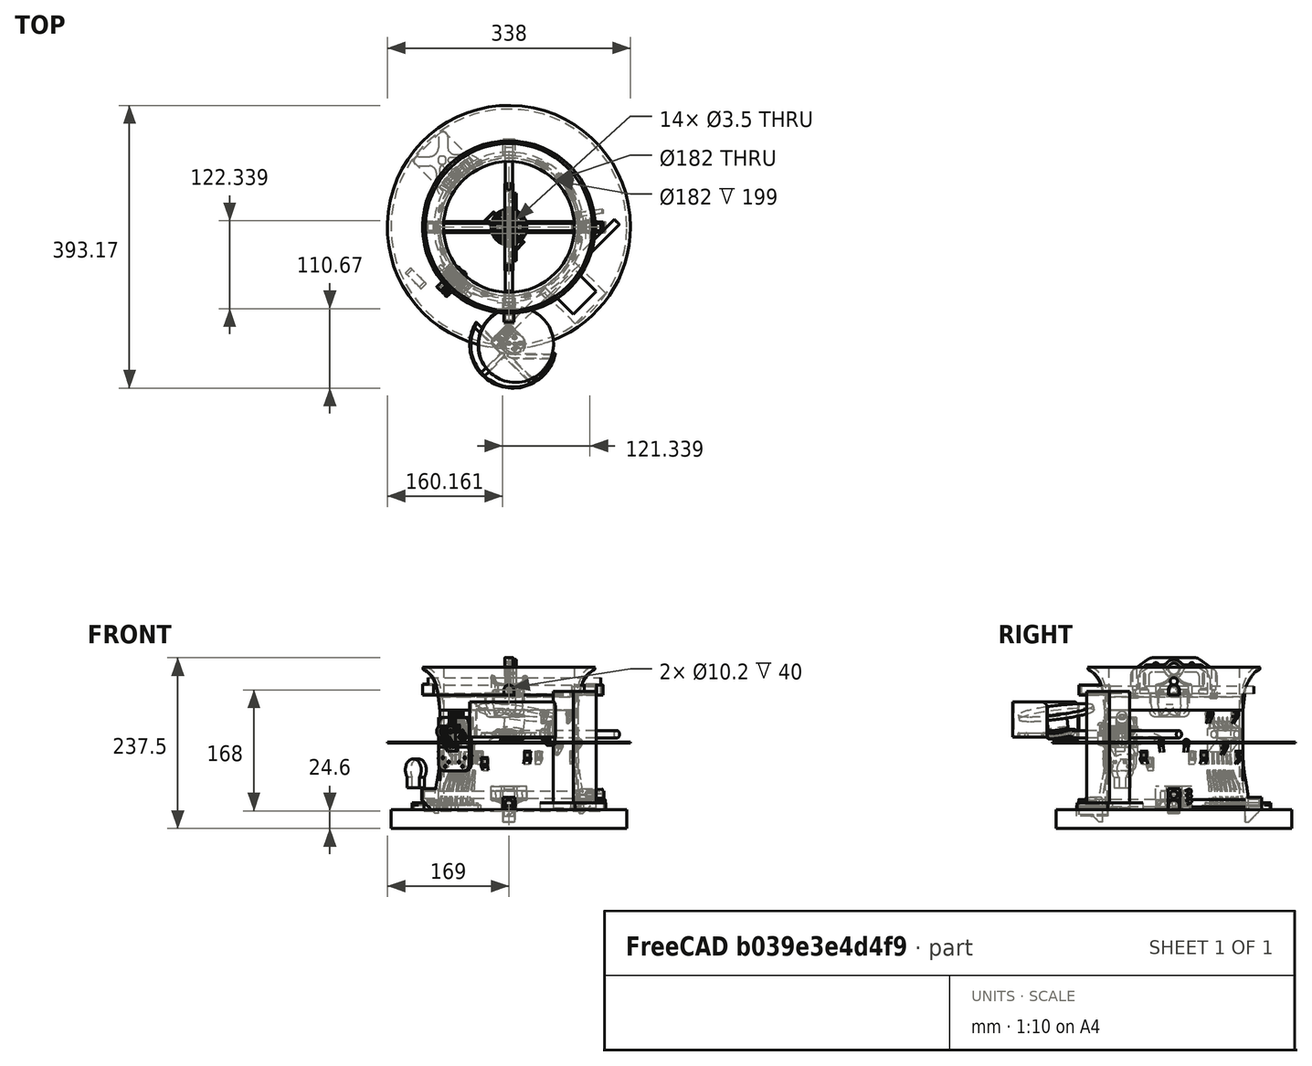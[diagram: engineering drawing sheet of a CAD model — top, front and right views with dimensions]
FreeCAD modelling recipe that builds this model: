
FCSTD DOCUMENT  (FreeCAD 0.19R24276 (Git))
Label: NEVA-CYLCOPE-MARK2
License: All rights reserved
LicenseURL: http://en.wikipedia.org/wiki/All_rights_reserved
objects: Sketcher::SketchObject×128, PartDesign::Pad×65, PartDesign::Pocket×52, PartDesign::Body×34, PartDesign::Fillet×24, PartDesign::Mirrored×23, Part::FeaturePython×19, Spreadsheet::Sheet×8, PartDesign::Chamfer×8, App::Part×8, PartDesign::Revolution×6, PartDesign::Groove×4, PartDesign::PolarPattern×3, Part::Feature×2, PartDesign::Boolean×1, PartDesign::LinearPattern×1, Part::MultiFuse×1, Part::Mirroring×1, Part::Fuse×1
note: 532 computed .brp shape members not serialized (recipe doc carries the construction recipe); baked Part::Feature solids carry a one-line shape summary decoded from their .brp

FEATURE [Spreadsheet::Sheet] Spreadsheet  label="sta"
  cells = A1=DONNEES POUR LE DESIGN DES STA; A2=Main_diam_base; B2=50; D2=base_pad; E2=6; A3=Carbon tube diam; B3=10.2; D3=epaisseur-renfort; E3==B3 / 2; A4=Epaisseur autour carbon; B4=3; A5=Distance entre 2 tubes; B5=2; A7=Distance entre 2 stators; B7=123; A8=> z position sta inlet; B8==B7 + 2 * E2; A10=Passage bullet tmotor; A11=diamètre bullet; B11=5.6; A12=diamètre cable; B12=2.4
FEATURE [Sketcher::SketchObject] Sketch001
  FullyConstrained = true
  MapMode = 5
  Placement = pos=(0,0,0) rot=(1,0,0;1.5708rad)
  Support = -> [XZ_Plane001]
  expr: Constraints[10] = <<sta>>.B3 / 2
  expr: Constraints[0] = <<sta>>.B3 + <<sta>>.B4 * 2
  sketch-geometry (4):
    g0: ArcOfCircle CenterX=0 CenterY=5.1 CenterZ=0 NormalX=0 NormalY=0 NormalZ=1 AngleXU=0 Radius=8.1 StartAngle=0 EndAngle=3.14159
    g1: LineSegment StartX=-8.1 StartY=0 StartZ=0 EndX=8.1 EndY=0 EndZ=0
    g2: LineSegment StartX=-8.1 StartY=5.1 StartZ=0 EndX=-8.1 EndY=0 EndZ=0
    g3: LineSegment StartX=8.1 StartY=5.1 StartZ=0 EndX=8.1 EndY=0 EndZ=0
  constraints (12):
    c: Diameter(g0) = 16.2
    c: PointOnObject(g1,g-1)
    c: Horizontal(g1)
    c: Coincident(g2,g1)
    c: Coincident(g3,g0)
    c: Coincident(g3,g1)
    c: Perpendicular(g3,g1)
    c: Perpendicular(g1,g2)
    c: Equal(g2,g3)
    c: Tangent(g2,g0) = -1.5708
    c: DistanceY(g0) = 5.1
    c: PointOnObject(g0,g-2)
FEATURE [PartDesign::Pad] Pad001  label="tube_inf"
  Direction = (1,1,1)
  Length = 50
  Length2 = 100
  Midplane = true
  Placement = pos=(0,0,0) rot=(1,0,0;1.5708rad)
  Profile = -> Sketch001
  Refine = true
  Type = 0
  expr: Length = <<sta>>.B2
FEATURE [Sketcher::SketchObject] Sketch002
  FullyConstrained = true
  MapMode = 5
  Placement = pos=(0,0,0) rot=(0.57735,0.57735,0.57735;2.0944rad)
  Support = -> [YZ_Plane001]
  expr: Constraints[11] = <<sta>>.B3 + <<sta>>.B4 * 2
  expr: Constraints[1] = <<sta>>.B5 + 1.5 * <<sta>>.B3
  sketch-geometry (4):
    g0: ArcOfCircle CenterX=0 CenterY=17.3 CenterZ=0 NormalX=0 NormalY=0 NormalZ=1 AngleXU=0 Radius=8.1 StartAngle=0 EndAngle=3.14159
    g1: LineSegment StartX=-8.1 StartY=17.3 StartZ=0 EndX=-8.1 EndY=0 EndZ=0
    g2: LineSegment StartX=8.1 StartY=17.3 StartZ=0 EndX=8.1 EndY=0 EndZ=0
    g3: LineSegment StartX=-8.1 StartY=0 StartZ=0 EndX=8.1 EndY=0 EndZ=0
  constraints (12):
    c: PointOnObject(g0,g-2)
    c: DistanceY(g0) = 17.3
    c: PointOnObject(g1,g-1)
    c: Vertical(g1)
    c: Coincident(g2,g0)
    c: PointOnObject(g2,g-1)
    c: Vertical(g2)
    c: Coincident(g3,g1)
    c: Coincident(g3,g2)
    c: Tangent(g1,g0) = -1.5708
    c: Equal(g2,g1)
    c: Diameter(g0) = 16.2
FEATURE [PartDesign::Pad] Pad002  label="tube_sup"
  BaseFeature = -> Pad001
  Direction = (1,1,1)
  Length = 50
  Length2 = 100
  Midplane = true
  Placement = pos=(0,0,0) rot=(1,0,0;1.5708rad)
  Profile = -> Sketch002
  Refine = true
  Type = 0
  expr: Length = <<sta>>.B2
FEATURE [Sketcher::SketchObject] Sketch003
  FullyConstrained = true
  MapMode = 5
  Placement = pos=(0,0,0) rot=(0.57735,0.57735,0.57735;2.0944rad)
  Support = -> [YZ_Plane001]
  expr: Constraints[2] = 1.5 * <<sta>>.B3 + <<sta>>.B5
  expr: Constraints[1] = <<sta>>.B3
  sketch-geometry (1):
    g0: Circle CenterX=0 CenterY=17.3 CenterZ=0 NormalX=0 NormalY=0 NormalZ=1 AngleXU=0 Radius=5.1
  constraints (3):
    c: PointOnObject(g0,g-2)
    c: Diameter(g0) = 10.2
    c: DistanceY(g0) = 17.3
FEATURE [Sketcher::SketchObject] Sketch004
  FullyConstrained = true
  MapMode = 5
  Placement = pos=(0,0,0) rot=(1,0,0;1.5708rad)
  Support = -> [XZ_Plane001]
  expr: Constraints[2] = <<sta>>.B3 / 2
  expr: Constraints[1] = <<sta>>.B3
  sketch-geometry (1):
    g0: Circle CenterX=0 CenterY=5.1 CenterZ=0 NormalX=0 NormalY=0 NormalZ=1 AngleXU=0 Radius=5.1
  constraints (3):
    c: PointOnObject(g0,g-2)
    c: Diameter(g0) = 10.2
    c: DistanceY(g0) = 5.1
FEATURE [Sketcher::SketchObject] Sketch005
  FullyConstrained = false
  MapMode = 5
  Support = -> [XY_Plane001]
  expr: Constraints[1] = <<sta>>.B2
  sketch-geometry (2):
    g0: Circle CenterX=0 CenterY=0 CenterZ=0 NormalX=0 NormalY=0 NormalZ=1 AngleXU=0 Radius=25
    g1: Circle CenterX=0 CenterY=0 CenterZ=0 NormalX=0 NormalY=0 NormalZ=1 AngleXU=0 Radius=32.5573
  constraints (3):
    c: Coincident(g0,g-1)
    c: Diameter(g0) = 50
    c: Coincident(g1,g0)
FEATURE [Sketcher::SketchObject] Sketch006
  AttachmentOffset = pos=(0,0,0) rot=(0,0,1;0.785398rad)
  FullyConstrained = true
  MapMode = 5
  Placement = pos=(0,0,0) rot=(0,0,1;0.785398rad)
  Support = -> [XY_Plane001]
  expr: Constraints[1] = <<screw>>.B5 + 0.3
  sketch-geometry (1):
    g0: Circle CenterX=-12.5 CenterY=0 CenterZ=0 NormalX=0 NormalY=0 NormalZ=1 AngleXU=0 Radius=2.95
  constraints (3):
    c: PointOnObject(g0,g-1)
    c: Diameter(g0) = 5.9
    c: DistanceX(g0) = -12.5
FEATURE [Sketcher::SketchObject] Sketch007
  AttachmentOffset = pos=(0,0,0) rot=(0,0,1;0.785398rad)
  FullyConstrained = true
  MapMode = 5
  Placement = pos=(0,0,0) rot=(0,0,1;0.785398rad)
  Support = -> [XY_Plane001]
  expr: Constraints[1] = <<screw>>.B4 + 0.25
  sketch-geometry (1):
    g0: Circle CenterX=-12.5 CenterY=0 CenterZ=0 NormalX=0 NormalY=0 NormalZ=1 AngleXU=0 Radius=1.75
  constraints (3):
    c: PointOnObject(g0,g-1)
    c: Diameter(g0) = 3.5
    c: DistanceX(g0) = -12.5
FEATURE [Sketcher::SketchObject] Sketch008
  AttachmentOffset = pos=(0,0,-6) rot=(0,0,1;0rad)
  FullyConstrained = true
  MapMode = 5
  Placement = pos=(0,0,-6) rot=(0,0,1;0rad)
  Support = -> [XY_Plane001]
  expr: .AttachmentOffset.Base.z = -<<sta>>.E2
  sketch-geometry (1):
    g0: Circle CenterX=0 CenterY=0 CenterZ=0 NormalX=0 NormalY=0 NormalZ=1 AngleXU=0 Radius=6.25
  constraints (2):
    c: Coincident(g0,g-1)
    c: Diameter(g0) = 12.5
FEATURE [Spreadsheet::Sheet] Spreadsheet001  label="sho"
  cells = A1=DONNEES POUR LE DESIGN DU SHO; A3=inner-diam; B3=182; A4=thickness; B4=5; A5=Hauteur tube principal; B5==198.5 - D6 - D7; A6=deport diffuseur; B6=8; C6=hauteur outlet; D6=80; A7=Deport inlet; B7=25; C7=hauteur inlet; D7=60; A8=Nervure renfort epaisseur; B8=2.9; A10=PASSAGE COLIERS SERRAGE; A11=largeur; B11=3.8; A12=épaisseur; B12=1.7; A13=diamètre de cables; B13=10
FEATURE [Spreadsheet::Sheet] Spreadsheet002  label="screw"
  cells = A2=M3 SCREW PARAM; A4=M3 diam; B4=3.25; A5=M3 head diam; B5=5.6; A6=M3 NUT height; B6=5.5; A7=M3 NYLSTOP NUT depth; B7=4.1
FEATURE [Spreadsheet::Sheet] Spreadsheet003  label="plug"
  cells = A1=DONNEES POUR LES PLUGS STATOR; A3=longueur emboitement; B3==20 - <<sho>>.B4; A4=epaisseur autour cabron; B4=3; A5=longueur butée; B5=3; D5=> longueur ajustement vis; E5==B3 - 2 * B4 - B5; A6=Overangle; B6==45°; D6=> Hauteur pad; E6==(B3 + B5) / tan(B6); A7=POSITION; A8=z_inf; B8==-B4; A9=z_sup; B9==B8 + <<sta>>.B3 + <<sta>>.B5
FEATURE [Sketcher::SketchObject] Sketch023
  FullyConstrained = true
  MapMode = 5
  Support = -> [XY_Plane005]
  expr: Constraints[4] = -<<sho>>.B3 / 2
  expr: Constraints[5] = <<sho>>.B4 + <<plug>>.B3 + <<plug>>.B5
  expr: Constraints[6] = <<sta>>.B3 + 2 * <<plug>>.B4
  sketch-geometry (4):
    g0: LineSegment StartX=-91 StartY=-8.1 StartZ=0 EndX=-114 EndY=-8.1 EndZ=0
    g1: LineSegment StartX=-114 StartY=-8.1 StartZ=0 EndX=-114 EndY=8.1 EndZ=0
    g2: LineSegment StartX=-114 StartY=8.1 StartZ=0 EndX=-91 EndY=8.1 EndZ=0
    g3: ArcOfCircle CenterX=0 CenterY=0 CenterZ=0 NormalX=0 NormalY=0 NormalZ=1 AngleXU=0 Radius=91.3598 StartAngle=3.05282 EndAngle=3.23037
  constraints (11):
    c: Coincident(g0,g1)
    c: Coincident(g1,g2)
    c: Horizontal(g0)
    c: Horizontal(g2)
    c: DistanceX(g2) = -91
    c: DistanceX(g2,g2) = 23
    c: DistanceY(g1,g1) = 16.2
    c: Symmetric(g1,g0,g-1)
    c: Coincident(g3,g-1)
    c: Coincident(g3,g0)
    c: Coincident(g3,g2)
FEATURE [PartDesign::Pad] Pad003
  Direction = (1,1,1)
  Length = 16.2
  Length2 = 18
  Profile = -> Sketch023
  Refine = true
  Type = 4
  expr: Length = <<plug>>.B4 * 2 + <<sta>>.B3
  expr: Length2 = <<plug>>.E6
FEATURE [Sketcher::SketchObject] Sketch024
  FullyConstrained = false
  MapMode = 5
  Placement = pos=(0,0,0) rot=(1,0,0;1.5708rad)
  Support = -> [XZ_Plane005]
  expr: Constraints[2] = -(<<sho>>.B3 / 2 + <<sho>>.B4)
  expr: Constraints[5] = <<plug>>.E6
  expr: Constraints[8] = 90° - <<plug>>.B6
  sketch-geometry (7):
    g0: GeomPoint X=-114 Y=0 Z=0
    g1: GeomPoint X=-96 Y=0 Z=0
    g2: LineSegment StartX=-96 StartY=-18 StartZ=0 EndX=-114 EndY=0 EndZ=0
    g3: LineSegment StartX=-122.918 StartY=-18 StartZ=0 EndX=-96 EndY=-18 EndZ=0
    g4: LineSegment StartX=-114 StartY=0 StartZ=0 EndX=-114 EndY=27.4578 EndZ=0
    g5: LineSegment StartX=-122.918 StartY=-18 StartZ=0 EndX=-122.918 EndY=27.4578 EndZ=0
    g6: LineSegment StartX=-122.918 StartY=27.4578 StartZ=0 EndX=-114 EndY=27.4578 EndZ=0
  constraints (16):
    c: PointOnObject(g0,g-1)
    c: PointOnObject(g1,g-1)
    c: DistanceX(g1) = -96
    c: Coincident(g2,g0)
    c: DistanceX(g2,g1) = 0
    c: DistanceY(g2,g1) = 18
    c: Coincident(g3,g2)
    c: Horizontal(g3)
    c: Angle(g2,g3) = 0.785398
    c: Coincident(g4,g2)
    c: Vertical(g4)
    c: Coincident(g5,g3)
    c: Vertical(g5)
    c: Coincident(g6,g5)
    c: Coincident(g6,g4)
    c: Horizontal(g6)
FEATURE [PartDesign::Groove] Groove
  Angle = 360
  Axis = (0,-2e-16,1)
  Base = (0,0,0)
  BaseFeature = -> Pad003
  Profile = -> Sketch024
  ReferenceAxis = -> Sketch024 [V_Axis]
  Refine = true
  Reversed = true
FEATURE [Sketcher::SketchObject] Sketch025
  FullyConstrained = true
  MapMode = 5
  Placement = pos=(0,0,0) rot=(1,0,0;1.5708rad)
  Support = -> [XZ_Plane005]
  expr: Constraints[0] = -<<sho>>.B3 / 2 - <<sho>>.B4 - <<plug>>.B3 / 2 - 2
  expr: Constraints[1] = <<sta>>.B3 / 2 + <<plug>>.B4
  expr: Constraints[4] = <<plug>>.E5 / 2
  expr: Constraints[5] = <<plug>>.E5 / 2
  expr: Constraints[8] = <<screw>>.B4
  sketch-geometry (7):
    g0: GeomPoint X=-105.5 Y=8.1 Z=0
    g1: GeomPoint X=-102.5 Y=8.1 Z=0
    g2: GeomPoint X=-108.5 Y=8.1 Z=0
    g3: ArcOfCircle CenterX=-108.5 CenterY=8.1 CenterZ=0 NormalX=0 NormalY=0 NormalZ=1 AngleXU=0 Radius=1.625 StartAngle=1.5708 EndAngle=4.71239
    g4: ArcOfCircle CenterX=-102.5 CenterY=8.1 CenterZ=0 NormalX=0 NormalY=0 NormalZ=1 AngleXU=0 Radius=1.625 StartAngle=4.71239 EndAngle=7.85398
    g5: LineSegment StartX=-108.5 StartY=9.725 StartZ=0 EndX=-102.5 EndY=9.725 EndZ=0
    g6: LineSegment StartX=-108.5 StartY=6.475 StartZ=0 EndX=-102.5 EndY=6.475 EndZ=0
  constraints (16):
    c: DistanceX(g0) = -105.5
    c: DistanceY(g0) = 8.1
    c: DistanceY(g0,g2) = 0
    c: DistanceY(g0,g1) = 0
    c: DistanceX(g2,g0) = 3
    c: DistanceX(g0,g1) = 3
    c: Coincident(g3,g2)
    c: Coincident(g4,g1)
    c: Diameter(g3) = 3.25
    c: Equal(g3,g4)
    c: Coincident(g5,g4)
    c: Horizontal(g5)
    c: Coincident(g6,g4)
    c: Horizontal(g6)
    c: Tangent(g6,g3) = -1.5708
    c: Tangent(g5,g3) = 1.5708
FEATURE [PartDesign::Pocket] Pocket014
  BaseFeature = -> Groove
  Length = 5
  Length2 = 100
  Midplane = true
  Profile = -> Sketch025
  Refine = true
  Type = 1
FEATURE [Sketcher::SketchObject] Sketch028
  AttachmentOffset = pos=(0,0,-6.77) rot=(0,0,1;0rad)
  FullyConstrained = true
  MapMode = 5
  Placement = pos=(0,6.77,1.5e-15) rot=(1,0,0;1.5708rad)
  Support = -> [XZ_Plane005]
  expr: Constraints[8] = <<screw>>.B5
  expr: Constraints[5] = <<plug>>.E5 / 2
  expr: Constraints[4] = <<plug>>.E5 / 2
  expr: Constraints[1] = <<sta>>.B3 / 2 + <<plug>>.B4
  expr: Constraints[0] = -<<sho>>.B3 / 2 - <<sho>>.B4 - <<plug>>.B3 / 2 - 2
  expr: .AttachmentOffset.Base.z = -<<sta>>.B3 / 2 - 1.67
  sketch-geometry (7):
    g0: GeomPoint X=-105.5 Y=8.1 Z=0
    g1: GeomPoint X=-102.5 Y=8.1 Z=0
    g2: GeomPoint X=-108.5 Y=8.1 Z=0
    g3: ArcOfCircle CenterX=-108.5 CenterY=8.1 CenterZ=0 NormalX=0 NormalY=0 NormalZ=1 AngleXU=0 Radius=2.8 StartAngle=1.5708 EndAngle=4.71239
    g4: ArcOfCircle CenterX=-102.5 CenterY=8.1 CenterZ=0 NormalX=0 NormalY=0 NormalZ=1 AngleXU=0 Radius=2.8 StartAngle=4.71239 EndAngle=7.85398
    g5: LineSegment StartX=-108.5 StartY=10.9 StartZ=0 EndX=-102.5 EndY=10.9 EndZ=0
    g6: LineSegment StartX=-108.5 StartY=5.3 StartZ=0 EndX=-102.5 EndY=5.3 EndZ=0
  constraints (16):
    c: DistanceX(g0) = -105.5
    c: DistanceY(g0) = 8.1
    c: DistanceY(g0,g2) = 0
    c: DistanceY(g0,g1) = 0
    c: DistanceX(g2,g0) = 3
    c: DistanceX(g0,g1) = 3
    c: Coincident(g3,g2)
    c: Coincident(g4,g1)
    c: Diameter(g3) = 5.6
    c: Equal(g3,g4)
    c: Coincident(g5,g4)
    c: Horizontal(g5)
    c: Coincident(g6,g4)
    c: Horizontal(g6)
    c: Tangent(g6,g3) = -1.5708
    c: Tangent(g5,g3) = 1.5708
FEATURE [Sketcher::SketchObject] Sketch029
  AttachmentOffset = pos=(0,0,6.77) rot=(0,0,1;0rad)
  FullyConstrained = true
  MapMode = 5
  Placement = pos=(0,-6.77,-1.5e-15) rot=(1,0,0;1.5708rad)
  Support = -> [XZ_Plane005]
  expr: Constraints[5] = <<plug>>.E5 / 2
  expr: Constraints[1] = <<sta>>.B3 / 2 + <<plug>>.B4
  expr: .AttachmentOffset.Base.z = <<sta>>.B3 / 2 + 1.67
  expr: Constraints[4] = <<plug>>.E5 / 2
  expr: Constraints[0] = -<<sho>>.B3 / 2 - <<sho>>.B4 - <<plug>>.B3 / 2 - 2
  expr: Constraints[18] = <<screw>>.B6
  sketch-geometry (15):
    g0: GeomPoint X=-105.5 Y=8.1 Z=0
    g1: GeomPoint X=-102.5 Y=8.1 Z=0
    g2: GeomPoint X=-108.5 Y=8.1 Z=0
    g3: LineSegment StartX=-99.3246 StartY=8.1 StartZ=0 EndX=-100.912 EndY=10.85 EndZ=0
    g4: LineSegment StartX=-100.912 StartY=10.85 StartZ=0 EndX=-104.088 EndY=10.85 EndZ=0
    g5: LineSegment StartX=-104.088 StartY=5.35 StartZ=0 EndX=-100.912 EndY=5.35 EndZ=0
    g6: LineSegment StartX=-100.912 StartY=5.35 StartZ=0 EndX=-99.3246 EndY=8.1 EndZ=0
    g7: Circle CenterX=-102.5 CenterY=8.1 CenterZ=0 NormalX=0 NormalY=0 NormalZ=1 AngleXU=0 Radius=3.17543
    g8: LineSegment StartX=-106.912 StartY=10.85 StartZ=0 EndX=-104.088 EndY=10.85 EndZ=0
    g9: LineSegment StartX=-106.912 StartY=5.35 StartZ=0 EndX=-104.088 EndY=5.35 EndZ=0
    g10: LineSegment StartX=-110.088 StartY=10.85 StartZ=0 EndX=-111.675 EndY=8.1 EndZ=0
    g11: LineSegment StartX=-111.675 StartY=8.1 StartZ=0 EndX=-110.088 EndY=5.35 EndZ=0
    g12: LineSegment StartX=-110.088 StartY=5.35 StartZ=0 EndX=-106.912 EndY=5.35 EndZ=0
    g13: LineSegment StartX=-106.912 StartY=10.85 StartZ=0 EndX=-110.088 EndY=10.85 EndZ=0
    g14: Circle CenterX=-108.5 CenterY=8.1 CenterZ=0 NormalX=0 NormalY=0 NormalZ=1 AngleXU=0 Radius=3.17543
  constraints (37):
    c: DistanceX(g0) = -105.5
    c: DistanceY(g0) = 8.1
    c: DistanceY(g0,g2) = 0
    c: DistanceY(g0,g1) = 0
    c: DistanceX(g2,g0) = 3
    c: DistanceX(g0,g1) = 3
    c: Coincident(g3,g4)
    c: Coincident(g5,g6)
    c: Coincident(g6,g3)
    c: Equal(g3,g4)
    c: Equal(g3,g5)
    c: Equal(g3,g6)
    c: PointOnObject(g3,g7)
    c: PointOnObject(g4,g7)
    c: PointOnObject(g5,g7)
    c: PointOnObject(g5,g7)
    c: PointOnObject(g6,g7)
    c: Coincident(g7,g1)
    c: DistanceY(g5,g3) = 5.5
    c: Parallel(g9,g-1)
    c: Tangent(g9,g5) = -1.5708
    c: Tangent(g8,g4) = 1.5708
    c: Parallel(g8,g-1)
    c: Coincident(g10,g11)
    c: Coincident(g11,g12)
    c: Coincident(g13,g10)
    c: Equal(g10,g11)
    c: Equal(g10,g12)
    c: Equal(g10,g13)
    c: PointOnObject(g10,g14)
    c: PointOnObject(g11,g14)
    c: PointOnObject(g12,g14)
    c: PointOnObject(g13,g14)
    c: PointOnObject(g13,g14)
    c: Coincident(g14,g2)
    c: Tangent(g12,g9) = -1.5708
    c: Coincident(g8,g13)
FEATURE [PartDesign::Pocket] Pocket015
  BaseFeature = -> Pocket014
  Length = 5
  Length2 = 100
  Profile = -> Sketch028
  Refine = true
  Type = 0
FEATURE [Sketcher::SketchObject] Sketch030
  AttachmentOffset = pos=(0,0,6.77) rot=(0,0,1;0rad)
  FullyConstrained = true
  MapMode = 5
  Placement = pos=(0,-6.77,-1.5e-15) rot=(1,0,0;1.5708rad)
  Support = -> [XZ_Plane005]
  expr: Constraints[18] = <<screw>>.B6
  expr: Constraints[0] = -<<sho>>.B3 / 2 - <<sho>>.B4 - <<plug>>.B3 / 2 - 2
  expr: Constraints[4] = <<plug>>.E5 / 2
  expr: .AttachmentOffset.Base.z = <<sta>>.B3 / 2 + 1.67
  expr: Constraints[1] = <<sta>>.B3 / 2 + <<plug>>.B4
  expr: Constraints[5] = <<plug>>.E5 / 2
  expr: Constraints[44] = <<screw>>.B6 + <<plug>>.B4
  sketch-geometry (19):
    g0: GeomPoint X=-105.5 Y=8.1 Z=0
    g1: GeomPoint X=-102.5 Y=8.1 Z=0
    g2: GeomPoint X=-108.5 Y=8.1 Z=0
    g3: LineSegment StartX=-99.3246 StartY=8.1 StartZ=0 EndX=-100.912 EndY=10.85 EndZ=0
    g4: LineSegment StartX=-100.912 StartY=10.85 StartZ=0 EndX=-104.088 EndY=10.85 EndZ=0
    g5: LineSegment StartX=-104.088 StartY=5.35 StartZ=0 EndX=-100.912 EndY=5.35 EndZ=0
    g6: LineSegment StartX=-100.912 StartY=5.35 StartZ=0 EndX=-99.3246 EndY=8.1 EndZ=0
    g7: Circle CenterX=-102.5 CenterY=8.1 CenterZ=0 NormalX=0 NormalY=0 NormalZ=1 AngleXU=0 Radius=3.17543
    g8: LineSegment StartX=-106.912 StartY=10.85 StartZ=0 EndX=-104.088 EndY=10.85 EndZ=0
    g9: LineSegment StartX=-106.912 StartY=5.35 StartZ=0 EndX=-104.088 EndY=5.35 EndZ=0
    g10: LineSegment StartX=-110.088 StartY=10.85 StartZ=0 EndX=-111.675 EndY=8.1 EndZ=0
    g11: LineSegment StartX=-111.675 StartY=8.1 StartZ=0 EndX=-110.088 EndY=5.35 EndZ=0
    g12: LineSegment StartX=-110.088 StartY=5.35 StartZ=0 EndX=-106.912 EndY=5.35 EndZ=0
    g13: LineSegment StartX=-106.912 StartY=10.85 StartZ=0 EndX=-110.088 EndY=10.85 EndZ=0
    g14: Circle CenterX=-108.5 CenterY=8.1 CenterZ=0 NormalX=0 NormalY=0 NormalZ=1 AngleXU=0 Radius=3.17543
    g15: ArcOfCircle CenterX=-102.5 CenterY=8.1 CenterZ=0 NormalX=0 NormalY=0 NormalZ=1 AngleXU=0 Radius=4.25 StartAngle=4.71239 EndAngle=7.85398
    g16: ArcOfCircle CenterX=-108.5 CenterY=8.1 CenterZ=0 NormalX=0 NormalY=0 NormalZ=1 AngleXU=0 Radius=4.25 StartAngle=1.5708 EndAngle=4.71239
    g17: LineSegment StartX=-102.5 StartY=12.35 StartZ=0 EndX=-108.5 EndY=12.35 EndZ=0
    g18: LineSegment StartX=-102.5 StartY=3.85 StartZ=0 EndX=-108.5 EndY=3.85 EndZ=0
  constraints (45):
    c: DistanceX(g0) = -105.5
    c: DistanceY(g0) = 8.1
    c: DistanceY(g0,g2) = 0
    c: DistanceY(g0,g1) = 0
    c: DistanceX(g2,g0) = 3
    c: DistanceX(g0,g1) = 3
    c: Coincident(g3,g4)
    c: Coincident(g5,g6)
    c: Coincident(g6,g3)
    c: Equal(g3,g4)
    c: Equal(g3,g5)
    c: Equal(g3,g6)
    c: PointOnObject(g3,g7)
    c: PointOnObject(g4,g7)
    c: PointOnObject(g5,g7)
    c: PointOnObject(g5,g7)
    c: PointOnObject(g6,g7)
    c: Coincident(g7,g1)
    c: DistanceY(g5,g3) = 5.5
    c: Parallel(g9,g-1)
    c: Tangent(g9,g5) = -1.5708
    c: Tangent(g8,g4) = 1.5708
    c: Parallel(g8,g-1)
    c: Coincident(g10,g11)
    c: Coincident(g11,g12)
    c: Coincident(g13,g10)
    c: Equal(g10,g11)
    c: Equal(g10,g12)
    c: Equal(g10,g13)
    c: PointOnObject(g10,g14)
    c: PointOnObject(g11,g14)
    c: PointOnObject(g12,g14)
    c: PointOnObject(g13,g14)
    c: PointOnObject(g13,g14)
    c: Coincident(g14,g2)
    c: Tangent(g12,g9) = -1.5708
    c: Coincident(g8,g13)
    c: Tangent(g15,g18) = 1.5708
    c: Tangent(g15,g17) = -1.5708
    c: Tangent(g17,g16) = -1.5708
    c: Tangent(g18,g16) = 1.5708
    c: Horizontal(g17)
    c: Coincident(g15,g1)
    c: Coincident(g16,g2)
    c: DistanceY(g15,g15) = 8.5
FEATURE [PartDesign::Pad] Pad004
  BaseFeature = -> Pocket015
  Direction = (1,1,1)
  Length = 2.43
  Length2 = 100
  Profile = -> Sketch030
  Refine = true
  Type = 0
  expr: Length = <<screw>>.B7 - 1.67
FEATURE [PartDesign::Pocket] Pocket016
  BaseFeature = -> Pad004
  Length = 5
  Length2 = 100
  Profile = -> Sketch029
  Refine = true
  Reversed = true
  Type = 0
FEATURE [PartDesign::Chamfer] Chamfer
  Angle = 45
  Base = -> Pocket016 [Edge28]
  BaseFeature = -> Pocket016
  ChamferType = 0
  FlipDirection = false
  Refine = true
  Size = 0.9
  Size2 = 1
  SupportTransform = false
FEATURE [Sketcher::SketchObject] Sketch035
  FullyConstrained = true
  MapMode = 5
  Support = -> [XY_Plane006]
  expr: Constraints[2] = <<sta>>.B2
  expr: Constraints[3] = <<sta>>.B2 - 2 * <<sta>>.E3
  sketch-geometry (2):
    g0: Circle CenterX=0 CenterY=0 CenterZ=0 NormalX=0 NormalY=0 NormalZ=1 AngleXU=0 Radius=25
    g1: Circle CenterX=0 CenterY=0 CenterZ=0 NormalX=0 NormalY=0 NormalZ=1 AngleXU=0 Radius=19.9
  constraints (4):
    c: Coincident(g0,g-1)
    c: Coincident(g1,g0)
    c: Diameter(g0) = 50
    c: Diameter(g1) = 39.8
FEATURE [PartDesign::Pad] Pad005
  Direction = (1,1,1)
  Length = 25.4
  Length2 = 1
  Profile = -> Sketch035
  Refine = true
  Type = 4
  expr: Length = <<sta>>.B3 * 2 + <<sta>>.B4 + <<sta>>.B5
FEATURE [Sketcher::SketchObject] Sketch036
  FullyConstrained = false
  MapMode = 5
  Placement = pos=(0,0,0) rot=(0.57735,0.57735,0.57735;2.0944rad)
  Support = -> [YZ_Plane006]
  expr: Constraints[0] = -<<sta>>.B2 / 2
  expr: Constraints[1] = <<sta>>.B3 + <<sta>>.B4
  expr: Constraints[6] = <<sta>>.B3 * 1.5 + <<sta>>.B5
  expr: Constraints[8] = <<sta>>.B3 * 2 + <<sta>>.B4 + <<sta>>.B5
  sketch-geometry (7):
    g0: GeomPoint X=-25 Y=13.2 Z=0
    g1: ArcOfCircle CenterX=-25 CenterY=36.8148 CenterZ=0 NormalX=0 NormalY=0 NormalZ=1 AngleXU=0 Radius=23.6148 StartAngle=4.71239 EndAngle=5.62039
    g2: ArcOfCircle CenterX=0 CenterY=17.3 CenterZ=0 NormalX=0 NormalY=0 NormalZ=1 AngleXU=0 Radius=8.1 StartAngle=1.5708 EndAngle=2.4788
    g3: LineSegment StartX=-25 StartY=13.2 StartZ=0 EndX=-32.5995 EndY=13.2 EndZ=0
    g4: LineSegment StartX=-32.5995 StartY=13.2 StartZ=0 EndX=-32.5995 EndY=33.6481 EndZ=0
    g5: LineSegment StartX=-32.5995 StartY=33.6481 StartZ=0 EndX=0 EndY=33.6481 EndZ=0
    g6: LineSegment StartX=0 StartY=33.6481 StartZ=0 EndX=0 EndY=25.4 EndZ=0
  constraints (18):
    c: DistanceX(g0) = -25
    c: DistanceY(g0) = 13.2
    c: Coincident(g1,g0)
    c: DistanceX(g1,g1) = 0
    c: PointOnObject(g2,g-2)
    c: PointOnObject(g2,g-2)
    c: DistanceY(g2) = 17.3
    c: Tangent(g2,g1) = 1.5708
    c: DistanceY(g2) = 25.4
    c: Coincident(g3,g1)
    c: Horizontal(g3)
    c: Coincident(g4,g3)
    c: Vertical(g4)
    c: Coincident(g5,g4)
    c: PointOnObject(g5,g-2)
    c: Horizontal(g5)
    c: Coincident(g6,g5)
    c: Coincident(g6,g2)
FEATURE [Sketcher::SketchObject] Sketch037
  FullyConstrained = true
  MapMode = 5
  Support = -> [XY_Plane001]
  expr: Constraints[1] = <<sta>>.B2
  sketch-geometry (1):
    g0: Circle CenterX=0 CenterY=0 CenterZ=0 NormalX=0 NormalY=0 NormalZ=1 AngleXU=0 Radius=25
  constraints (2):
    c: Coincident(g0,g-1)
    c: Diameter(g0) = 50
FEATURE [Sketcher::SketchObject] Sketch038
  AttachmentOffset = pos=(0,0,0) rot=(0,0,1;1.5708rad)
  FullyConstrained = true
  MapMode = 5
  Placement = pos=(0,0,0) rot=(0,0,1;1.5708rad)
  Support = -> [XY_Plane006]
  expr: Constraints[8] = <<sta>>.B2
  expr: Constraints[10] = <<sta>>.E3
  expr: Constraints[11] = <<sta>>.E3 / 2
  sketch-geometry (4):
    g0: LineSegment StartX=-24.8696 StartY=2.55 StartZ=0 EndX=24.8696 EndY=2.55 EndZ=0
    g1: LineSegment StartX=24.8696 StartY=-2.55 StartZ=0 EndX=-24.8696 EndY=-2.55 EndZ=0
    g2: ArcOfCircle CenterX=0 CenterY=0 CenterZ=0 NormalX=0 NormalY=0 NormalZ=1 AngleXU=0 Radius=25 StartAngle=3.03941 EndAngle=3.24377
    g3: ArcOfCircle CenterX=0 CenterY=0 CenterZ=0 NormalX=0 NormalY=0 NormalZ=1 AngleXU=0 Radius=25 StartAngle=6.18101 EndAngle=6.38536
  constraints (12):
    c: Horizontal(g0)
    c: Horizontal(g1)
    c: Coincident(g2,g-1)
    c: Coincident(g2,g0)
    c: Coincident(g2,g1)
    c: Coincident(g3,g2)
    c: Coincident(g3,g0)
    c: Coincident(g3,g1)
    c: Diameter(g2) = 50
    c: Equal(g2,g3)
    c: DistanceY(g1,g0) = 5.1
    c: DistanceY(g-1,g0) = 2.55
FEATURE [PartDesign::Pad] Pad007
  BaseFeature = -> Pad005
  Direction = (1,1,1)
  Length = 25.4
  Length2 = 100
  Profile = -> Sketch038
  Refine = true
  Type = 0
  expr: Length = <<sta>>.B3 * 2 + <<sta>>.B5 + <<sta>>.B4
FEATURE [PartDesign::Pocket] Pocket022
  BaseFeature = -> Pad007
  Length = 5
  Length2 = 100
  Midplane = true
  Profile = -> Sketch036
  Refine = true
  Type = 1
FEATURE [PartDesign::Mirrored] Mirrored
  BaseFeature = -> Pocket022
  MirrorPlane = -> Sketch036 [V_Axis]
  Originals = -> [Pocket022]
  Refine = true
FEATURE [PartDesign::Pad] Pad008  label="base_pad"
  BaseFeature = -> Pad002
  Direction = (1,1,1)
  Length = 6
  Length2 = 100
  Placement = pos=(0,0,0) rot=(1,0,0;1.5708rad)
  Profile = -> Sketch037
  Refine = true
  Reversed = true
  Type = 0
  expr: Length = <<sta>>.E2
FEATURE [PartDesign::Pocket] Pocket  label="central_moteur_hole"
  BaseFeature = -> Pad008
  Length = 4
  Length2 = 100
  Placement = pos=(0,0,0) rot=(1,0,0;1.5708rad)
  Profile = -> Sketch008
  Refine = true
  Reversed = true
  Type = 0
FEATURE [PartDesign::Fillet] Fillet
  Base = -> Mirrored [Face5]
  BaseFeature = -> Mirrored
  Radius = 2.11
  Refine = true
  SupportTransform = false
  expr: Radius = <<sta>>.E3 / 2 - 0.44
FEATURE [PartDesign::Body] Body004  label="renfort-support-moteur"
  Group = -> [Sketch035,Pad005,Sketch036,Sketch038,Pad007,Pocket022,Mirrored,Fillet]
  Origin = -> Origin006
  Tip = -> Fillet
FEATURE [PartDesign::Pocket] Pocket023  label="head-screw-hole"
  BaseFeature = -> Pocket
  Length = 5
  Length2 = 100
  Placement = pos=(0,0,0) rot=(1,0,0;1.5708rad)
  Profile = -> Sketch006
  Refine = true
  Reversed = true
  Type = 1
FEATURE [PartDesign::PolarPattern] PolarPattern
  Angle = 360
  Axis = -> Sketch006 [N_Axis]
  BaseFeature = -> Pocket023
  Occurrences = 4
  Originals = -> [Pocket023]
  Placement = pos=(0,0,0) rot=(1,0,0;1.5708rad)
  Refine = true
FEATURE [PartDesign::Pocket] Pocket024
  BaseFeature = -> PolarPattern
  Length = 5
  Length2 = 100
  Placement = pos=(0,0,0) rot=(1,0,0;1.5708rad)
  Profile = -> Sketch005
  Refine = true
  Reversed = true
  Type = 1
FEATURE [PartDesign::Boolean] Boolean
  BaseFeature = -> Pocket024
  Group = -> [Body004]
  Refine = true
  Type = 0
FEATURE [PartDesign::Pocket] Pocket025  label="screw-hole"
  BaseFeature = -> Boolean
  Length = 5
  Length2 = 100
  Profile = -> Sketch007
  Refine = true
  Type = 1
FEATURE [PartDesign::PolarPattern] PolarPattern001
  Angle = 360
  Axis = -> Sketch007 [N_Axis]
  BaseFeature = -> Pocket025
  Occurrences = 4
  Originals = -> [Pocket025]
  Refine = true
FEATURE [PartDesign::Pocket] Pocket026
  BaseFeature = -> PolarPattern001
  Length = 5
  Length2 = 100
  Midplane = true
  Profile = -> Sketch003
  Refine = true
  Type = 1
FEATURE [PartDesign::Pocket] Pocket027
  BaseFeature = -> Pocket026
  Length = 5
  Length2 = 100
  Midplane = true
  Profile = -> Sketch004
  Refine = true
  Type = 1
FEATURE [PartDesign::Body] Body001  label="support-moteur"
  Group = -> [Sketch001,Pad001,Sketch002,Pad002,Sketch006,Sketch037,Sketch005,Sketch007,Sketch008,Pad008,Pocket,Pocket023,PolarPattern,Pocket024,Boolean,Pocket025,PolarPattern001,Sketch003,Sketch004,Pocket026,Pocket027]
  Origin = -> Origin001
  Tip = -> Pocket027
FEATURE [Part::FeaturePython] Clone003  label="support-moteur001"  # Draft clone (typed FeaturePython)
  AttacherType = Attacher::AttachEngine3D
  Fuse = false
  Objects = -> [Body001]
  Placement = pos=(0,0,-135) rot=(0.707107,0.707107,0;3.14159rad)
  Scale = (1,1,1)
  expr: .Placement.Base.z = -<<sta>>.B8
FEATURE [Sketcher::SketchObject] Sketch
  FullyConstrained = true
  MapMode = 5
  Placement = pos=(0,0,0) rot=(0.57735,0.57735,0.57735;2.0944rad)
  Support = -> [YZ_Plane]
  expr: Constraints[1] = <<sta>>.B3
  expr: Constraints[2] = <<sta>>.B3 * 1.5 + <<sta>>.B5
  sketch-geometry (1):
    g0: Circle CenterX=0 CenterY=17.3 CenterZ=0 NormalX=0 NormalY=0 NormalZ=1 AngleXU=0 Radius=5.1
  constraints (3):
    c: PointOnObject(g0,g-2)
    c: Diameter(g0) = 10.2
    c: DistanceY(g0) = 17.3
FEATURE [PartDesign::Pad] Pad
  Direction = (1,1,1)
  Length = 112.5
  Length2 = 127.5
  Placement = pos=(0,0,0) rot=(0.57735,0.57735,0.57735;2.0944rad)
  Profile = -> Sketch
  Refine = true
  Type = 4
  expr: Length2 = 240 - (<<sho>>.B3 / 2 + <<sho>>.B4 + <<plug>>.B3 + 1.5)
  expr: Length = <<sho>>.B3 / 2 + <<sho>>.B4 + <<plug>>.B3 + 1.5
FEATURE [Sketcher::SketchObject] Sketch039
  FullyConstrained = false
  MapMode = 5
  Support = -> [XY_Plane]
  sketch-geometry (1):
    g0: Circle CenterX=0 CenterY=0 CenterZ=0 NormalX=0 NormalY=0 NormalZ=1 AngleXU=0 Radius=3.3078
  constraints (1):
    c: Coincident(g0,g-1)
FEATURE [PartDesign::Pad] Pad009
  BaseFeature = -> Pad
  Direction = (1,1,1)
  Length = 17
  Length2 = 100
  Placement = pos=(0,0,0) rot=(0.57735,0.57735,0.57735;2.0944rad)
  Profile = -> Sketch039
  Refine = true
  Type = 0
FEATURE [Sketcher::SketchObject] Sketch040
  FullyConstrained = true
  MapMode = 5
  Placement = pos=(0,0,0) rot=(1,0,0;1.5708rad)
  Support = -> [XZ_Plane]
  expr: Constraints[1] = <<sta>>.B3 / 2
  expr: Constraints[2] = <<sta>>.B3
  sketch-geometry (1):
    g0: Circle CenterX=0 CenterY=5.1 CenterZ=0 NormalX=0 NormalY=0 NormalZ=1 AngleXU=0 Radius=5.1
  constraints (3):
    c: PointOnObject(g0,g-2)
    c: DistanceY(g0) = 5.1
    c: Diameter(g0) = 10.2
FEATURE [PartDesign::Pad] Pad010
  BaseFeature = -> Pad009
  Direction = (1,1,1)
  Length = 111
  Length2 = 129
  Placement = pos=(0,0,0) rot=(0.57735,0.57735,0.57735;2.0944rad)
  Profile = -> Sketch040
  Refine = true
  Type = 4
  expr: Length2 = 240 - (<<sho>>.B3 / 2 + <<sho>>.B4 + <<plug>>.B3)
  expr: Length = <<sho>>.B3 / 2 + <<sho>>.B4 + <<plug>>.B3
FEATURE [PartDesign::Body] Body  label="carbon_tube-l240"
  Group = -> [Sketch,Pad,Sketch039,Pad009,Sketch040,Pad010]
  Origin = -> Origin
  Placement = pos=(0,0,0) rot=(0,0,1;3.14159rad)
  Tip = -> Pad010
FEATURE [PartDesign::Fillet] Fillet001
  Base = -> Chamfer [Edge37]
  BaseFeature = -> Chamfer
  Radius = 3
  Refine = true
  SupportTransform = false
FEATURE [PartDesign::Body] Body003  label="plug-sta-inf-ouvert"
  Group = -> [Sketch023,Pad003,Sketch024,Groove,Sketch025,Pocket014,Sketch028,Sketch029,Pocket015,Sketch030,Pad004,Pocket016,Chamfer,Fillet001]
  Origin = -> Origin005
  Placement = pos=(0,0,-3) rot=(0,0,1;1.5708rad)
  Tip = -> Fillet001
  expr: .Placement.Base.z = <<plug>>.B8
FEATURE [Sketcher::SketchObject] Sketch042
  FullyConstrained = false
  MapMode = 5
  Placement = pos=(0,0,0) rot=(1,0,0;1.5708rad)
  Support = -> [XZ_Plane008]
  expr: Constraints[1] = <<sho>>.B7 + <<sho>>.B3 / 2
  expr: Constraints[2] = <<sho>>.B3 / 2
  expr: Constraints[3] = -<<sho>>.D7
  expr: Constraints[18] = <<sho>>.B4
  sketch-geometry (19):
    g0: GeomPoint X=116 Y=0 Z=0
    g1: GeomPoint X=91 Y=-60 Z=0
    g2-g5: Circle x4 (B-spline internal-alignment scaffolding for g6; pole/knot coordinates omitted)
    g6: BSplineCurve PolesCount=4 KnotsCount=2 Degree=3 IsPeriodic=0
    g7: GeomPoint X=116 Y=0 Z=0
    g8: GeomPoint X=91 Y=-60 Z=0
    g9: LineSegment StartX=91 StartY=-60 StartZ=0 EndX=96 EndY=-60 EndZ=0
    g10-g13: Circle x4 (B-spline internal-alignment scaffolding for g14; pole/knot coordinates omitted)
    g14: BSplineCurve PolesCount=4 KnotsCount=2 Degree=3 IsPeriodic=0
    g15: GeomPoint X=96 Y=-60 Z=0
    g16: GeomPoint X=120 Y=-3 Z=0
    g17: LineSegment StartX=116 StartY=0 StartZ=0 EndX=120 EndY=0 EndZ=0
    g18: LineSegment StartX=120 StartY=0 StartZ=0 EndX=120 EndY=-3 EndZ=0
  constraints (31):
    c: PointOnObject(g0,g-1)
    c: DistanceX(g0) = 116
    c: DistanceX(g1) = 91
    c: DistanceY(g1) = -60
    c: Coincident(g6,g0)
    c: Weight(g2) = 1
    c: Equal(g2,g3)
    c: Equal(g2,g4)
    c: Equal(g2,g5)
    c: Coincident(g6,g1)
    c: InternalAlignment(g2-g5 -> g6) x4
    c: InternalAlignment(g7,g6)
    c: InternalAlignment(g8,g6)
    c: Coincident(g9,g6)
    c: Horizontal(g9)
    c: DistanceX(g9,g9) = 5
    c: Coincident(g14,g9)
    c: Weight(g10) = 1
    c: Equal(g10,g11)
    c: Equal(g10,g12)
    c: Equal(g10,g13)
    c: InternalAlignment(g10-g13 -> g14) x4
    c: InternalAlignment(g15,g14)
    c: InternalAlignment(g16,g14)
    c: Coincident(g17,g6)
    c: Horizontal(g17)
    c: Coincident(g18,g17)
    c: Vertical(g18)
    c: DistanceY(g18,g18) = 3
    c: DistanceX(g17,g17) = 4
    c: Coincident(g14,g18)
FEATURE [PartDesign::Revolution] Revolution  label="inlet"
  Angle = 360
  Axis = (0,-2e-16,1)
  Base = (0,0,0)
  Placement = pos=(0,0,0) rot=(1,0,0;1.5708rad)
  Profile = -> Sketch042
  ReferenceAxis = -> Sketch042 [V_Axis]
  Refine = true
  Reversed = true
FEATURE [PartDesign::Fillet] Fillet002
  Base = -> Revolution [Edge7]
  BaseFeature = -> Revolution
  Placement = pos=(0,0,0) rot=(1,0,0;1.5708rad)
  Radius = 2.9
  Refine = true
  SupportTransform = false
FEATURE [PartDesign::Fillet] Fillet003
  Base = -> Fillet002 [Edge3]
  BaseFeature = -> Fillet002
  Placement = pos=(0,0,0) rot=(1,0,0;1.5708rad)
  Radius = 2
  Refine = true
  SupportTransform = false
FEATURE [Sketcher::SketchObject] Sketch043
  AttachmentOffset = pos=(0,0,-60) rot=(0,0,1;0rad)
  FullyConstrained = true
  MapMode = 5
  Placement = pos=(0,0,-60) rot=(0,0,1;0rad)
  Support = -> [XY_Plane008]
  expr: Constraints[2] = <<sho>>.B3
  expr: Constraints[3] = <<sho>>.B3 + <<sho>>.B4 * 2
  expr: .AttachmentOffset.Base.z = -<<sho>>.D7
  sketch-geometry (2):
    g0: Circle CenterX=0 CenterY=0 CenterZ=0 NormalX=0 NormalY=0 NormalZ=1 AngleXU=0 Radius=91
    g1: Circle CenterX=0 CenterY=0 CenterZ=0 NormalX=0 NormalY=0 NormalZ=1 AngleXU=0 Radius=96
  constraints (4):
    c: Coincident(g0,g-1)
    c: Coincident(g1,g0)
    c: Diameter(g0) = 182
    c: Diameter(g1) = 192
FEATURE [PartDesign::Pad] Pad012  label="mid_part"
  BaseFeature = -> Fillet003
  Direction = (1,1,1)
  Length = 58.5
  Length2 = 100
  Placement = pos=(0,0,0) rot=(1,0,0;1.5708rad)
  Profile = -> Sketch043
  Refine = true
  Reversed = true
  Type = 0
  expr: Length = <<sho>>.B5
FEATURE [Sketcher::SketchObject] Sketch044
  AttachmentOffset = pos=(0,-118.5,0) rot=(0,0,1;0rad)
  FullyConstrained = true
  MapMode = 5
  Placement = pos=(0,2.63e-14,-118.5) rot=(1,0,0;1.5708rad)
  Support = -> [XZ_Plane008]
  expr: .AttachmentOffset.Base.y = -<<sho>>.B5 - <<sho>>.D7
  expr: Constraints[3] = <<sho>>.B3 / 2
  expr: Constraints[4] = <<sho>>.B4
  expr: Constraints[5] = <<sho>>.B3 / 2 + <<sho>>.B6
  expr: Constraints[10] = -<<sho>>.D6 / 2
  expr: Constraints[6] = -<<sho>>.D6
  expr: Constraints[9] = <<sho>>.B4
  expr: Constraints[18] = <<sho>>.B4
  sketch-geometry (10):
    g0: GeomPoint X=91 Y=2.47e-14 Z=0
    g1: LineSegment StartX=91 StartY=2.47e-14 StartZ=0 EndX=96 EndY=2.47e-14 EndZ=0
    g2: GeomPoint X=99 Y=-80 Z=0
    g3: LineSegment StartX=99 StartY=-80 StartZ=0 EndX=104 EndY=-80 EndZ=0
    g4: GeomPoint X=95 Y=-40 Z=0
    g5: ArcOfCircle CenterX=-103 CenterY=-80 CenterZ=0 NormalX=0 NormalY=0 NormalZ=1 AngleXU=0 Radius=202 StartAngle=-9e-16 EndAngle=0.199337
    g6: ArcOfCircle CenterX=293 CenterY=0 CenterZ=0 NormalX=0 NormalY=0 NormalZ=1 AngleXU=0 Radius=202 StartAngle=3.14159 EndAngle=3.34093
    g7: GeomPoint X=100 Y=-40 Z=0
    g8: ArcOfCircle CenterX=-98 CenterY=-80 CenterZ=0 NormalX=0 NormalY=0 NormalZ=1 AngleXU=0 Radius=202 StartAngle=1.8e-15 EndAngle=0.199337
    g9: ArcOfCircle CenterX=298 CenterY=0 CenterZ=0 NormalX=0 NormalY=0 NormalZ=1 AngleXU=0 Radius=202 StartAngle=3.14159 EndAngle=3.34093
  constraints (24):
    c: PointOnObject(g0,g-1)
    c: Coincident(g1,g0)
    c: Horizontal(g1)
    c: DistanceX(g1) = 91
    c: DistanceX(g1,g1) = 5
    c: DistanceX(g2) = 99
    c: DistanceY(g2) = -80
    c: Coincident(g3,g2)
    c: Horizontal(g3)
    c: DistanceX(g3,g3) = 5
    c: DistanceY(g4) = -40
    c: Coincident(g5,g4)
    c: Coincident(g5,g3)
    c: Coincident(g6,g1)
    c: Tangent(g6,g5) = 1.5708
    c: Perpendicular(g5,g3)
    c: Perpendicular(g6,g1)
    c: DistanceY(g5,g7) = 0
    c: DistanceX(g5,g7) = 5
    c: Coincident(g8,g7)
    c: Coincident(g8,g3)
    c: Coincident(g9,g1)
    c: Tangent(g9,g8) = 1.5708
    c: Perpendicular(g9,g1)
FEATURE [PartDesign::Revolution] Revolution001  label="outlet"
  Angle = 360
  Axis = (0,-2e-16,1)
  Base = (0,2.63e-14,-118.5)
  BaseFeature = -> Pad012
  Placement = pos=(0,0,0) rot=(1,0,0;1.5708rad)
  Profile = -> Sketch044
  ReferenceAxis = -> Sketch044 [V_Axis]
  Refine = true
  Reversed = true
FEATURE [PartDesign::Body] Body006  label="SHO"
  Group = -> [Sketch042,Revolution,Fillet002,Fillet003,Sketch043,Pad012,Sketch044,Revolution001]
  Origin = -> Origin008
  Placement = pos=(0,0,37) rot=(0,0,1;0rad)
  Tip = -> Revolution001
FEATURE [Part::FeaturePython] Clone004  label="plug-sta-inf003"  # Draft clone (typed FeaturePython)
  AttacherType = Attacher::AttachEngine3D
  Fuse = false
  Objects = -> [Body003]
  Placement = pos=(0,-8,-160.4) rot=(0,0,1;1.5708rad)
  Scale = (1,1,1)
  expr: .Placement.Base.z = -<<sta>>.B8 - 2 * <<sta>>.B3 - <<sta>>.B5 + <<plug>>.B8
  expr: .Placement.Base.y = -<<sho>>.B6
FEATURE [Sketcher::SketchObject] Sketch045
  FullyConstrained = false
  MapMode = 5
  Support = -> [XY_Plane009]
  sketch-geometry (1):
    g0: Circle CenterX=0 CenterY=0 CenterZ=0 NormalX=0 NormalY=0 NormalZ=1 AngleXU=0 Radius=3.3078
  constraints (1):
    c: Coincident(g0,g-1)
FEATURE [Sketcher::SketchObject] Sketch046
  FullyConstrained = true
  MapMode = 5
  Placement = pos=(0,0,0) rot=(1,0,0;1.5708rad)
  Support = -> [XZ_Plane009]
  expr: Constraints[2] = <<sta>>.B3
  expr: Constraints[1] = <<sta>>.B3 / 2
  sketch-geometry (1):
    g0: Circle CenterX=0 CenterY=5.1 CenterZ=0 NormalX=0 NormalY=0 NormalZ=1 AngleXU=0 Radius=5.1
  constraints (3):
    c: PointOnObject(g0,g-2)
    c: DistanceY(g0) = 5.1
    c: Diameter(g0) = 10.2
FEATURE [Sketcher::SketchObject] Sketch047
  FullyConstrained = true
  MapMode = 5
  Placement = pos=(0,0,0) rot=(0.57735,0.57735,0.57735;2.0944rad)
  Support = -> [YZ_Plane009]
  expr: Constraints[2] = <<sta>>.B3 * 1.5 + <<sta>>.B5
  expr: Constraints[1] = <<sta>>.B3
  sketch-geometry (1):
    g0: Circle CenterX=0 CenterY=17.3 CenterZ=0 NormalX=0 NormalY=0 NormalZ=1 AngleXU=0 Radius=5.1
  constraints (3):
    c: PointOnObject(g0,g-2)
    c: Diameter(g0) = 10.2
    c: DistanceY(g0) = 17.3
FEATURE [PartDesign::Pad] Pad013
  Direction = (1,1,1)
  Length = 118
  Length2 = 132
  Placement = pos=(0,0,0) rot=(0.57735,0.57735,0.57735;2.0944rad)
  Profile = -> Sketch047
  Refine = true
  Type = 4
  expr: Length2 = 250 - (<<sho>>.B3 / 2 + <<sho>>.B4 + <<plug>>.B3 + <<sho>>.B6 - 1)
  expr: Length = <<sho>>.B3 / 2 + <<sho>>.B4 + <<plug>>.B3 + <<sho>>.B6 - 1
FEATURE [PartDesign::Pad] Pad015
  BaseFeature = -> Pad013
  Direction = (1,1,1)
  Length = 17
  Length2 = 100
  Placement = pos=(0,0,0) rot=(0.57735,0.57735,0.57735;2.0944rad)
  Profile = -> Sketch045
  Refine = true
  Type = 0
FEATURE [PartDesign::Pad] Pad014
  BaseFeature = -> Pad015
  Direction = (1,1,1)
  Length = 119
  Length2 = 132
  Placement = pos=(0,0,0) rot=(0.57735,0.57735,0.57735;2.0944rad)
  Profile = -> Sketch046
  Refine = true
  Type = 4
  expr: Length2 = 250 - (<<sho>>.B3 / 2 + <<sho>>.B4 + <<plug>>.B3 + <<sho>>.B6 - 1)
  expr: Length = <<sho>>.B3 / 2 + <<sho>>.B4 + <<plug>>.B3 + <<sho>>.B6
FEATURE [PartDesign::Body] Body007  label="carbon_tube_l250"
  Group = -> [Sketch047,Pad013,Sketch045,Pad015,Sketch046,Pad014]
  Origin = -> Origin009
  Placement = pos=(0,0,-157.4) rot=(0,0,1;3.14159rad)
  Tip = -> Pad014
  expr: .Placement.Base.z = -<<sta>>.B8 - 2 * <<sta>>.B3 - <<sta>>.B5
FEATURE [Sketcher::SketchObject] Sketch048
  FullyConstrained = true
  MapMode = 5
  Support = -> [XY_Plane010]
  expr: Constraints[6] = <<sta>>.B3 + 2 * <<plug>>.B4
  expr: Constraints[5] = <<sho>>.B4 + <<plug>>.B3 + <<plug>>.B5
  expr: Constraints[4] = -<<sho>>.B3 / 2
  sketch-geometry (4):
    g0: LineSegment StartX=-91 StartY=-8.1 StartZ=0 EndX=-114 EndY=-8.1 EndZ=0
    g1: LineSegment StartX=-114 StartY=-8.1 StartZ=0 EndX=-114 EndY=8.1 EndZ=0
    g2: LineSegment StartX=-114 StartY=8.1 StartZ=0 EndX=-91 EndY=8.1 EndZ=0
    g3: ArcOfCircle CenterX=0 CenterY=0 CenterZ=0 NormalX=0 NormalY=0 NormalZ=1 AngleXU=0 Radius=91.3598 StartAngle=3.05282 EndAngle=3.23037
  constraints (11):
    c: Coincident(g0,g1)
    c: Coincident(g1,g2)
    c: Horizontal(g0)
    c: Horizontal(g2)
    c: DistanceX(g2) = -91
    c: DistanceX(g2,g2) = 23
    c: DistanceY(g1,g1) = 16.2
    c: Symmetric(g1,g0,g-1)
    c: Coincident(g3,g-1)
    c: Coincident(g3,g0)
    c: Coincident(g3,g2)
FEATURE [PartDesign::Pad] Pad016
  Direction = (1,1,1)
  Length = 16.2
  Length2 = 18
  Profile = -> Sketch048
  Refine = true
  Type = 4
  expr: Length2 = <<plug>>.E6
  expr: Length = <<plug>>.B4 * 2 + <<sta>>.B3
FEATURE [Sketcher::SketchObject] Sketch049
  FullyConstrained = false
  MapMode = 5
  Placement = pos=(0,0,0) rot=(1,0,0;1.5708rad)
  Support = -> [XZ_Plane010]
  expr: Constraints[8] = 90° - <<plug>>.B6
  expr: Constraints[5] = <<plug>>.E6
  expr: Constraints[2] = -(<<sho>>.B3 / 2 + <<sho>>.B4)
  sketch-geometry (7):
    g0: GeomPoint X=-114 Y=0 Z=0
    g1: GeomPoint X=-96 Y=0 Z=0
    g2: LineSegment StartX=-96 StartY=-18 StartZ=0 EndX=-114 EndY=0 EndZ=0
    g3: LineSegment StartX=-122.918 StartY=-18 StartZ=0 EndX=-96 EndY=-18 EndZ=0
    g4: LineSegment StartX=-114 StartY=0 StartZ=0 EndX=-114 EndY=27.4578 EndZ=0
    g5: LineSegment StartX=-122.918 StartY=-18 StartZ=0 EndX=-122.918 EndY=27.4578 EndZ=0
    g6: LineSegment StartX=-122.918 StartY=27.4578 StartZ=0 EndX=-114 EndY=27.4578 EndZ=0
  constraints (16):
    c: PointOnObject(g0,g-1)
    c: PointOnObject(g1,g-1)
    c: DistanceX(g1) = -96
    c: Coincident(g2,g0)
    c: DistanceX(g2,g1) = 0
    c: DistanceY(g2,g1) = 18
    c: Coincident(g3,g2)
    c: Horizontal(g3)
    c: Angle(g2,g3) = 0.785398
    c: Coincident(g4,g2)
    c: Vertical(g4)
    c: Coincident(g5,g3)
    c: Vertical(g5)
    c: Coincident(g6,g5)
    c: Coincident(g6,g4)
    c: Horizontal(g6)
FEATURE [PartDesign::Groove] Groove001
  Angle = 360
  Axis = (0,-2e-16,1)
  Base = (0,0,0)
  BaseFeature = -> Pad016
  Profile = -> Sketch049
  ReferenceAxis = -> Sketch049 [V_Axis]
  Refine = true
  Reversed = true
FEATURE [PartDesign::Fillet] Fillet004
  Base = -> Groove001 [Edge12]
  BaseFeature = -> Groove001
  Radius = 3
  Refine = true
  SupportTransform = false
FEATURE [PartDesign::Body] Body008  label="plug-sta-inf-ferme"
  Group = -> [Sketch048,Pad016,Sketch049,Groove001,Fillet004]
  Origin = -> Origin010
  Placement = pos=(0,0,-3) rot=(0,0,-1;1.5708rad)
  Tip = -> Fillet004
  expr: .Placement.Base.z = <<plug>>.B8
FEATURE [Part::FeaturePython] Clone  label="plug-sta-inf-ferme001"  # Draft clone (typed FeaturePython)
  AttacherType = Attacher::AttachEngine3D
  Fuse = false
  Objects = -> [Body008]
  Placement = pos=(0,8,-160.4) rot=(0,0,-1;1.5708rad)
  Scale = (1,1,1)
  expr: .Placement.Base.z = -<<sta>>.B8 - 2 * <<sta>>.B3 - <<sta>>.B5 + <<plug>>.B8
  expr: .Placement.Base.y = <<sho>>.B6
FEATURE [Part::FeaturePython] Clone008  label="plug-sta-sup-ferme002"  # Draft clone (typed FeaturePython)
  AttacherType = Attacher::AttachEngine3D
  Fuse = false
  Objects = -> [Body008]
  Placement = pos=(-1.5,0,9.2) rot=(0,0,1;0rad)
  Scale = (1,1,1)
  expr: .Placement.Base.z = <<plug>>.B9
FEATURE [Part::FeaturePython] Clone009  label="plug-sta-sup-ferme003"  # Draft clone (typed FeaturePython)
  AttacherType = Attacher::AttachEngine3D
  Fuse = false
  Objects = -> [Clone008]
  Placement = pos=(-7,0,-148.2) rot=(0,0,1;0rad)
  Scale = (1,1,1)
  expr: .Placement.Base.z = -<<sta>>.B8 - 2 * <<sta>>.B3 - <<sta>>.B5 + <<plug>>.B9
  expr: .Placement.Base.x = -<<sho>>.B6 + 1
FEATURE [Part::FeaturePython] Clone010  label="plug-sta-sup-ouvert001"  # Draft clone (typed FeaturePython)
  AttacherType = Attacher::AttachEngine3D
  Fuse = false
  Objects = -> [Body003]
  Placement = pos=(1.5,0,9.2) rot=(0,0,1;3.14159rad)
  Scale = (1,1,1)
  expr: .Placement.Base.z = <<plug>>.B9
FEATURE [Part::FeaturePython] Clone011  label="plug-sta-sup-ouvert002"  # Draft clone (typed FeaturePython)
  AttacherType = Attacher::AttachEngine3D
  Fuse = false
  Objects = -> [Clone010]
  Placement = pos=(7,0,-148.2) rot=(0,0,1;3.14159rad)
  Scale = (1,1,1)
  expr: .Placement.Base.z = -<<sta>>.B8 - 2 * <<sta>>.B3 - <<sta>>.B5 + <<plug>>.B9
  expr: .Placement.Base.x = <<sho>>.B6 - 1
FEATURE [Sketcher::SketchObject] Sketch050
  FullyConstrained = false
  MapMode = 5
  Support = -> [XY_Plane011]
  sketch-geometry (1):
    g0: Circle CenterX=0 CenterY=0 CenterZ=0 NormalX=0 NormalY=0 NormalZ=1 AngleXU=0 Radius=163.956
  constraints (1):
    c: Coincident(g0,g-1)
FEATURE [PartDesign::Pad] Pad017
  Direction = (1,1,1)
  Length = 26
  Length2 = 100
  Profile = -> Sketch050
  Refine = true
  Reversed = true
  Type = 0
FEATURE [PartDesign::Body] Body009  label="dif-bottom-sho"
  Group = -> [Sketch050,Pad017]
  Origin = -> Origin011
  Placement = pos=(0,0,-161.5) rot=(0,0,1;0rad)
  Tip = -> Pad017
FEATURE [App::Part] Part002  label="plug_outlet"
  Group = -> [Body007,Clone004,Clone,Clone009,Clone011]
  Origin = -> Origin012
FEATURE [App::Part] Part003  label="plug_inlet"
  Group = -> [Clone010,Clone008,Body008,Body,Body003]
  Origin = -> Origin013
FEATURE [Spreadsheet::Sheet] Spreadsheet004  label="aux"
  cells = A1=DONNEES POUR LES MOTEURS AUXILIAIRES; A2=Diam helice aux; B2=78; C2=(hq prop 3x4x3 V1S); A3=Diam tube carbon; B3=10.25; A4=Epaisseur autour carbon; B4=3; A5=longueur support; B5=45; A7=overangle; B7==45deg; A8=pad length overangle; B8==(<<sho>>.B4 + B3 + B4) / tan(B7); A9=largeur renfort; B9=2; A11=longueur min tube carbone; B11==(<<sho>>.B3 / 2 + <<sho>>.B4 + B3 / 2 + B4 / 2) * tan(45°) + 8.5
FEATURE [Sketcher::SketchObject] Sketch051
  FullyConstrained = true
  MapMode = 5
  Support = -> [XY_Plane015]
  expr: Constraints[1] = <<sho>>.B3 + 2 * <<aux>>.B2
  sketch-geometry (1):
    g0: Circle CenterX=0 CenterY=0 CenterZ=0 NormalX=0 NormalY=0 NormalZ=1 AngleXU=0 Radius=169
  constraints (2):
    c: Coincident(g0,g-1)
    c: Diameter(g0) = 338
FEATURE [PartDesign::Pad] Pad018
  Direction = (1,1,1)
  Length = 1
  Length2 = 100
  Profile = -> Sketch051
  Refine = true
  Reversed = true
  Type = 0
FEATURE [PartDesign::Body] Body010
  Group = -> [Sketch051,Pad018]
  Origin = -> Origin015
  Placement = pos=(0,0,-67.5) rot=(0,0,1;0rad)
  Tip = -> Pad018
  expr: .Placement.Base.z = -<<sta>>.E2 - <<sta>>.B7 / 2
FEATURE [Sketcher::SketchObject] Sketch052
  FullyConstrained = true
  MapMode = 5
  Support = -> [XY_Plane016]
  expr: Constraints[9] = <<aux>>.B5
  expr: Constraints[8] = -(<<sho>>.B3 / 2 + <<sho>>.B4 + <<aux>>.B3 + <<aux>>.B4)
  expr: Constraints[1] = <<sho>>.B3
  sketch-geometry (4):
    g0: ArcOfCircle CenterX=0 CenterY=0 CenterZ=0 NormalX=0 NormalY=0 NormalZ=1 AngleXU=0 Radius=91 StartAngle=4.46255 EndAngle=4.96223
    g1: LineSegment StartX=-22.5 StartY=-88.1745 StartZ=0 EndX=-22.5 EndY=-109.25 EndZ=0
    g2: LineSegment StartX=22.5 StartY=-88.1745 StartZ=0 EndX=22.5 EndY=-109.25 EndZ=0
    g3: LineSegment StartX=-22.5 StartY=-109.25 StartZ=0 EndX=22.5 EndY=-109.25 EndZ=0
  constraints (11):
    c: Coincident(g0,g-1)
    c: Diameter(g0) = 182
    c: Coincident(g1,g0)
    c: Vertical(g1)
    c: Coincident(g2,g0)
    c: Vertical(g2)
    c: Coincident(g3,g1)
    c: Coincident(g2,g3)
    c: DistanceY(g2) = -109.25
    c: DistanceX(g3,g3) = 45
    c: Symmetric(g1,g2,g-2)
FEATURE [PartDesign::Pad] Pad019
  Direction = (1,1,1)
  Length = 16.25
  Length2 = 18.25
  Profile = -> Sketch052
  Refine = true
  Reversed = true
  Type = 4
  expr: Length2 = <<aux>>.B8
  expr: Length = <<aux>>.B3 + 2 * <<aux>>.B4
FEATURE [Sketcher::SketchObject] Sketch053
  FullyConstrained = false
  MapMode = 5
  Placement = pos=(0,0,0) rot=(0.57735,0.57735,0.57735;2.0944rad)
  Support = -> [YZ_Plane016]
  expr: Constraints[8] = <<aux>>.B3 + <<aux>>.B4 + <<sho>>.B4
  expr: Constraints[6] = <<aux>>.B7
  expr: Constraints[5] = -<<sho>>.B3 / 2
  sketch-geometry (8):
    g0: GeomPoint X=-91 Y=0 Z=0
    g1: GeomPoint X=-109.25 Y=0 Z=0
    g2: LineSegment StartX=-109.25 StartY=0 StartZ=0 EndX=-91 EndY=-18.25 EndZ=0
    g3: LineSegment StartX=-91 StartY=-18.25 StartZ=0 EndX=-110.868 EndY=-18.25 EndZ=0
    g4: LineSegment StartX=-129.166 StartY=0 StartZ=0 EndX=-129.166 EndY=-18.25 EndZ=0
    g5: LineSegment StartX=-129.166 StartY=-18.25 StartZ=0 EndX=-110.868 EndY=-18.25 EndZ=0
    g6: LineSegment StartX=-109.25 StartY=0 StartZ=0 EndX=-124.877 EndY=15.6268 EndZ=0
    g7: LineSegment StartX=-124.877 StartY=15.6268 StartZ=0 EndX=-129.166 EndY=0 EndZ=0
  constraints (17):
    c: PointOnObject(g0,g-1)
    c: PointOnObject(g1,g-1)
    c: Coincident(g2,g1)
    c: Coincident(g3,g2)
    c: Horizontal(g3)
    c: DistanceX(g0) = -91
    c: Angle(g2,g3) = 0.785398
    c: DistanceX(g2,g0) = 0
    c: DistanceX(g2,g0) = 18.25
    c: PointOnObject(g4,g-1)
    c: Vertical(g4)
    c: Coincident(g5,g4)
    c: Coincident(g5,g3)
    c: Horizontal(g5)
    c: Coincident(g7,g6)
    c: Coincident(g7,g4)
    c: Tangent(g6,g2) = 1.5708
FEATURE [Sketcher::SketchObject] Sketch054
  FullyConstrained = true
  MapMode = 5
  Placement = pos=(0,0,0) rot=(0.57735,0.57735,0.57735;2.0944rad)
  Support = -> [YZ_Plane016]
  expr: Constraints[2] = <<aux>>.B3 / 2 + <<aux>>.B4
  expr: Constraints[1] = -<<sho>>.B3 / 2 - <<sho>>.B4 - <<aux>>.B3 / 2
  expr: Constraints[0] = <<aux>>.B3
  sketch-geometry (1):
    g0: Circle CenterX=-101.125 CenterY=8.125 CenterZ=0 NormalX=0 NormalY=0 NormalZ=1 AngleXU=0 Radius=5.125
  constraints (3):
    c: Diameter(g0) = 10.25
    c: DistanceX(g0) = -101.125
    c: DistanceY(g0) = 8.125
FEATURE [PartDesign::Groove] Groove002
  Angle = 360
  Axis = (-3e-16,3e-16,1)
  Base = (0,0,0)
  BaseFeature = -> Pad019
  Profile = -> Sketch053
  ReferenceAxis = -> Z_Axis016
  Refine = true
  Reversed = true
FEATURE [PartDesign::Pocket] Pocket028  label="carbon_tube002"
  BaseFeature = -> Groove002
  Length = 5
  Length2 = 100
  Midplane = true
  Profile = -> Sketch054
  Refine = true
  Type = 1
FEATURE [Sketcher::SketchObject] Sketch055
  AttachmentOffset = pos=(0,0,0) rot=(0,0,1;1.5708rad)
  FullyConstrained = true
  MapMode = 5
  Placement = pos=(0,0,0) rot=(0,0,1;1.5708rad)
  Support = -> [XY_Plane016]
  expr: Constraints[2] = -<<sho>>.B3 / 2 - <<sho>>.B4 - <<aux>>.B3 / 2
  expr: Constraints[1] = <<screw>>.B4
  sketch-geometry (1):
    g0: Circle CenterX=-101.125 CenterY=0 CenterZ=0 NormalX=0 NormalY=0 NormalZ=1 AngleXU=0 Radius=1.625
  constraints (3):
    c: PointOnObject(g0,g-1)
    c: Diameter(g0) = 3.25
    c: DistanceX(g0) = -101.125
FEATURE [PartDesign::Pocket] Pocket029  label="screw_hole"
  BaseFeature = -> Pocket028
  Length = 5
  Length2 = 100
  Midplane = true
  Profile = -> Sketch055
  Refine = true
  Type = 1
FEATURE [Sketcher::SketchObject] Sketch056
  AttachmentOffset = pos=(0,0,15.25) rot=(0,0,1;0rad)
  FullyConstrained = true
  MapMode = 5
  Placement = pos=(0,0,15.25) rot=(0,0,1;0rad)
  Support = -> [XY_Plane016]
  expr: .AttachmentOffset.Base.z = <<aux>>.B3 + <<aux>>.B4 + 2
  expr: Constraints[20] = -<<sho>>.B3 / 2 - <<sho>>.B4 - <<aux>>.B3 / 2
  expr: Constraints[19] = <<screw>>.B6
  sketch-geometry (7):
    g0: LineSegment StartX=0 StartY=-97.9496 StartZ=0 EndX=-2.75 EndY=-99.5373 EndZ=0
    g1: LineSegment StartX=-2.75 StartY=-99.5373 StartZ=0 EndX=-2.75 EndY=-102.713 EndZ=0
    g2: LineSegment StartX=-2.75 StartY=-102.713 StartZ=0 EndX=0 EndY=-104.3 EndZ=0
    g3: LineSegment StartX=0 StartY=-104.3 StartZ=0 EndX=2.75 EndY=-102.713 EndZ=0
    g4: LineSegment StartX=2.75 StartY=-102.713 StartZ=0 EndX=2.75 EndY=-99.5373 EndZ=0
    g5: LineSegment StartX=2.75 StartY=-99.5373 StartZ=0 EndX=0 EndY=-97.9496 EndZ=0
    g6: Circle CenterX=0 CenterY=-101.125 CenterZ=0 NormalX=0 NormalY=0 NormalZ=1 AngleXU=0 Radius=3.17543
  constraints (17):
    c: Coincident(g0,g1)
    c: Coincident(g1,g2)
    c: Coincident(g2,g3)
    c: Coincident(g3,g4)
    c: Coincident(g4,g5)
    c: Coincident(g5,g0)
    c: Equal(g0, g1-g5) x5
    c: PointOnObject(g0,g6)
    c: PointOnObject(g1,g6)
    c: PointOnObject(g2,g6)
    c: PointOnObject(g3,g6)
    c: PointOnObject(g4,g6)
    c: PointOnObject(g5,g6)
    c: PointOnObject(g6,g-2)
    c: PointOnObject(g5,g-2)
    c: DistanceX(g1,g3) = 5.5
    c: DistanceY(g6) = -101.125
FEATURE [PartDesign::Pocket] Pocket030  label="nut_hole001"
  BaseFeature = -> Pocket029
  Length = 5
  Length2 = 100
  Profile = -> Sketch056
  Refine = true
  Reversed = true
  Type = 1
FEATURE [Sketcher::SketchObject] Sketch057
  AttachmentOffset = pos=(0,0,-4.5625) rot=(0,0,1;1.5708rad)
  FullyConstrained = true
  MapMode = 5
  Placement = pos=(0,0,-4.5625) rot=(0,0,1;1.5708rad)
  Support = -> [XY_Plane016]
  expr: .AttachmentOffset.Base.z = -<<aux>>.B8 / 4
  expr: Constraints[1] = <<screw>>.B5
  expr: Constraints[2] = -<<sho>>.B3 / 2 - <<sho>>.B4 - <<aux>>.B3 / 2
  sketch-geometry (1):
    g0: Circle CenterX=-101.125 CenterY=0 CenterZ=0 NormalX=0 NormalY=0 NormalZ=1 AngleXU=0 Radius=2.8
  constraints (3):
    c: PointOnObject(g0,g-1)
    c: Diameter(g0) = 5.6
    c: DistanceX(g0) = -101.125
FEATURE [PartDesign::Pocket] Pocket031  label="head_screw_hole"
  BaseFeature = -> Pocket030
  Length = 5
  Length2 = 100
  Profile = -> Sketch057
  Refine = true
  Type = 1
FEATURE [Sketcher::SketchObject] Sketch058
  AttachmentOffset = pos=(0,0,15.25) rot=(0,0,1;0rad)
  FullyConstrained = true
  MapMode = 5
  Placement = pos=(0,0,15.25) rot=(0,0,1;0rad)
  Support = -> [XY_Plane016]
  expr: Constraints[19] = <<screw>>.B6
  expr: Constraints[20] = -<<sho>>.B3 / 2 - <<sho>>.B4 - <<aux>>.B3 / 2
  expr: .AttachmentOffset.Base.z = <<aux>>.B3 + <<aux>>.B4 + 2
  sketch-geometry (8):
    g0: LineSegment StartX=0 StartY=-97.9496 StartZ=0 EndX=-2.75 EndY=-99.5373 EndZ=0
    g1: LineSegment StartX=-2.75 StartY=-99.5373 StartZ=0 EndX=-2.75 EndY=-102.713 EndZ=0
    g2: LineSegment StartX=-2.75 StartY=-102.713 StartZ=0 EndX=0 EndY=-104.3 EndZ=0
    g3: LineSegment StartX=0 StartY=-104.3 StartZ=0 EndX=2.75 EndY=-102.713 EndZ=0
    g4: LineSegment StartX=2.75 StartY=-102.713 StartZ=0 EndX=2.75 EndY=-99.5373 EndZ=0
    g5: LineSegment StartX=2.75 StartY=-99.5373 StartZ=0 EndX=0 EndY=-97.9496 EndZ=0
    g6: Circle CenterX=0 CenterY=-101.125 CenterZ=0 NormalX=0 NormalY=0 NormalZ=1 AngleXU=0 Radius=3.17543
    g7: Circle CenterX=0 CenterY=-101.125 CenterZ=0 NormalX=0 NormalY=0 NormalZ=1 AngleXU=0 Radius=5
  constraints (19):
    c: Coincident(g0,g1)
    c: Coincident(g1,g2)
    c: Coincident(g2,g3)
    c: Coincident(g3,g4)
    c: Coincident(g4,g5)
    c: Coincident(g5,g0)
    c: Equal(g0, g1-g5) x5
    c: PointOnObject(g0,g6)
    c: PointOnObject(g1,g6)
    c: PointOnObject(g2,g6)
    c: PointOnObject(g3,g6)
    c: PointOnObject(g4,g6)
    c: PointOnObject(g5,g6)
    c: PointOnObject(g6,g-2)
    c: PointOnObject(g5,g-2)
    c: DistanceX(g1,g3) = 5.5
    c: DistanceY(g6) = -101.125
    c: Coincident(g7,g6)
    c: Diameter(g7) = 10
FEATURE [Sketcher::SketchObject] Sketch060
  AttachmentOffset = pos=(0,16.25,22.5) rot=(0,0,1;0rad)
  FullyConstrained = false
  MapMode = 5
  Placement = pos=(22.5,-1.4e-15,16.25) rot=(0.57735,0.57735,0.57735;2.0944rad)
  Support = -> [YZ_Plane016]
  expr: .AttachmentOffset.Base.y = <<aux>>.B3 + 2 * <<aux>>.B4
  expr: .AttachmentOffset.Base.z = <<aux>>.B5 / 2
  expr: Constraints[5] = <<aux>>.B3 + 2 * <<aux>>.B4
  expr: Constraints[4] = -(<<sho>>.B3 / 2 + <<sho>>.B4 + <<aux>>.B3 + <<aux>>.B4)
  sketch-geometry (3):
    g0: LineSegment StartX=-92.2646 StartY=0 StartZ=0 EndX=-92.2646 EndY=16.25 EndZ=0
    g1: LineSegment StartX=-109.25 StartY=3.6e-15 StartZ=0 EndX=-92.2646 EndY=0 EndZ=0
    g2: ArcOfCircle CenterX=-115.577 CenterY=23.6155 CenterZ=0 NormalX=0 NormalY=0 NormalZ=1 AngleXU=0 Radius=24.4484 StartAngle=4.97416 EndAngle=5.97716
  constraints (8):
    c: PointOnObject(g0,g-1)
    c: Vertical(g0)
    c: PointOnObject(g1,g-1)
    c: Coincident(g1,g0)
    c: DistanceX(g1) = -109.25
    c: DistanceY(g0,g0) = 16.25
    c: Coincident(g2,g0)
    c: Coincident(g2,g1)
FEATURE [Sketcher::SketchObject] Sketch061
  FullyConstrained = true
  MapMode = 5
  Support = -> [XY_Plane016]
  expr: Constraints[1] = <<sho>>.B3 + <<sho>>.B4 / 2
  sketch-geometry (1):
    g0: Circle CenterX=0 CenterY=0 CenterZ=0 NormalX=0 NormalY=0 NormalZ=1 AngleXU=0 Radius=92.25
  constraints (2):
    c: Coincident(g0,g-1)
    c: Diameter(g0) = 184.5
FEATURE [PartDesign::Pad] Pad020  label="nut_pad"
  BaseFeature = -> Pocket031
  Direction = (1,1,1)
  Length = 5.5
  Length2 = 100
  Profile = -> Sketch058
  Refine = true
  Type = 0
  expr: Length = <<screw>>.B6
FEATURE [PartDesign::Pad] Pad021  label="renfort"
  BaseFeature = -> Pad020
  Direction = (1,1,1)
  Length = 2
  Length2 = 100
  Profile = -> Sketch060
  Refine = true
  Reversed = true
  Type = 0
  expr: Length = <<aux>>.B9
FEATURE [PartDesign::LinearPattern] LinearPattern
  BaseFeature = -> Pad021
  Direction = -> X_Axis016
  Length = 43
  Occurrences = 6
  Originals = -> [Pad021]
  Refine = true
  Reversed = true
  expr: Length = <<aux>>.B5 - <<aux>>.B9
FEATURE [PartDesign::Pocket] Pocket032
  BaseFeature = -> LinearPattern
  Length = 5
  Length2 = 100
  Midplane = true
  Profile = -> Sketch061
  Refine = true
  Type = 1
FEATURE [PartDesign::Body] Body011  label="support-carbon-aux-mot"
  Group = -> [Sketch052,Pad019,Sketch053,Sketch054,Groove002,Pocket028,Sketch055,Pocket029,Sketch056,Pocket030,Sketch057,Pocket031,Sketch058,Sketch060,Sketch061,Pad020,Pad021,LinearPattern,Pocket032]
  Origin = -> Origin016
  Placement = pos=(0,0,-64.5) rot=(0,0,1;0.785398rad)
  Tip = -> Pocket032
  expr: .Placement.Base.z = -<<sta>>.E2 - <<sta>>.B7 / 2 + 3
FEATURE [Part::FeaturePython] Clone012  label="support-carbon-aux-mot001"  # Draft clone (typed FeaturePython)
  AttacherType = Attacher::AttachEngine3D
  Fuse = false
  Objects = -> [Body011]
  Placement = pos=(0,0,-64.5) rot=(0,0,1;3.92699rad)
  Scale = (1,1,1)
  expr: .Placement.Base.z = -<<sta>>.E2 - <<sta>>.B7 / 2 + 3
FEATURE [Sketcher::SketchObject] Sketch062
  FullyConstrained = true
  MapMode = 5
  Placement = pos=(0,0,0) rot=(0.57735,0.57735,0.57735;2.0944rad)
  Support = -> [YZ_Plane017]
  expr: Constraints[2] = -<<sho>>.B3 / 2 - <<sho>>.B4 - <<aux>>.B3 / 2
  expr: Constraints[0] = <<aux>>.B3
  sketch-geometry (1):
    g0: Circle CenterX=-101.125 CenterY=0 CenterZ=0 NormalX=0 NormalY=0 NormalZ=1 AngleXU=0 Radius=5.125
  constraints (3):
    c: Diameter(g0) = 10.25
    c: PointOnObject(g0,g-1)
    c: DistanceX(g0) = -101.125
FEATURE [PartDesign::Pad] Pad022
  Direction = (1,1,1)
  Length = 111.125
  Length2 = 111.125
  Placement = pos=(0,0,0) rot=(0.57735,0.57735,0.57735;2.0944rad)
  Profile = -> Sketch062
  Refine = true
  Type = 4
  expr: Length2 = <<aux>>.B11
  expr: Length = <<aux>>.B11
FEATURE [PartDesign::Body] Body012  label="carbon_tube_aux_mot"
  Group = -> [Sketch062,Pad022]
  Origin = -> Origin017
  Placement = pos=(0,0,-56.375) rot=(0,0,1;0.785398rad)
  Tip = -> Pad022
  expr: .Placement.Base.z = -<<sta>>.E2 - <<sta>>.B7 / 2 + 3 + <<aux>>.B3 / 2 + <<aux>>.B4
FEATURE [Spreadsheet::Sheet] Spreadsheet005  label="batt"
  cells = A1=DONNEES SUR LES BATTERIES; A3=hauteur; B3=162; A4=largeur; B4=40; A5=longueur; B5=45; A7=epaisseur sangle; B7=3; A8=largeur sangle; B8=23; A10=ATTACHE SANGLE; C10=>imprimé séparemment, vient se glisser sur la tube carbone; A11=epaisseur autour carbone; B11=2; A13=pas carbon tube; B13=10; A15=OUTLET BUCKET; A16=epaisseur parois; B16=6.5; A17=hauteur; B17==<<sho>>.D6
FEATURE [Sketcher::SketchObject] Sketch064
  FullyConstrained = false
  MapMode = 5
  Support = -> [XY_Plane020]
  expr: Constraints[20] = <<batt>>.B7 + 3 * <<batt>>.B11
  expr: Constraints[10] = <<batt>>.B8
  expr: Constraints[14] = <<aux>>.B4
  expr: Constraints[9] = <<aux>>.B3 + <<batt>>.B11 * 2
  expr: Constraints[7] = <<batt>>.B7
  expr: Constraints[1] = <<aux>>.B3
  sketch-geometry (12):
    g0: Circle CenterX=0 CenterY=0 CenterZ=0 NormalX=0 NormalY=0 NormalZ=1 AngleXU=0 Radius=5.125
    g1: ArcOfCircle CenterX=-11.5 CenterY=9.625 CenterZ=0 NormalX=0 NormalY=0 NormalZ=1 AngleXU=0 Radius=1.5 StartAngle=1.5708 EndAngle=4.71239
    g2: ArcOfCircle CenterX=11.5 CenterY=9.625 CenterZ=0 NormalX=0 NormalY=0 NormalZ=1 AngleXU=0 Radius=1.5 StartAngle=4.71239 EndAngle=7.85398
    g3: LineSegment StartX=-11.5 StartY=8.125 StartZ=0 EndX=11.5 EndY=8.125 EndZ=0
    g4: LineSegment StartX=-11.5 StartY=11.125 StartZ=0 EndX=11.5 EndY=11.125 EndZ=0
    g5: ArcOfCircle CenterX=0 CenterY=0 CenterZ=0 NormalX=0 NormalY=0 NormalZ=1 AngleXU=0 Radius=7.125 StartAngle=3.07165 EndAngle=6.35312
    g6: GeomPoint X=0 Y=5.125 Z=0
    g7: ArcOfCircle CenterX=11.5 CenterY=9.625 CenterZ=0 NormalX=0 NormalY=0 NormalZ=1 AngleXU=0 Radius=4.5 StartAngle=4.70357 EndAngle=7.85398
    g8: ArcOfCircle CenterX=-11.5 CenterY=9.625 CenterZ=0 NormalX=0 NormalY=0 NormalZ=1 AngleXU=0 Radius=4.5 StartAngle=1.5708 EndAngle=4.72121
    g9: LineSegment StartX=11.5 StartY=14.125 StartZ=0 EndX=-11.5 EndY=14.125 EndZ=0
    g10: ArcOfCircle CenterX=-11.4222 CenterY=0.800164 CenterZ=0 NormalX=0 NormalY=0 NormalZ=1 AngleXU=0 Radius=4.32518 StartAngle=6.21325 EndAngle=7.8628
    g11: ArcOfCircle CenterX=11.4222 CenterY=0.800164 CenterZ=0 NormalX=0 NormalY=0 NormalZ=1 AngleXU=0 Radius=4.32518 StartAngle=1.56198 EndAngle=3.21153
  constraints (26):
    c: Coincident(g0,g-1)
    c: Diameter(g0) = 10.25
    c: Tangent(g1,g4) = 1.5708
    c: Tangent(g1,g3) = -1.5708
    c: Tangent(g3,g2) = -1.5708
    c: Tangent(g4,g2) = 1.5708
    c: Horizontal(g3)
    c: DistanceY(g1,g1) = 3
    c: Coincident(g5,g0)
    c: Diameter(g5) = 14.25
    c: DistanceX(g1,g2) = 23
    c: Symmetric(g1,g2,g-2)
    c: PointOnObject(g6,g0)
    c: PointOnObject(g6,g-2)
    c: DistanceY(g6,g1) = 3
    c: Tangent(g7,g9) = -1.5708
    c: Tangent(g9,g8) = -1.5708
    c: Horizontal(g9)
    c: Coincident(g1,g8)
    c: Coincident(g7,g2)
    c: Diameter(g8) = 9
    c: Tangent(g10,g5) = 1.5708
    c: Tangent(g10,g8) = 1.5708
    c: Tangent(g11,g5) = 1.5708
    c: Tangent(g11,g7) = 1.5708
    c: DistanceY(g5,g5) = 0
FEATURE [PartDesign::Pad] Pad024  label="main_pad"
  Direction = (1,1,1)
  Length = 10
  Length2 = 100
  Profile = -> Sketch064
  Refine = true
  Type = 0
  expr: Length = <<batt>>.B13
FEATURE [Sketcher::SketchObject] Sketch065
  FullyConstrained = true
  MapMode = 5
  Support = -> [XY_Plane020]
  expr: Constraints[3] = <<aux>>.B3 + 2 * <<batt>>.B11
  expr: Constraints[2] = <<aux>>.B3
  sketch-geometry (2):
    g0: Circle CenterX=0 CenterY=0 CenterZ=0 NormalX=0 NormalY=0 NormalZ=1 AngleXU=0 Radius=5.125
    g1: Circle CenterX=0 CenterY=0 CenterZ=0 NormalX=0 NormalY=0 NormalZ=1 AngleXU=0 Radius=7.125
  constraints (4):
    c: Coincident(g0,g-1)
    c: Coincident(g1,g0)
    c: Diameter(g0) = 10.25
    c: Diameter(g1) = 14.25
FEATURE [PartDesign::Pad] Pad025  label="pad_rube_carbone"
  BaseFeature = -> Pad024
  Direction = (1,1,1)
  Length = 10
  Length2 = 100
  Profile = -> Sketch065
  Refine = true
  Type = 0
  expr: Length = <<batt>>.B13
FEATURE [PartDesign::Body] Body014  label="attache-sangle"
  Group = -> [Sketch064,Pad024,Sketch065,Pad025]
  Origin = -> Origin020
  Placement = pos=(88.3883,-54.4472,-56) rot=(0.678598,0.281085,0.678598;3.68962rad)
  Tip = -> Pad025
FEATURE [Part::FeaturePython] Clone013  label="attache-sangle001"  # Draft clone (typed FeaturePython)
  AttacherType = Attacher::AttachEngine3D
  Fuse = false
  Objects = -> [Body014]
  Placement = pos=(54.4472,-88.3883,-56) rot=(-0.678598,-0.281085,0.678598;3.68962rad)
  Scale = (1,1,1)
FEATURE [Sketcher::SketchObject] Sketch067
  FullyConstrained = true
  MapMode = 5
  Placement = pos=(0,0,0) rot=(0.57735,0.57735,0.57735;2.0944rad)
  Support = -> [YZ_Plane021]
  expr: Constraints[11] = <<batt>>.B4
  expr: Constraints[10] = <<batt>>.B3
  expr: Constraints[9] = -(<<sho>>.B3 / 2 + <<sho>>.B4 + <<aux>>.B3 + <<aux>>.B4)
  sketch-geometry (4):
    g0: LineSegment StartX=-109.25 StartY=0 StartZ=0 EndX=-149.25 EndY=0 EndZ=0
    g1: LineSegment StartX=-149.25 StartY=0 StartZ=0 EndX=-149.25 EndY=162 EndZ=0
    g2: LineSegment StartX=-149.25 StartY=162 StartZ=0 EndX=-109.25 EndY=162 EndZ=0
    g3: LineSegment StartX=-109.25 StartY=162 StartZ=0 EndX=-109.25 EndY=0 EndZ=0
  constraints (12):
    c: Coincident(g0,g1)
    c: Coincident(g1,g2)
    c: Coincident(g2,g3)
    c: Coincident(g3,g0)
    c: Horizontal(g0)
    c: Horizontal(g2)
    c: Vertical(g1)
    c: Vertical(g3)
    c: PointOnObject(g0,g-1)
    c: DistanceX(g0) = -109.25
    c: DistanceY(g1,g1) = 162
    c: DistanceX(g0,g0) = 40
FEATURE [PartDesign::Pad] Pad027
  Direction = (1,1,1)
  Length = 45
  Length2 = 100
  Midplane = true
  Placement = pos=(0,0,0) rot=(0.57735,0.57735,0.57735;2.0944rad)
  Profile = -> Sketch067
  Refine = true
  Type = 0
  expr: Length = <<batt>>.B5
FEATURE [PartDesign::Body] Body015  label="sls-6S-batt"
  Group = -> [Sketch067,Pad027]
  Origin = -> Origin021
  Placement = pos=(0,0,-158.5) rot=(0,0,1;0.785398rad)
  Tip = -> Pad027
FEATURE [Sketcher::SketchObject] Sketch069
  FullyConstrained = false
  MapMode = 5
  Placement = pos=(0,0,0) rot=(0.57735,0.57735,0.57735;2.0944rad)
  Support = -> [YZ_Plane022]
  expr: Constraints[10] = <<sho>>.D6 / 2
  expr: Constraints[2] = <<sho>>.D6
  expr: Constraints[4] = -<<sho>>.B3 / 2 - <<sho>>.B6 - (<<sho>>.B4 - <<batt>>.B16)
  expr: Constraints[3] = -<<sho>>.B3 / 2 - (<<sho>>.B4 - <<batt>>.B16)
  sketch-geometry (7):
    g0: ArcOfCircle CenterX=104.5 CenterY=0 CenterZ=0 NormalX=0 NormalY=0 NormalZ=1 AngleXU=0 Radius=202 StartAngle=2.94226 EndAngle=3.14159
    g1: ArcOfCircle CenterX=-291.5 CenterY=80 CenterZ=0 NormalX=0 NormalY=0 NormalZ=1 AngleXU=0 Radius=202 StartAngle=6.08385 EndAngle=6.28319
    g2: LineSegment StartX=-89.5 StartY=80 StartZ=0 EndX=-27.5406 EndY=80 EndZ=0
    g3: LineSegment StartX=-27.5406 StartY=80 StartZ=0 EndX=-27.5406 EndY=0 EndZ=0
    g4: LineSegment StartX=-97.5 StartY=2.47e-14 StartZ=0 EndX=-97.5 EndY=-28.0006 EndZ=0
    g5: LineSegment StartX=-97.5 StartY=-28.0006 StartZ=0 EndX=-27.5406 EndY=-28.0006 EndZ=0
    g6: LineSegment StartX=-27.5406 StartY=-28.0006 StartZ=0 EndX=-27.5406 EndY=0 EndZ=0
  constraints (18):
    c: PointOnObject(g0,g-1)
    c: Tangent(g1,g0) = 1.5708
    c: DistanceY(g1) = 80
    c: DistanceX(g1) = -89.5
    c: DistanceX(g0) = -97.5
    c: Coincident(g2,g1)
    c: Horizontal(g2)
    c: Coincident(g3,g2)
    c: PointOnObject(g3,g-1)
    c: Vertical(g3)
    c: DistanceY(g0) = 40
    c: Perpendicular(g1,g2)
    c: Vertical(g4)
    c: Coincident(g5,g4)
    c: Horizontal(g5)
    c: Coincident(g6,g5)
    c: Tangent(g6,g3) = 1.5708
    c: Tangent(g4,g0) = -1.5708
FEATURE [Sketcher::SketchObject] Sketch070
  FullyConstrained = false
  MapMode = 5
  Support = -> [XY_Plane022]
  expr: Constraints[7] = <<aux>>.B3 + <<aux>>.B4 + <<batt>>.B4 / 2 + <<sho>>.B4 + <<sho>>.B3 / 2
  expr: Constraints[5] = <<batt>>.B5 / 2 + <<batt>>.B16
  expr: Constraints[10] = 2 * <<batt>>.B16
  expr: Constraints[4] = <<aux>>.B3 + <<aux>>.B4 + <<batt>>.B16 + <<batt>>.B4 + <<sho>>.B4
  expr: Constraints[26] = 3 * <<batt>>.B16
  expr: Constraints[1] = <<sho>>.B3
  sketch-geometry (13):
    g0: ArcOfCircle CenterX=0 CenterY=0 CenterZ=0 NormalX=0 NormalY=0 NormalZ=1 AngleXU=0 Radius=91 StartAngle=4.31082 EndAngle=4.71239
    g1: GeomPoint X=0 Y=-91 Z=0
    g2: GeomPoint X=-29 Y=-155.75 Z=0
    g3: GeomPoint X=0 Y=-129.25 Z=0
    g4: ArcOfCircle CenterX=-24.2016 CenterY=-151.365 CenterZ=0 NormalX=0 NormalY=0 NormalZ=1 AngleXU=0 Radius=6.5 StartAngle=2.35619 EndAngle=5.49779
    g5: LineSegment StartX=-28.7978 StartY=-146.769 StartZ=0 EndX=-18.173 EndY=-136.144 EndZ=0
    g6: LineSegment StartX=-19.6054 StartY=-155.961 StartZ=0 EndX=-8.98064 EndY=-145.337 EndZ=0
    g7: LineSegment StartX=0 StartY=-129.25 StartZ=0 EndX=-29 EndY=-155.75 EndZ=0
    g8: ArcOfCircle CenterX=-25.0673 CenterY=-129.25 CenterZ=0 NormalX=0 NormalY=0 NormalZ=1 AngleXU=0 Radius=9.75 StartAngle=5.49779 EndAngle=7.06858
    g9: LineSegment StartX=-18.173 StartY=-122.356 StartZ=0 EndX=-28.7978 EndY=-111.731 EndZ=0
    g10: ArcOfCircle CenterX=-9.26477 CenterY=-92.1978 CenterZ=0 NormalX=0 NormalY=0 NormalZ=1 AngleXU=0 Radius=27.6239 StartAngle=2.83121 EndAngle=3.92699
    g11: ArcOfCircle CenterX=0 CenterY=-154.317 CenterZ=0 NormalX=0 NormalY=0 NormalZ=1 AngleXU=0 Radius=12.7005 StartAngle=1.5708 EndAngle=2.35619
    g12: LineSegment StartX=-1.67e-14 StartY=-91 StartZ=0 EndX=8e-16 EndY=-141.617 EndZ=0
  constraints (32):
    c: Coincident(g0,g-1)
    c: Diameter(g0) = 182
    c: PointOnObject(g1,g0)
    c: PointOnObject(g1,g-2)
    c: DistanceY(g2,g1) = 64.75
    c: DistanceX(g2,g0) = 29
    c: PointOnObject(g3,g-2)
    c: DistanceY(g3,g0) = 129.25
    c: PointOnObject(g2,g4)
    c: PointOnObject(g0,g-2)
    c: Diameter(g4) = 13
    c: Angle(g6) = 0.785398
    c: Equal(g5,g6)
    c: Parallel(g5,g6)
    c: Tangent(g5,g4) = 1.5708
    c: Tangent(g6,g4) = -1.5708
    c: Coincident(g7,g3)
    c: Coincident(g7,g2)
    c: PointOnObject(g4,g7)
    c: Tangent(g8,g5) = -1.5708
    c: Perpendicular(g5,g9)
    c: Tangent(g9,g8) = -1.5708
    c: DistanceY(g3,g8) = 0
    c: Coincident(g10,g0)
    c: Tangent(g10,g9) = 1.5708
    c: Equal(g5,g9)
    c: Diameter(g8) = 19.5
    c: PointOnObject(g11,g-2)
    c: PointOnObject(g11,g-2)
    c: Tangent(g11,g6) = 1.5708
    c: Coincident(g12,g0)
    c: Coincident(g12,g11)
FEATURE [PartDesign::Pad] Pad028  label="bottom_pad"
  Direction = (1,1,1)
  Length = 6.5
  Length2 = 100
  Profile = -> Sketch070
  Refine = true
  Type = 0
  expr: Length = <<batt>>.B16
FEATURE [Sketcher::SketchObject] Sketch072
  AttachmentOffset = pos=(0,0,0) rot=(0,1,0;-0.270526rad)
  FullyConstrained = false
  MapMode = 5
  Placement = pos=(0,0,0) rot=(-0.68097,-0.517822,-0.517822;4.33727rad)
  Support = -> [YZ_Plane022]
  expr: Constraints[9] = <<aux>>.B3 + <<aux>>.B4 + <<sho>>.B4 + <<sho>>.B3 / 2
  expr: Constraints[5] = <<sho>>.D6 / 2
  expr: Constraints[2] = <<sho>>.D6
  expr: Constraints[4] = -<<sho>>.B3 / 2 - <<sho>>.B6 - (<<sho>>.B4 - <<batt>>.B16)
  expr: Constraints[3] = -<<sho>>.B3 / 2 - (<<sho>>.B4 - <<batt>>.B16)
  sketch-geometry (6):
    g0: ArcOfCircle CenterX=104.5 CenterY=0 CenterZ=0 NormalX=0 NormalY=0 NormalZ=1 AngleXU=0 Radius=202 StartAngle=2.94226 EndAngle=3.14159
    g1: ArcOfCircle CenterX=-291.5 CenterY=80 CenterZ=0 NormalX=0 NormalY=0 NormalZ=1 AngleXU=0 Radius=202 StartAngle=6.08385 EndAngle=6.28319
    g2: LineSegment StartX=-97.5 StartY=0 StartZ=0 EndX=-109.25 EndY=0 EndZ=0
    g3: ArcOfCircle CenterX=-19.4881 CenterY=0 CenterZ=0 NormalX=0 NormalY=0 NormalZ=1 AngleXU=0 Radius=89.7619 StartAngle=2.65988 EndAngle=3.14159
    g4: ArcOfCircle CenterX=-172.513 CenterY=80 CenterZ=0 NormalX=0 NormalY=0 NormalZ=1 AngleXU=0 Radius=82.9129 StartAngle=5.80147 EndAngle=6.28319
    g5: LineSegment StartX=-89.5 StartY=80 StartZ=0 EndX=-89.6 EndY=80 EndZ=0
  constraints (19):
    c: PointOnObject(g0,g-1)
    c: Tangent(g1,g0) = 1.5708
    c: DistanceY(g1) = 80
    c: DistanceX(g1) = -89.5
    c: DistanceX(g0) = -97.5
    c: DistanceY(g0) = 40
    c: Coincident(g2,g0)
    c: Horizontal(g2)
    c: Perpendicular(g0,g2)
    c: DistanceX(g2,g-1) = 109.25
    c: Coincident(g3,g2)
    c: Coincident(g5,g1)
    c: Horizontal(g5)
    c: Perpendicular(g1,g5)
    c: DistanceX(g5,g5) = 0.1
    c: Coincident(g5,g4)
    c: Tangent(g4,g3) = 1.5708
    c: Perpendicular(g3,g2)
    c: Perpendicular(g4,g5)
FEATURE [Sketcher::SketchObject] Sketch075
  AttachmentOffset = pos=(0,-129.25,5) rot=(0,0,1;0.785398rad)
  FullyConstrained = true
  MapMode = 5
  Placement = pos=(0,-129.25,5) rot=(0,0,1;0.785398rad)
  Support = -> [XY_Plane022]
  expr: Constraints[16] = <<batt>>.B16 / 2
  expr: .AttachmentOffset.Base.y = -(<<aux>>.B3 + <<aux>>.B4 + <<batt>>.B4 / 2 + <<sho>>.B4 + <<sho>>.B3 / 2)
  expr: Constraints[25] = <<batt>>.B16 / 2
  expr: Constraints[27] = <<batt>>.B5 / 2 - <<batt>>.B16 / 2
  sketch-geometry (12):
    g0: LineSegment StartX=-2 StartY=5.25 StartZ=0 EndX=2 EndY=5.25 EndZ=0
    g1: LineSegment StartX=5.25 StartY=2 StartZ=0 EndX=5.25 EndY=-2 EndZ=0
    g2: LineSegment StartX=2 StartY=-5.25 StartZ=0 EndX=-2 EndY=-5.25 EndZ=0
    g3: LineSegment StartX=-5.25 StartY=-2 StartZ=0 EndX=-5.25 EndY=2 EndZ=0
    g4: ArcOfCircle CenterX=-2 CenterY=2 CenterZ=0 NormalX=0 NormalY=0 NormalZ=1 AngleXU=0 Radius=3.25 StartAngle=1.5708 EndAngle=3.14159
    g5: ArcOfCircle CenterX=-2 CenterY=-2 CenterZ=0 NormalX=0 NormalY=0 NormalZ=1 AngleXU=0 Radius=3.25 StartAngle=3.14159 EndAngle=4.71239
    g6: ArcOfCircle CenterX=2 CenterY=-2 CenterZ=0 NormalX=0 NormalY=0 NormalZ=1 AngleXU=0 Radius=3.25 StartAngle=4.71239 EndAngle=6.28319
    g7: ArcOfCircle CenterX=2 CenterY=2 CenterZ=0 NormalX=0 NormalY=0 NormalZ=1 AngleXU=0 Radius=3.25 StartAngle=0 EndAngle=1.5708
    g8: ArcOfCircle CenterX=11.25 CenterY=0 CenterZ=0 NormalX=0 NormalY=0 NormalZ=1 AngleXU=0 Radius=3.25 StartAngle=1.5708 EndAngle=4.71239
    g9: ArcOfCircle CenterX=19.25 CenterY=4.229e-13 CenterZ=0 NormalX=0 NormalY=0 NormalZ=1 AngleXU=0 Radius=3.25 StartAngle=4.71239 EndAngle=7.85398
    g10: LineSegment StartX=11.25 StartY=-3.25 StartZ=0 EndX=19.25 EndY=-3.25 EndZ=0
    g11: LineSegment StartX=11.25 StartY=3.25 StartZ=0 EndX=19.25 EndY=3.25 EndZ=0
  constraints (28):
    c: Horizontal(g2)
    c: Vertical(g3)
    c: Equal(g3,g0)
    c: Tangent(g0,g4) = 1.5708
    c: Tangent(g3,g4) = 1.5708
    c: Tangent(g2,g5) = 1.5708
    c: Tangent(g3,g5) = 1.5708
    c: Tangent(g1,g6) = 1.5708
    c: Tangent(g2,g6) = 1.5708
    c: Tangent(g0,g7) = 1.5708
    c: Tangent(g1,g7) = 1.5708
    c: Parallel(g0,g-1)
    c: Equal(g4,g7)
    c: Equal(g7,g6)
    c: Symmetric(g3,g1,g-2)
    c: Symmetric(g0,g2,g-1)
    c: Radius(g4) = 3.25
    c: DistanceY(g3,g3) = 4
    c: Tangent(g8,g11) = 1.5708
    c: Tangent(g8,g10) = -1.5708
    c: Tangent(g10,g9) = -1.5708
    c: Tangent(g11,g9) = 1.5708
    c: Horizontal(g10)
    c: Equal(g8,g9)
    c: PointOnObject(g8,g-1)
    c: Radius(g8) = 3.25
    c: DistanceX(g1,g8) = 6
    c: DistanceX(g9) = 19.25
FEATURE [PartDesign::Mirrored] Mirrored001
  BaseFeature = -> Pad028
  MirrorPlane = -> Sketch070 [V_Axis]
  Originals = -> [Pad028]
  Refine = true
FEATURE [PartDesign::Revolution] Revolution002
  Angle = 2
  Axis = (-2e-16,2e-16,1)
  Base = (0,0,0)
  BaseFeature = -> Mirrored001
  Profile = -> Sketch072
  ReferenceAxis = -> Sketch072 [V_Axis]
  Refine = true
FEATURE [PartDesign::PolarPattern] PolarPattern004
  Angle = 29
  Axis = -> Sketch072 [V_Axis]
  BaseFeature = -> Revolution002
  Occurrences = 6
  Originals = -> [Revolution002]
  Refine = true
FEATURE [Sketcher::SketchObject] Sketch076
  AttachmentOffset = pos=(0,0,3) rot=(0,0,1;0rad)
  FullyConstrained = true
  MapMode = 5
  Placement = pos=(0,0,3) rot=(0,0,1;0rad)
  Support = -> [XY_Plane022]
  expr: Constraints[1] = <<sho>>.B3 / 2 + <<sho>>.B4 + <<aux>>.B3 / 2 + 6
  sketch-geometry (1):
    g0: Circle CenterX=0 CenterY=-107.125 CenterZ=0 NormalX=0 NormalY=0 NormalZ=1 AngleXU=0 Radius=3
  constraints (3):
    c: PointOnObject(g0,g-2)
    c: DistanceY(g0,g-1) = 107.125
    c: Diameter(g0) = 6
FEATURE [PartDesign::Pocket] Pocket033  label="passage_tournevis"
  BaseFeature = -> PolarPattern004
  Length = 5
  Length2 = 100
  Midplane = true
  Profile = -> Sketch076
  Refine = true
  Type = 1
FEATURE [PartDesign::Pocket] Pocket034
  BaseFeature = -> Pocket033
  Length = 5
  Length2 = 100
  Midplane = true
  Profile = -> Sketch075
  Refine = true
  Type = 1
FEATURE [PartDesign::Mirrored] Mirrored002
  BaseFeature = -> Pocket034
  MirrorPlane = -> YZ_Plane022
  Originals = -> [Pocket034]
  Refine = true
FEATURE [Sketcher::SketchObject] Sketch077
  FullyConstrained = true
  MapMode = 5
  Placement = pos=(0,0,0) rot=(0.57735,0.57735,0.57735;2.0944rad)
  Support = -> [YZ_Plane023]
  expr: Constraints[8] = <<sta>>.B11 + 1.5
  expr: Constraints[7] = <<sta>>.B11 + 1.5
  expr: Constraints[6] = <<sta>>.B11 / 2 + 1.5
  expr: Constraints[5] = <<sta>>.B11
  sketch-geometry (3):
    g0: Circle CenterX=0 CenterY=4.3 CenterZ=0 NormalX=0 NormalY=0 NormalZ=1 AngleXU=0 Radius=2.8
    g1: Circle CenterX=0 CenterY=11.4 CenterZ=0 NormalX=0 NormalY=0 NormalZ=1 AngleXU=0 Radius=2.8
    g2: Circle CenterX=0 CenterY=18.5 CenterZ=0 NormalX=0 NormalY=0 NormalZ=1 AngleXU=0 Radius=2.8
  constraints (9):
    c: PointOnObject(g0,g-2)
    c: PointOnObject(g1,g-2)
    c: PointOnObject(g2,g-2)
    c: Equal(g2,g1)
    c: Equal(g1,g0)
    c: Diameter(g2) = 5.6
    c: DistanceY(g-1,g0) = 4.3
    c: DistanceY(g0,g1) = 7.1
    c: DistanceY(g1,g2) = 7.1
FEATURE [Sketcher::SketchObject] Sketch078
  FullyConstrained = true
  MapMode = 5
  Placement = pos=(0,0,0) rot=(0.57735,0.57735,0.57735;2.0944rad)
  Support = -> [YZ_Plane023]
  expr: Constraints[9] = 2.5 * <<sta>>.B11 + 3 * 1.5
  expr: Constraints[8] = <<sta>>.B11 / 2 + 1.5
  sketch-geometry (4):
    g0: ArcOfCircle CenterX=0 CenterY=4.3 CenterZ=0 NormalX=0 NormalY=0 NormalZ=1 AngleXU=0 Radius=4.3 StartAngle=3.14159 EndAngle=6.28319
    g1: ArcOfCircle CenterX=-1.129e-13 CenterY=18.5 CenterZ=0 NormalX=0 NormalY=0 NormalZ=1 AngleXU=0 Radius=4.3 StartAngle=9.9e-15 EndAngle=3.14159
    g2: LineSegment StartX=4.3 StartY=4.3 StartZ=0 EndX=4.3 EndY=18.5 EndZ=0
    g3: LineSegment StartX=-4.3 StartY=4.3 StartZ=0 EndX=-4.3 EndY=18.5 EndZ=0
  constraints (10):
    c: Tangent(g0,g3) = 1.5708
    c: Tangent(g0,g2) = -1.5708
    c: Tangent(g2,g1) = -1.5708
    c: Tangent(g3,g1) = 1.5708
    c: Vertical(g2)
    c: Equal(g0,g1)
    c: PointOnObject(g0,g-2)
    c: Tangent(g0,g-1)
    c: DistanceY(g0) = 4.3
    c: DistanceY(g1) = 18.5
FEATURE [PartDesign::Pad] Pad029
  Direction = (1,1,1)
  Length = 7
  Length2 = 100
  Placement = pos=(0,0,0) rot=(0.57735,0.57735,0.57735;2.0944rad)
  Profile = -> Sketch078
  Refine = true
  Type = 0
FEATURE [PartDesign::Pad] Pad030
  BaseFeature = -> Pad029
  Direction = (1,1,1)
  Length = 33
  Length2 = 100
  Placement = pos=(0,0,0) rot=(0.57735,0.57735,0.57735;2.0944rad)
  Profile = -> Sketch077
  Refine = true
  Reversed = true
  Type = 0
FEATURE [PartDesign::Body] Body017  label="passage_bullet_tmotor"
  Group = -> [Sketch077,Sketch078,Pad029,Pad030]
  Origin = -> Origin023
  Placement = pos=(93.5481,14.0165,-4.62484) rot=(0.077998,0.005271,0.99694;3.26476rad)
  Tip = -> Pad030
FEATURE [Part::FeaturePython] Clone015  label="passage_bullet_tmotor001"  # Draft clone (typed FeaturePython)
  AttacherType = Attacher::AttachEngine3D
  Fuse = false
  Objects = -> [Body017]
  Placement = pos=(98.42,17.1129,-156.115) rot=(-0.034738,-0.009693,0.999349;3.29671rad)
  Scale = (1,1,1)
FEATURE [App::Part] Part  label="STA-ADV001"
  Group = -> [Body001,Clone003,Part002,Part003,Body017,Clone015]
  Origin = -> Origin002
FEATURE [Sketcher::SketchObject] Sketch079
  FullyConstrained = true
  MapMode = 5
  Placement = pos=(0,0,0) rot=(0.57735,0.57735,0.57735;2.0944rad)
  Support = -> [YZ_Plane024]
  expr: Constraints[12] = <<sho>>.B12 + 1 + 1
  expr: Constraints[15] = <<sho>>.B13
  expr: Constraints[14] = <<sho>>.B3 / 2 + <<sho>>.B4 - 1
  sketch-geometry (7):
    g0: LineSegment StartX=95 StartY=0 StartZ=0 EndX=95 EndY=-17.7293 EndZ=0
    g1: LineSegment StartX=95 StartY=0 StartZ=0 EndX=101.066 EndY=0 EndZ=0
    g2: LineSegment StartX=101.066 StartY=0 StartZ=0 EndX=101.066 EndY=-1 EndZ=0
    g3: ArcOfCircle CenterX=103.7 CenterY=-5.25 CenterZ=0 NormalX=0 NormalY=0 NormalZ=1 AngleXU=0 Radius=5 StartAngle=2.12561 EndAngle=4.15758
    g4: LineSegment StartX=101.066 StartY=-9.5 StartZ=0 EndX=101.066 EndY=-10.5 EndZ=0
    g5: LineSegment StartX=101.066 StartY=-10.5 StartZ=0 EndX=95 EndY=-17.7293 EndZ=0
    g6: GeomPoint X=98.7 Y=-5.25 Z=0
  constraints (21):
    c: PointOnObject(g0,g-1)
    c: Vertical(g0)
    c: Coincident(g1,g0)
    c: PointOnObject(g1,g-1)
    c: Coincident(g2,g1)
    c: Vertical(g2)
    c: Coincident(g3,g2)
    c: Coincident(g4,g3)
    c: Vertical(g4)
    c: Coincident(g5,g4)
    c: Coincident(g5,g0)
    c: DistanceY(g6,g3) = 0
    c: DistanceX(g0,g6) = 3.7
    c: PointOnObject(g6,g3)
    c: DistanceX(g0) = 95
    c: Diameter(g3) = 10
    c: DistanceX(g3,g2) = 0
    c: DistanceY(g2,g2) = 1
    c: Equal(g4,g2)
    c: Angle(g5,g0) = 0.698132
    c: DistanceY(g6) = -5.25
FEATURE [PartDesign::Revolution] Revolution003
  Angle = 5
  Axis = (-2e-16,3e-16,1)
  Base = (0,0,0)
  Midplane = true
  Placement = pos=(0,0,0) rot=(0.57735,0.57735,0.57735;2.0944rad)
  Profile = -> Sketch079
  ReferenceAxis = -> Sketch079 [V_Axis]
  Refine = true
  Reversed = true
FEATURE [Sketcher::SketchObject] Sketch080
  FullyConstrained = false
  MapMode = 5
  Placement = pos=(0,0,0) rot=(0.57735,0.57735,0.57735;2.0944rad)
  Support = -> [YZ_Plane024]
  expr: Constraints[5] = <<sho>>.B12
  expr: Constraints[0] = <<sho>>.B3 / 2 + <<sho>>.B4
  sketch-geometry (6):
    g0: GeomPoint X=96 Y=-4.5987 Z=0
    g1: ArcOfCircle CenterX=108.737 CenterY=-4.5987 CenterZ=0 NormalX=0 NormalY=0 NormalZ=1 AngleXU=0 Radius=12.7372 StartAngle=2.72575 EndAngle=3.95172
    g2: ArcOfCircle CenterX=108.737 CenterY=-4.5987 CenterZ=0 NormalX=0 NormalY=0 NormalZ=1 AngleXU=0 Radius=11.0372 StartAngle=2.65613 EndAngle=3.86533
    g3: GeomPoint X=97.7 Y=-4.5987 Z=0
    g4: LineSegment StartX=99.9561 StartY=-13.8252 StartZ=0 EndX=100.467 EndY=-11.9074 EndZ=0
    g5: LineSegment StartX=97.0855 StartY=0.54662 StartZ=0 EndX=98.9752 EndY=0.551437 EndZ=0
  constraints (11):
    c: DistanceX(g0) = 96
    c: PointOnObject(g0,g1)
    c: DistanceY(g1,g0) = 0
    c: PointOnObject(g3,g2)
    c: DistanceY(g3,g0) = 0
    c: DistanceX(g0,g3) = 1.7
    c: Coincident(g4,g1)
    c: Coincident(g4,g2)
    c: Coincident(g5,g1)
    c: Coincident(g5,g2)
    c: Coincident(g2,g1)
FEATURE [PartDesign::Pocket] Pocket035
  BaseFeature = -> Revolution003
  Length = 3.8
  Length2 = 100
  Midplane = true
  Placement = pos=(0,0,0) rot=(0.57735,0.57735,0.57735;2.0944rad)
  Profile = -> Sketch080
  Refine = true
  Type = 0
  expr: Length = <<sho>>.B11
FEATURE [PartDesign::Chamfer] Chamfer001
  Angle = 45
  Base = -> Pocket035 [Edge17]
  BaseFeature = -> Pocket035
  ChamferType = 0
  FlipDirection = false
  Placement = pos=(0,0,0) rot=(0.57735,0.57735,0.57735;2.0944rad)
  Refine = true
  Size = 1
  Size2 = 1
  SupportTransform = false
FEATURE [PartDesign::Fillet] Fillet005
  Base = -> Chamfer001 [Edge15]
  BaseFeature = -> Chamfer001
  Placement = pos=(0,0,0) rot=(0.57735,0.57735,0.57735;2.0944rad)
  Radius = 2.2
  Refine = true
  SupportTransform = false
FEATURE [PartDesign::Body] Body018  label="attache-colier-cable"
  Group = -> [Sketch079,Revolution003,Sketch080,Pocket035,Chamfer001,Fillet005]
  Origin = -> Origin024
  Placement = pos=(0,0,-80) rot=(0,0,-1;2.00713rad)
  Tip = -> Fillet005
  expr: .Placement.Base.z = -<<sho>>.D6
FEATURE [Spreadsheet::Sheet] Spreadsheet006  label="payload"
  cells = A1=DONNEES SUR LES FIXATIONS DE LA PAYLOAD; A3=FIXATION PAR QUEUE D'ARRONDE; A4=angle; B4==60deg; A5=overangle; B5==40deg; A6=largeur L1; B6=20; C6=largeur L2; D6=7; E6=largeur totale; F6==B6 + 2 * D6 + 2 * B7 / tan(B4); A7=profondeur P1; B7=8; A8=hauteur; B8==<<sho>>.B5 / 2; A9=jeu; B9=0.15; A10=thickness_platine; B10=4.5; A11=largeur platine; B11=60; A12=espacement-screw-hole-x-axis; B12=24; C12=12; D12=0; A13=espacement-entre-trous-z-axis; B13=15
FEATURE [Sketcher::SketchObject] Sketch083
  FullyConstrained = true
  MapMode = 5
  Support = -> [XY_Plane027]
  expr: Constraints[1] = <<sho>>.B3 + <<sho>>.B4 * 2 - 1
  expr: Constraints[16] = <<sho>>.B3 / 2 + <<sho>>.B4
  expr: Constraints[17] = <<payload>>.B7
  expr: Constraints[18] = <<payload>>.B4
  expr: Constraints[19] = <<payload>>.B4
  expr: Constraints[23] = <<payload>>.D6
  expr: Constraints[20] = <<payload>>.B6
  sketch-geometry (9):
    g0: ArcOfCircle CenterX=0 CenterY=0 CenterZ=0 NormalX=0 NormalY=0 NormalZ=1 AngleXU=0 Radius=95.5 StartAngle=1.34244 EndAngle=1.79915
    g1: LineSegment StartX=-21.6188 StartY=93.0208 StartZ=0 EndX=-21.6188 EndY=104 EndZ=0
    g2: LineSegment StartX=21.6188 StartY=93.0208 StartZ=0 EndX=21.6188 EndY=104 EndZ=0
    g3: LineSegment StartX=-21.6188 StartY=104 StartZ=0 EndX=-10 EndY=104 EndZ=0
    g4: LineSegment StartX=-10 StartY=104 StartZ=0 EndX=-14.6188 EndY=96 EndZ=0
    g5: LineSegment StartX=-14.6188 StartY=96 StartZ=0 EndX=14.6188 EndY=96 EndZ=0
    g6: LineSegment StartX=14.6188 StartY=96 StartZ=0 EndX=10 EndY=104 EndZ=0
    g7: LineSegment StartX=10 StartY=104 StartZ=0 EndX=21.6188 EndY=104 EndZ=0
    g8: GeomPoint X=0 Y=95.5 Z=0
  constraints (24):
    c: Coincident(g0,g-1)
    c: Diameter(g0) = 191
    c: Coincident(g1,g0)
    c: Vertical(g1)
    c: Coincident(g2,g0)
    c: Vertical(g2)
    c: Coincident(g3,g1)
    c: Horizontal(g3)
    c: Coincident(g4,g3)
    c: Coincident(g5,g4)
    c: Horizontal(g5)
    c: Coincident(g6,g5)
    c: Coincident(g7,g6)
    c: Coincident(g7,g2)
    c: PointOnObject(g8,g0)
    c: PointOnObject(g8,g-2)
    c: DistanceY(g4) = 96
    c: DistanceY(g4,g3) = 8
    c: Angle(g3,g4) = 1.0472
    c: Angle(g6,g7) = 1.0472
    c: DistanceX(g3,g6) = 20
    c: Symmetric(g3,g6,g-2)
    c: Symmetric(g1,g2,g-2)
    c: DistanceX(g1,g4) = 7
FEATURE [PartDesign::Pad] Pad033
  Direction = (1,1,1)
  Length = 29.25
  Length2 = 100
  Profile = -> Sketch083
  Refine = true
  Reversed = true
  Type = 0
  expr: Length = <<payload>>.B8
FEATURE [Sketcher::SketchObject] Sketch084
  ExternalGeometry = -> [Pad033]
  FullyConstrained = true
  MapMode = 5
  Placement = pos=(0,0,0) rot=(0.57735,0.57735,0.57735;2.0944rad)
  Support = -> [YZ_Plane027]
  expr: Constraints[0] = -<<payload>>.B8
  expr: Constraints[1] = <<sho>>.B3 / 2 + <<sho>>.B4 + <<payload>>.B7
  expr: Constraints[7] = <<payload>>.B5
  sketch-geometry (4):
    g0: GeomPoint X=104 Y=-29.25 Z=0
    g1: LineSegment StartX=104 StartY=-29.25 StartZ=0 EndX=93.0208 EndY=-29.25 EndZ=0
    g2: LineSegment StartX=93.0208 StartY=-29.25 StartZ=0 EndX=93.0208 EndY=-42.3344 EndZ=0
    g3: LineSegment StartX=93.0208 StartY=-42.3344 StartZ=0 EndX=104 EndY=-29.25 EndZ=0
  constraints (9):
    c: DistanceY(g0) = -29.25
    c: DistanceX(g0) = 104
    c: Coincident(g1,g0)
    c: Coincident(g2,g1)
    c: Vertical(g2)
    c: Coincident(g3,g2)
    c: Coincident(g3,g1)
    c: Angle(g3,g2) = 0.698132
    c: Coincident(g-3,g1)
FEATURE [PartDesign::Pad] Pad034
  BaseFeature = -> Pad033
  Direction = (1,1,1)
  Length = 43.2376
  Length2 = 100
  Midplane = true
  Profile = -> Sketch084
  Refine = true
  Type = 0
  expr: Length = <<payload>>.F6
FEATURE [Sketcher::SketchObject] Sketch085
  AttachmentOffset = pos=(0,0,-1.64) rot=(0,0,1;0rad)
  ExternalGeometry = -> [Pad034]
  FullyConstrained = true
  MapMode = 5
  Placement = pos=(0,102.36,4e-16) rot=(0,0.707107,0.707107;3.14159rad)
  Support = -> [Pad034]
  expr: Constraints[7] = <<screw>>.B6
  expr: Constraints[20] = -<<payload>>.B8 / 3 + <<screw>>.B6 / 2
  expr: Constraints[21] = <<screw>>.B6 / 2 + 1.64
  sketch-geometry (8):
    g0: LineSegment StartX=-19.9788 StartY=0 StartZ=0 EndX=-19.9788 EndY=-5.41229 EndZ=0
    g1: LineSegment StartX=-14.4788 StartY=0 StartZ=0 EndX=-14.4788 EndY=-5.41229 EndZ=0
    g2: LineSegment StartX=-19.9788 StartY=0 StartZ=0 EndX=-14.4788 EndY=0 EndZ=0
    g3: LineSegment StartX=-19.9788 StartY=-5.41229 StartZ=0 EndX=-19.9788 EndY=-8.58771 EndZ=0
    g4: LineSegment StartX=-19.9788 StartY=-8.58771 StartZ=0 EndX=-17.2288 EndY=-10.1754 EndZ=0
    g5: LineSegment StartX=-17.2288 StartY=-10.1754 StartZ=0 EndX=-14.4788 EndY=-8.58771 EndZ=0
    g6: LineSegment StartX=-14.4788 StartY=-8.58771 StartZ=0 EndX=-14.4788 EndY=-5.41229 EndZ=0
    g7: Circle CenterX=-17.2288 CenterY=-7 CenterZ=0 NormalX=0 NormalY=0 NormalZ=1 AngleXU=0 Radius=3.17543
  constraints (22):
    c: PointOnObject(g0,g-1)
    c: Vertical(g0)
    c: PointOnObject(g1,g-1)
    c: Vertical(g1)
    c: Equal(g0,g1)
    c: Coincident(g2,g0)
    c: Coincident(g2,g1)
    c: DistanceX(g2,g2) = 5.5
    c: Coincident(g3,g4)
    c: Coincident(g4,g5)
    c: Coincident(g5,g6)
    c: PointOnObject(g3,g7)
    c: PointOnObject(g4,g7)
    c: PointOnObject(g5,g7)
    c: PointOnObject(g6,g7)
    c: Tangent(g1,g6) = 1.5708
    c: Equal(g3,g4)
    c: Equal(g4,g5)
    c: Equal(g5,g6)
    c: Tangent(g3,g0) = -1.5708
    c: DistanceY(g7) = -7
    c: DistanceX(g-3,g7) = 4.39
FEATURE [Sketcher::SketchObject] Sketch086
  FullyConstrained = true
  MapMode = 5
  Placement = pos=(0,104,0) rot=(0,0.707107,0.707107;3.14159rad)
  expr: Constraints[0] = <<screw>>.B4
  expr: Constraints[1] = -<<payload>>.B8 / 3 + <<screw>>.B6 / 2
  sketch-geometry (1):
    g0: Circle CenterX=-17.229 CenterY=-7 CenterZ=0 NormalX=0 NormalY=0 NormalZ=1 AngleXU=0 Radius=1.625
  constraints (3):
    c: Diameter(g0) = 3.25
    c: DistanceY(g0) = -7
    c: DistanceX(g0) = -17.229
FEATURE [Sketcher::SketchObject] Sketch087
  FullyConstrained = false
  MapMode = 5
  Support = -> [XY_Plane027]
  expr: Constraints[1] = <<sho>>.B3
  expr: Constraints[3] = <<sho>>.B3 + 2 * <<sho>>.B4 - 1
  sketch-geometry (4):
    g0: ArcOfCircle CenterX=0 CenterY=0 CenterZ=0 NormalX=0 NormalY=0 NormalZ=1 AngleXU=0 Radius=91 StartAngle=1.25895 EndAngle=1.87419
    g1: ArcOfCircle CenterX=0 CenterY=0 CenterZ=0 NormalX=0 NormalY=0 NormalZ=1 AngleXU=0 Radius=95.5 StartAngle=1.25895 EndAngle=1.87419
    g2: LineSegment StartX=-28.5313 StartY=91.1384 StartZ=0 EndX=-27.1869 EndY=86.844 EndZ=0
    g3: LineSegment StartX=29.3006 StartY=90.894 StartZ=0 EndX=27.92 EndY=86.6111 EndZ=0
  constraints (10):
    c: Coincident(g0,g-1)
    c: Diameter(g0) = 182
    c: Coincident(g1,g0)
    c: Diameter(g1) = 191
    c: Coincident(g2,g1)
    c: Coincident(g2,g0)
    c: Coincident(g3,g1)
    c: Coincident(g3,g0)
    c: Perpendicular(g0,g3)
    c: Perpendicular(g1,g2)
FEATURE [Sketcher::SketchObject] Sketch088
  FullyConstrained = true
  MapMode = 5
  Placement = pos=(0,0,0) rot=(0.57735,0.57735,0.57735;2.0944rad)
  Support = -> [YZ_Plane030]
  expr: Constraints[7] = <<sta>>.B3 + 1
  expr: Constraints[18] = <<sta>>.B3 / 2 + 2.5
  sketch-geometry (7):
    g0: LineSegment StartX=-7.6 StartY=0 StartZ=0 EndX=-7.6 EndY=-2 EndZ=0
    g1: LineSegment StartX=-7.6 StartY=-2 StartZ=0 EndX=7.6 EndY=-2 EndZ=0
    g2: LineSegment StartX=7.6 StartY=-2 StartZ=0 EndX=7.6 EndY=0 EndZ=0
    g3: Circle CenterX=0 CenterY=5.6 CenterZ=0 NormalX=0 NormalY=0 NormalZ=1 AngleXU=0 Radius=5.6
    g4: ArcOfCircle CenterX=0 CenterY=5.6 CenterZ=0 NormalX=0 NormalY=0 NormalZ=1 AngleXU=0 Radius=7.6 StartAngle=0 EndAngle=3.14159
    g5: LineSegment StartX=-7.6 StartY=0 StartZ=0 EndX=-7.6 EndY=5.6 EndZ=0
    g6: LineSegment StartX=7.6 StartY=0 StartZ=0 EndX=7.6 EndY=5.6 EndZ=0
  constraints (19):
    c: Vertical(g0)
    c: Coincident(g1,g0)
    c: Horizontal(g1)
    c: Coincident(g2,g1)
    c: Vertical(g2)
    c: PointOnObject(g3,g-2)
    c: PointOnObject(g-1,g3)
    c: Diameter(g3) = 11.2
    c: Coincident(g4,g3)
    c: Coincident(g5,g0)
    c: Vertical(g5)
    c: Coincident(g6,g2)
    c: Vertical(g6)
    c: DistanceY(g0,g0) = 2
    c: PointOnObject(g0,g-1)
    c: PointOnObject(g2,g-1)
    c: Tangent(g4,g5) = 1.5708
    c: Tangent(g6,g4) = -1.5708
    c: Radius(g4) = 7.6
FEATURE [PartDesign::Pad] Pad035
  Direction = (1,1,1)
  Length = 240
  Length2 = 100
  Midplane = true
  Placement = pos=(0,0,0) rot=(0.57735,0.57735,0.57735;2.0944rad)
  Profile = -> Sketch088
  Refine = true
  Type = 0
FEATURE [Sketcher::SketchObject] Sketch089
  FullyConstrained = true
  MapMode = 5
  Support = -> [XY_Plane030]
  sketch-geometry (1):
    g0: Circle CenterX=0 CenterY=0 CenterZ=0 NormalX=0 NormalY=0 NormalZ=1 AngleXU=0 Radius=1.75
  constraints (2):
    c: Coincident(g0,g-1)
    c: Diameter(g0) = 3.5
FEATURE [PartDesign::Pocket] Pocket038
  BaseFeature = -> Pad035
  Length = 5
  Length2 = 100
  Midplane = true
  Placement = pos=(0,0,0) rot=(0.57735,0.57735,0.57735;2.0944rad)
  Profile = -> Sketch089
  Refine = true
  Reversed = true
  Type = 1
FEATURE [Sketcher::SketchObject] Sketch090
  AttachmentOffset = pos=(0,0,120) rot=(0,0,1;0rad)
  FullyConstrained = true
  MapMode = 5
  Placement = pos=(120,-2.66e-14,2.66e-14) rot=(0.57735,0.57735,0.57735;2.0944rad)
  Support = -> [YZ_Plane030]
  expr: Constraints[14] = <<sta>>.B3 / 2 + 2.5
  expr: Constraints[16] = <<sta>>.B3 / 2 + 0.5
  sketch-geometry (6):
    g0: LineSegment StartX=-7.6 StartY=0 StartZ=0 EndX=-7.6 EndY=-2 EndZ=0
    g1: LineSegment StartX=-7.6 StartY=-2 StartZ=0 EndX=7.6 EndY=-2 EndZ=0
    g2: LineSegment StartX=7.6 StartY=-2 StartZ=0 EndX=7.6 EndY=0 EndZ=0
    g3: ArcOfCircle CenterX=0 CenterY=5.6 CenterZ=0 NormalX=0 NormalY=0 NormalZ=1 AngleXU=0 Radius=7.6 StartAngle=0 EndAngle=3.14159
    g4: LineSegment StartX=-7.6 StartY=0 StartZ=0 EndX=-7.6 EndY=5.6 EndZ=0
    g5: LineSegment StartX=7.6 StartY=0 StartZ=0 EndX=7.6 EndY=5.6 EndZ=0
  constraints (17):
    c: Vertical(g0)
    c: Coincident(g1,g0)
    c: Horizontal(g1)
    c: Coincident(g2,g1)
    c: Vertical(g2)
    c: Coincident(g4,g0)
    c: Vertical(g4)
    c: Coincident(g5,g2)
    c: Vertical(g5)
    c: DistanceY(g0,g0) = 2
    c: PointOnObject(g0,g-1)
    c: PointOnObject(g2,g-1)
    c: Tangent(g3,g4) = 1.5708
    c: Tangent(g5,g3) = -1.5708
    c: Radius(g3) = 7.6
    c: PointOnObject(g3,g-2)
    c: DistanceY(g3) = 5.6
FEATURE [PartDesign::Pad] Pad036
  BaseFeature = -> Pocket038
  Direction = (1,1,1)
  Length = 2
  Length2 = 100
  Placement = pos=(0,0,0) rot=(0.57735,0.57735,0.57735;2.0944rad)
  Profile = -> Sketch090
  Refine = true
  Type = 0
FEATURE [Sketcher::SketchObject] Sketch091
  FullyConstrained = false
  MapMode = 5
  Placement = pos=(0,0,0) rot=(1,0,0;1.5708rad)
  Support = -> [XZ_Plane030]
  sketch-geometry (4):
    g0: LineSegment StartX=15 StartY=0 StartZ=0 EndX=105 EndY=0 EndZ=0
    g1: LineSegment StartX=105 StartY=0 StartZ=0 EndX=105 EndY=23.3751 EndZ=0
    g2: LineSegment StartX=105 StartY=23.3751 StartZ=0 EndX=15 EndY=23.3751 EndZ=0
    g3: LineSegment StartX=15 StartY=23.3751 StartZ=0 EndX=15 EndY=0 EndZ=0
  constraints (11):
    c: Coincident(g0,g1)
    c: Coincident(g1,g2)
    c: Coincident(g2,g3)
    c: Coincident(g3,g0)
    c: Horizontal(g0)
    c: Horizontal(g2)
    c: Vertical(g1)
    c: Vertical(g3)
    c: PointOnObject(g0,g-1)
    c: DistanceX(g2,g2) = 90
    c: DistanceX(g2) = 15
FEATURE [PartDesign::Pocket] Pocket039
  BaseFeature = -> Pad036
  Length = 5
  Length2 = 100
  Midplane = true
  Placement = pos=(0,0,0) rot=(0.57735,0.57735,0.57735;2.0944rad)
  Profile = -> Sketch091
  Refine = true
  Type = 1
FEATURE [PartDesign::Mirrored] Mirrored005
  BaseFeature = -> Pocket039
  MirrorPlane = -> Sketch091 [V_Axis]
  Originals = -> [Pocket039]
  Placement = pos=(0,0,0) rot=(0.57735,0.57735,0.57735;2.0944rad)
  Refine = true
FEATURE [PartDesign::Body] Body022  label="decoupe_carbon_aux_mot"
  Group = -> [Sketch088,Pad035,Sketch089,Pocket038,Sketch090,Pad036,Sketch091,Pocket039,Mirrored005]
  Origin = -> Origin030
  Tip = -> Mirrored005
FEATURE [Sketcher::SketchObject] Sketch092
  AttachmentOffset = pos=(0,0,127.5) rot=(0,0,1;0rad)
  FullyConstrained = true
  MapMode = 5
  Placement = pos=(127.5,-2.83e-14,2.83e-14) rot=(0.57735,0.57735,0.57735;2.0944rad)
  Support = -> [YZ_Plane031]
  expr: Constraints[16] = <<sta>>.B3 / 2
  expr: Constraints[14] = <<sta>>.B3 / 2 + 2
  expr: .AttachmentOffset.Base.z = 240 - (<<sho>>.B3 / 2 + <<sho>>.B4 + <<plug>>.B3 + 1.5)
  sketch-geometry (6):
    g0: LineSegment StartX=-7.1 StartY=0 StartZ=0 EndX=-7.1 EndY=-2 EndZ=0
    g1: LineSegment StartX=-7.1 StartY=-2 StartZ=0 EndX=7.1 EndY=-2 EndZ=0
    g2: LineSegment StartX=7.1 StartY=-2 StartZ=0 EndX=7.1 EndY=0 EndZ=0
    g3: ArcOfCircle CenterX=0 CenterY=5.1 CenterZ=0 NormalX=0 NormalY=0 NormalZ=1 AngleXU=0 Radius=7.1 StartAngle=1e-16 EndAngle=3.14159
    g4: LineSegment StartX=-7.1 StartY=0 StartZ=0 EndX=-7.1 EndY=5.1 EndZ=0
    g5: LineSegment StartX=7.1 StartY=0 StartZ=0 EndX=7.1 EndY=5.1 EndZ=0
  constraints (17):
    c: Vertical(g0)
    c: Coincident(g1,g0)
    c: Horizontal(g1)
    c: Coincident(g2,g1)
    c: Vertical(g2)
    c: Coincident(g4,g0)
    c: Vertical(g4)
    c: Coincident(g5,g2)
    c: Vertical(g5)
    c: DistanceY(g0,g0) = 2
    c: PointOnObject(g0,g-1)
    c: PointOnObject(g2,g-1)
    c: Tangent(g3,g4) = 1.5708
    c: Tangent(g5,g3) = -1.5708
    c: Radius(g3) = 7.1
    c: PointOnObject(g3,g-2)
    c: DistanceY(g3) = 5.1
FEATURE [Sketcher::SketchObject] Sketch093
  AttachmentOffset = pos=(0,0,127.5) rot=(0,0,1;0rad)
  FullyConstrained = true
  MapMode = 5
  Placement = pos=(127.5,-2.83e-14,2.83e-14) rot=(0.57735,0.57735,0.57735;2.0944rad)
  Support = -> [YZ_Plane031]
  expr: Constraints[18] = <<sta>>.B3 / 2 + 2
  expr: Constraints[7] = <<sta>>.B3
  expr: .AttachmentOffset.Base.z = 240 - (<<sho>>.B3 / 2 + <<sho>>.B4 + <<plug>>.B3 + 1.5)
  sketch-geometry (7):
    g0: LineSegment StartX=-7.1 StartY=0 StartZ=0 EndX=-7.1 EndY=-2 EndZ=0
    g1: LineSegment StartX=-7.1 StartY=-2 StartZ=0 EndX=7.1 EndY=-2 EndZ=0
    g2: LineSegment StartX=7.1 StartY=-2 StartZ=0 EndX=7.1 EndY=0 EndZ=0
    g3: Circle CenterX=0 CenterY=5.1 CenterZ=0 NormalX=0 NormalY=0 NormalZ=1 AngleXU=0 Radius=5.1
    g4: ArcOfCircle CenterX=0 CenterY=5.1 CenterZ=0 NormalX=0 NormalY=0 NormalZ=1 AngleXU=0 Radius=7.1 StartAngle=0 EndAngle=3.14159
    g5: LineSegment StartX=-7.1 StartY=0 StartZ=0 EndX=-7.1 EndY=5.1 EndZ=0
    g6: LineSegment StartX=7.1 StartY=0 StartZ=0 EndX=7.1 EndY=5.1 EndZ=0
  constraints (19):
    c: Vertical(g0)
    c: Coincident(g1,g0)
    c: Horizontal(g1)
    c: Coincident(g2,g1)
    c: Vertical(g2)
    c: PointOnObject(g3,g-2)
    c: PointOnObject(g-1,g3)
    c: Diameter(g3) = 10.2
    c: Coincident(g4,g3)
    c: Coincident(g5,g0)
    c: Vertical(g5)
    c: Coincident(g6,g2)
    c: Vertical(g6)
    c: DistanceY(g0,g0) = 2
    c: PointOnObject(g0,g-1)
    c: PointOnObject(g2,g-1)
    c: Tangent(g4,g5) = 1.5708
    c: Tangent(g6,g4) = -1.5708
    c: Radius(g4) = 7.1
FEATURE [Sketcher::SketchObject] Sketch094
  AttachmentOffset = pos=(107,0,0) rot=(0,0,1;0rad)
  FullyConstrained = true
  MapMode = 5
  Placement = pos=(107,0,0) rot=(0,0,1;0rad)
  Support = -> [XY_Plane031]
  expr: .AttachmentOffset.Base.x = <<sho>>.B3 / 2 + <<sho>>.B4 + <<plug>>.B3 / 2 + 2 + 1.5
  sketch-geometry (1):
    g0: Circle CenterX=0 CenterY=0 CenterZ=0 NormalX=0 NormalY=0 NormalZ=1 AngleXU=0 Radius=1.75
  constraints (2):
    c: Coincident(g0,g-1)
    c: Diameter(g0) = 3.5
FEATURE [PartDesign::Pad] Pad037
  Direction = (1,1,1)
  Length = 3
  Length2 = 38
  Placement = pos=(0,0,0) rot=(0.57735,0.57735,0.57735;2.0944rad)
  Profile = -> Sketch092
  Refine = true
  Type = 0
FEATURE [PartDesign::Pad] Pad038
  BaseFeature = -> Pad037
  Direction = (1,1,1)
  Length = 40
  Length2 = 100
  Placement = pos=(0,0,0) rot=(0.57735,0.57735,0.57735;2.0944rad)
  Profile = -> Sketch093
  Refine = true
  Reversed = true
  Type = 0
FEATURE [PartDesign::Pocket] Pocket040
  BaseFeature = -> Pad038
  Length = 5
  Length2 = 100
  Midplane = true
  Placement = pos=(0,0,0) rot=(0.57735,0.57735,0.57735;2.0944rad)
  Profile = -> Sketch094
  Refine = true
  Type = 1
FEATURE [PartDesign::Body] Body023  label="decoupe_carbon_inlet_sup"
  Group = -> [Sketch093,Sketch094,Sketch092,Pad037,Pad038,Pocket040]
  Origin = -> Origin031
  Tip = -> Pocket040
FEATURE [Sketcher::SketchObject] Sketch095
  AttachmentOffset = pos=(105.5,0,0) rot=(0,0,1;0rad)
  FullyConstrained = true
  MapMode = 5
  Placement = pos=(105.5,0,0) rot=(0,0,1;0rad)
  Support = -> [XY_Plane033]
  expr: .AttachmentOffset.Base.x = +<<sho>>.B3 / 2 + <<sho>>.B4 + <<plug>>.B3 / 2 + 2
  sketch-geometry (1):
    g0: Circle CenterX=0 CenterY=0 CenterZ=0 NormalX=0 NormalY=0 NormalZ=1 AngleXU=0 Radius=1.75
  constraints (2):
    c: Coincident(g0,g-1)
    c: Diameter(g0) = 3.5
FEATURE [Sketcher::SketchObject] Sketch096
  AttachmentOffset = pos=(0,0,129) rot=(0,0,1;0rad)
  FullyConstrained = true
  MapMode = 5
  Placement = pos=(129,-2.86e-14,2.86e-14) rot=(0.57735,0.57735,0.57735;2.0944rad)
  Support = -> [YZ_Plane033]
  expr: .AttachmentOffset.Base.z = 240 - (<<sho>>.B3 / 2 + <<sho>>.B4 + <<plug>>.B3)
  expr: Constraints[7] = <<sta>>.B3
  expr: Constraints[18] = <<sta>>.B3 / 2 + 2
  sketch-geometry (7):
    g0: LineSegment StartX=-7.1 StartY=0 StartZ=0 EndX=-7.1 EndY=-2 EndZ=0
    g1: LineSegment StartX=-7.1 StartY=-2 StartZ=0 EndX=7.1 EndY=-2 EndZ=0
    g2: LineSegment StartX=7.1 StartY=-2 StartZ=0 EndX=7.1 EndY=0 EndZ=0
    g3: Circle CenterX=0 CenterY=5.1 CenterZ=0 NormalX=0 NormalY=0 NormalZ=1 AngleXU=0 Radius=5.1
    g4: ArcOfCircle CenterX=0 CenterY=5.1 CenterZ=0 NormalX=0 NormalY=0 NormalZ=1 AngleXU=0 Radius=7.1 StartAngle=0 EndAngle=3.14159
    g5: LineSegment StartX=-7.1 StartY=0 StartZ=0 EndX=-7.1 EndY=5.1 EndZ=0
    g6: LineSegment StartX=7.1 StartY=0 StartZ=0 EndX=7.1 EndY=5.1 EndZ=0
  constraints (19):
    c: Vertical(g0)
    c: Coincident(g1,g0)
    c: Horizontal(g1)
    c: Coincident(g2,g1)
    c: Vertical(g2)
    c: PointOnObject(g3,g-2)
    c: PointOnObject(g-1,g3)
    c: Diameter(g3) = 10.2
    c: Coincident(g4,g3)
    c: Coincident(g5,g0)
    c: Vertical(g5)
    c: Coincident(g6,g2)
    c: Vertical(g6)
    c: DistanceY(g0,g0) = 2
    c: PointOnObject(g0,g-1)
    c: PointOnObject(g2,g-1)
    c: Tangent(g4,g5) = 1.5708
    c: Tangent(g6,g4) = -1.5708
    c: Radius(g4) = 7.1
FEATURE [Sketcher::SketchObject] Sketch097
  AttachmentOffset = pos=(0,0,129) rot=(0,0,1;0rad)
  FullyConstrained = true
  MapMode = 5
  Placement = pos=(129,-2.86e-14,2.86e-14) rot=(0.57735,0.57735,0.57735;2.0944rad)
  Support = -> [YZ_Plane033]
  expr: .AttachmentOffset.Base.z = 240 - (<<sho>>.B3 / 2 + <<sho>>.B4 + <<plug>>.B3)
  expr: Constraints[14] = <<sta>>.B3 / 2 + 2
  expr: Constraints[16] = <<sta>>.B3 / 2
  sketch-geometry (6):
    g0: LineSegment StartX=-7.1 StartY=0 StartZ=0 EndX=-7.1 EndY=-2 EndZ=0
    g1: LineSegment StartX=-7.1 StartY=-2 StartZ=0 EndX=7.1 EndY=-2 EndZ=0
    g2: LineSegment StartX=7.1 StartY=-2 StartZ=0 EndX=7.1 EndY=0 EndZ=0
    g3: ArcOfCircle CenterX=0 CenterY=5.1 CenterZ=0 NormalX=0 NormalY=0 NormalZ=1 AngleXU=0 Radius=7.1 StartAngle=1e-16 EndAngle=3.14159
    g4: LineSegment StartX=-7.1 StartY=0 StartZ=0 EndX=-7.1 EndY=5.1 EndZ=0
    g5: LineSegment StartX=7.1 StartY=0 StartZ=0 EndX=7.1 EndY=5.1 EndZ=0
  constraints (17):
    c: Vertical(g0)
    c: Coincident(g1,g0)
    c: Horizontal(g1)
    c: Coincident(g2,g1)
    c: Vertical(g2)
    c: Coincident(g4,g0)
    c: Vertical(g4)
    c: Coincident(g5,g2)
    c: Vertical(g5)
    c: DistanceY(g0,g0) = 2
    c: PointOnObject(g0,g-1)
    c: PointOnObject(g2,g-1)
    c: Tangent(g3,g4) = 1.5708
    c: Tangent(g5,g3) = -1.5708
    c: Radius(g3) = 7.1
    c: PointOnObject(g3,g-2)
    c: DistanceY(g3) = 5.1
FEATURE [PartDesign::Pad] Pad040
  Direction = (1,1,1)
  Length = 3
  Length2 = 38
  Placement = pos=(0,0,0) rot=(0.57735,0.57735,0.57735;2.0944rad)
  Profile = -> Sketch097
  Refine = true
  Type = 0
FEATURE [PartDesign::Pad] Pad039
  BaseFeature = -> Pad040
  Direction = (1,1,1)
  Length = 40
  Length2 = 100
  Placement = pos=(0,0,0) rot=(0.57735,0.57735,0.57735;2.0944rad)
  Profile = -> Sketch096
  Refine = true
  Reversed = true
  Type = 0
FEATURE [PartDesign::Pocket] Pocket041
  BaseFeature = -> Pad039
  Length = 5
  Length2 = 100
  Midplane = true
  Placement = pos=(0,0,0) rot=(0.57735,0.57735,0.57735;2.0944rad)
  Profile = -> Sketch095
  Refine = true
  Type = 1
FEATURE [PartDesign::Body] Body025  label="decoupe_carbon_inlet_inf"
  Group = -> [Sketch096,Sketch095,Sketch097,Pad040,Pad039,Pocket041]
  Origin = -> Origin033
  Placement = pos=(0,0,0) rot=(0,0,-1;1.5708rad)
  Tip = -> Pocket041
FEATURE [Sketcher::SketchObject] Sketch098
  AttachmentOffset = pos=(113.5,0,0) rot=(0,0,1;0rad)
  FullyConstrained = true
  MapMode = 5
  Placement = pos=(113.5,0,0) rot=(0,0,1;0rad)
  Support = -> [XY_Plane034]
  expr: .AttachmentOffset.Base.x = +<<sho>>.B3 / 2 + <<sho>>.B4 + <<plug>>.B3 / 2 + 2 + <<sho>>.B6
  sketch-geometry (1):
    g0: Circle CenterX=0 CenterY=0 CenterZ=0 NormalX=0 NormalY=0 NormalZ=1 AngleXU=0 Radius=1.75
  constraints (2):
    c: Coincident(g0,g-1)
    c: Diameter(g0) = 3.5
FEATURE [Sketcher::SketchObject] Sketch099
  AttachmentOffset = pos=(0,0,132) rot=(0,0,1;0rad)
  FullyConstrained = true
  MapMode = 5
  Placement = pos=(132,-2.93e-14,2.93e-14) rot=(0.57735,0.57735,0.57735;2.0944rad)
  Support = -> [YZ_Plane034]
  expr: Constraints[18] = <<sta>>.B3 / 2 + 2
  expr: Constraints[7] = <<sta>>.B3
  expr: .AttachmentOffset.Base.z = 250 - (<<sho>>.B3 / 2 + <<sho>>.B4 + <<plug>>.B3 + <<sho>>.B6 - 1)
  sketch-geometry (7):
    g0: LineSegment StartX=-7.1 StartY=0 StartZ=0 EndX=-7.1 EndY=-2 EndZ=0
    g1: LineSegment StartX=-7.1 StartY=-2 StartZ=0 EndX=7.1 EndY=-2 EndZ=0
    g2: LineSegment StartX=7.1 StartY=-2 StartZ=0 EndX=7.1 EndY=0 EndZ=0
    g3: Circle CenterX=0 CenterY=5.1 CenterZ=0 NormalX=0 NormalY=0 NormalZ=1 AngleXU=0 Radius=5.1
    g4: ArcOfCircle CenterX=0 CenterY=5.1 CenterZ=0 NormalX=0 NormalY=0 NormalZ=1 AngleXU=0 Radius=7.1 StartAngle=0 EndAngle=3.14159
    g5: LineSegment StartX=-7.1 StartY=0 StartZ=0 EndX=-7.1 EndY=5.1 EndZ=0
    g6: LineSegment StartX=7.1 StartY=0 StartZ=0 EndX=7.1 EndY=5.1 EndZ=0
  constraints (19):
    c: Vertical(g0)
    c: Coincident(g1,g0)
    c: Horizontal(g1)
    c: Coincident(g2,g1)
    c: Vertical(g2)
    c: PointOnObject(g3,g-2)
    c: PointOnObject(g-1,g3)
    c: Diameter(g3) = 10.2
    c: Coincident(g4,g3)
    c: Coincident(g5,g0)
    c: Vertical(g5)
    c: Coincident(g6,g2)
    c: Vertical(g6)
    c: DistanceY(g0,g0) = 2
    c: PointOnObject(g0,g-1)
    c: PointOnObject(g2,g-1)
    c: Tangent(g4,g5) = 1.5708
    c: Tangent(g6,g4) = -1.5708
    c: Radius(g4) = 7.1
FEATURE [Sketcher::SketchObject] Sketch100
  AttachmentOffset = pos=(0,0,132) rot=(0,0,1;0rad)
  FullyConstrained = true
  MapMode = 5
  Placement = pos=(132,-2.93e-14,2.93e-14) rot=(0.57735,0.57735,0.57735;2.0944rad)
  Support = -> [YZ_Plane033]
  expr: Constraints[16] = <<sta>>.B3 / 2
  expr: Constraints[14] = <<sta>>.B3 / 2 + 2
  expr: .AttachmentOffset.Base.z = 250 - (<<sho>>.B3 / 2 + <<sho>>.B4 + <<plug>>.B3 + <<sho>>.B6 - 1)
  sketch-geometry (6):
    g0: LineSegment StartX=-7.1 StartY=0 StartZ=0 EndX=-7.1 EndY=-2 EndZ=0
    g1: LineSegment StartX=-7.1 StartY=-2 StartZ=0 EndX=7.1 EndY=-2 EndZ=0
    g2: LineSegment StartX=7.1 StartY=-2 StartZ=0 EndX=7.1 EndY=0 EndZ=0
    g3: ArcOfCircle CenterX=0 CenterY=5.1 CenterZ=0 NormalX=0 NormalY=0 NormalZ=1 AngleXU=0 Radius=7.1 StartAngle=1e-16 EndAngle=3.14159
    g4: LineSegment StartX=-7.1 StartY=0 StartZ=0 EndX=-7.1 EndY=5.1 EndZ=0
    g5: LineSegment StartX=7.1 StartY=0 StartZ=0 EndX=7.1 EndY=5.1 EndZ=0
  constraints (17):
    c: Vertical(g0)
    c: Coincident(g1,g0)
    c: Horizontal(g1)
    c: Coincident(g2,g1)
    c: Vertical(g2)
    c: Coincident(g4,g0)
    c: Vertical(g4)
    c: Coincident(g5,g2)
    c: Vertical(g5)
    c: DistanceY(g0,g0) = 2
    c: PointOnObject(g0,g-1)
    c: PointOnObject(g2,g-1)
    c: Tangent(g3,g4) = 1.5708
    c: Tangent(g5,g3) = -1.5708
    c: Radius(g3) = 7.1
    c: PointOnObject(g3,g-2)
    c: DistanceY(g3) = 5.1
FEATURE [PartDesign::Pad] Pad041
  Direction = (1,1,1)
  Length = 3
  Length2 = 38
  Placement = pos=(0,0,0) rot=(0.57735,0.57735,0.57735;2.0944rad)
  Profile = -> Sketch100
  Refine = true
  Type = 0
FEATURE [PartDesign::Pad] Pad042
  BaseFeature = -> Pad041
  Direction = (1,1,1)
  Length = 40
  Length2 = 100
  Placement = pos=(0,0,0) rot=(0.57735,0.57735,0.57735;2.0944rad)
  Profile = -> Sketch099
  Refine = true
  Reversed = true
  Type = 0
FEATURE [PartDesign::Pocket] Pocket042
  BaseFeature = -> Pad042
  Length = 5
  Length2 = 100
  Midplane = true
  Placement = pos=(0,0,0) rot=(0.57735,0.57735,0.57735;2.0944rad)
  Profile = -> Sketch098
  Refine = true
  Type = 1
FEATURE [PartDesign::Body] Body026  label="decoupe_carbon_outlet_inf001"
  Group = -> [Sketch099,Sketch098,Sketch100,Pad041,Pad042,Pocket042]
  Origin = -> Origin034
  Placement = pos=(0,0,-168) rot=(0,0,-1;1.5708rad)
  Tip = -> Pocket042
FEATURE [Sketcher::SketchObject] Sketch101
  AttachmentOffset = pos=(0,0,132) rot=(0,0,1;0rad)
  FullyConstrained = true
  MapMode = 5
  Placement = pos=(132,-2.93e-14,2.93e-14) rot=(0.57735,0.57735,0.57735;2.0944rad)
  Support = -> [YZ_Plane035]
  expr: Constraints[16] = <<sta>>.B3 / 2 + 0.5
  expr: Constraints[14] = <<sta>>.B3 / 2 + 2.5
  expr: .AttachmentOffset.Base.z = 250 - (<<sho>>.B3 / 2 + <<sho>>.B4 + <<plug>>.B3 + <<sho>>.B6 - 1)
  sketch-geometry (6):
    g0: LineSegment StartX=-7.6 StartY=0 StartZ=0 EndX=-7.6 EndY=-2 EndZ=0
    g1: LineSegment StartX=-7.6 StartY=-2 StartZ=0 EndX=7.6 EndY=-2 EndZ=0
    g2: LineSegment StartX=7.6 StartY=-2 StartZ=0 EndX=7.6 EndY=0 EndZ=0
    g3: ArcOfCircle CenterX=0 CenterY=5.6 CenterZ=0 NormalX=0 NormalY=0 NormalZ=1 AngleXU=0 Radius=7.6 StartAngle=0 EndAngle=3.14159
    g4: LineSegment StartX=-7.6 StartY=0 StartZ=0 EndX=-7.6 EndY=5.6 EndZ=0
    g5: LineSegment StartX=7.6 StartY=0 StartZ=0 EndX=7.6 EndY=5.6 EndZ=0
  constraints (17):
    c: Vertical(g0)
    c: Coincident(g1,g0)
    c: Horizontal(g1)
    c: Coincident(g2,g1)
    c: Vertical(g2)
    c: Coincident(g4,g0)
    c: Vertical(g4)
    c: Coincident(g5,g2)
    c: Vertical(g5)
    c: DistanceY(g0,g0) = 2
    c: PointOnObject(g0,g-1)
    c: PointOnObject(g2,g-1)
    c: Tangent(g3,g4) = 1.5708
    c: Tangent(g5,g3) = -1.5708
    c: Radius(g3) = 7.6
    c: PointOnObject(g3,g-2)
    c: DistanceY(g3) = 5.6
FEATURE [Sketcher::SketchObject] Sketch102
  FullyConstrained = true
  MapMode = 5
  Placement = pos=(0,0,0) rot=(0.57735,0.57735,0.57735;2.0944rad)
  Support = -> [YZ_Plane035]
  expr: Constraints[18] = <<sta>>.B3 / 2 + 2.5
  expr: Constraints[7] = <<sta>>.B3 + 1
  sketch-geometry (7):
    g0: LineSegment StartX=-7.6 StartY=0 StartZ=0 EndX=-7.6 EndY=-2 EndZ=0
    g1: LineSegment StartX=-7.6 StartY=-2 StartZ=0 EndX=7.6 EndY=-2 EndZ=0
    g2: LineSegment StartX=7.6 StartY=-2 StartZ=0 EndX=7.6 EndY=0 EndZ=0
    g3: Circle CenterX=0 CenterY=5.6 CenterZ=0 NormalX=0 NormalY=0 NormalZ=1 AngleXU=0 Radius=5.6
    g4: ArcOfCircle CenterX=0 CenterY=5.6 CenterZ=0 NormalX=0 NormalY=0 NormalZ=1 AngleXU=0 Radius=7.6 StartAngle=0 EndAngle=3.14159
    g5: LineSegment StartX=-7.6 StartY=0 StartZ=0 EndX=-7.6 EndY=5.6 EndZ=0
    g6: LineSegment StartX=7.6 StartY=0 StartZ=0 EndX=7.6 EndY=5.6 EndZ=0
  constraints (19):
    c: Vertical(g0)
    c: Coincident(g1,g0)
    c: Horizontal(g1)
    c: Coincident(g2,g1)
    c: Vertical(g2)
    c: PointOnObject(g3,g-2)
    c: PointOnObject(g-1,g3)
    c: Diameter(g3) = 11.2
    c: Coincident(g4,g3)
    c: Coincident(g5,g0)
    c: Vertical(g5)
    c: Coincident(g6,g2)
    c: Vertical(g6)
    c: DistanceY(g0,g0) = 2
    c: PointOnObject(g0,g-1)
    c: PointOnObject(g2,g-1)
    c: Tangent(g4,g5) = 1.5708
    c: Tangent(g6,g4) = -1.5708
    c: Radius(g4) = 7.6
FEATURE [PartDesign::Pad] Pad043
  Direction = (1,1,1)
  Length = 132
  Length2 = 118
  Placement = pos=(0,0,0) rot=(0.57735,0.57735,0.57735;2.0944rad)
  Profile = -> Sketch102
  Refine = true
  Type = 4
  expr: Length2 = <<sho>>.B3 / 2 + <<sho>>.B4 + <<plug>>.B3 + <<sho>>.B6 - 1
  expr: Length = 250 - (<<sho>>.B3 / 2 + <<sho>>.B4 + <<plug>>.B3 + <<sho>>.B6 - 1)
FEATURE [Sketcher::SketchObject] Sketch104
  FullyConstrained = false
  MapMode = 5
  Placement = pos=(0,0,0) rot=(1,0,0;1.5708rad)
  Support = -> [XZ_Plane035]
  sketch-geometry (4):
    g0: LineSegment StartX=10 StartY=0 StartZ=0 EndX=100 EndY=0 EndZ=0
    g1: LineSegment StartX=100 StartY=0 StartZ=0 EndX=100 EndY=23.3751 EndZ=0
    g2: LineSegment StartX=100 StartY=23.3751 StartZ=0 EndX=10 EndY=23.3751 EndZ=0
    g3: LineSegment StartX=10 StartY=23.3751 StartZ=0 EndX=10 EndY=0 EndZ=0
  constraints (11):
    c: Coincident(g0,g1)
    c: Coincident(g1,g2)
    c: Coincident(g2,g3)
    c: Coincident(g3,g0)
    c: Horizontal(g0)
    c: Horizontal(g2)
    c: Vertical(g1)
    c: Vertical(g3)
    c: PointOnObject(g0,g-1)
    c: DistanceX(g2,g2) = 90
    c: DistanceX(g2) = 10
FEATURE [Sketcher::SketchObject] Sketch103
  AttachmentOffset = pos=(112.5,0,-6) rot=(0,0,1;0rad)
  FullyConstrained = true
  MapMode = 5
  Placement = pos=(112.5,0,-6) rot=(0,0,1;0rad)
  Support = -> [XY_Plane035]
  expr: .AttachmentOffset.Base.x = +<<sho>>.B3 / 2 + <<sho>>.B4 + <<plug>>.B3 / 2 + 2 + <<sho>>.B6 - 1
  sketch-geometry (1):
    g0: Circle CenterX=0 CenterY=0 CenterZ=0 NormalX=0 NormalY=0 NormalZ=1 AngleXU=0 Radius=1.75
  constraints (2):
    c: Coincident(g0,g-1)
    c: Diameter(g0) = 3.5
FEATURE [PartDesign::Pad] Pad044
  BaseFeature = -> Pad043
  Direction = (1,1,1)
  Length = 2
  Length2 = 100
  Placement = pos=(0,0,0) rot=(0.57735,0.57735,0.57735;2.0944rad)
  Profile = -> Sketch101
  Refine = true
  Type = 0
FEATURE [PartDesign::Pocket] Pocket043
  BaseFeature = -> Pad044
  Length = 5
  Length2 = 100
  Midplane = true
  Placement = pos=(0,0,0) rot=(0.57735,0.57735,0.57735;2.0944rad)
  Profile = -> Sketch103
  Refine = true
  Type = 1
FEATURE [PartDesign::Pocket] Pocket044
  BaseFeature = -> Pocket043
  Length = 5
  Length2 = 100
  Midplane = true
  Placement = pos=(0,0,0) rot=(0.57735,0.57735,0.57735;2.0944rad)
  Profile = -> Sketch104
  Refine = true
  Type = 1
FEATURE [PartDesign::Mirrored] Mirrored006
  BaseFeature = -> Pocket044
  MirrorPlane = -> Sketch104 [V_Axis]
  Originals = -> [Pocket044]
  Placement = pos=(0,0,0) rot=(0.57735,0.57735,0.57735;2.0944rad)
  Refine = true
FEATURE [PartDesign::Body] Body027  label="decoupe_carbon_l250_outlet_sup"
  Group = -> [Sketch102,Pad043,Sketch103,Sketch101,Sketch104,Pad044,Pocket043,Pocket044,Mirrored006]
  Origin = -> Origin035
  Placement = pos=(0,0,-161) rot=(0,0,1;0rad)
  Tip = -> Mirrored006
FEATURE [App::Part] Part007  label="outils_decoupe_carbone"
  Group = -> [Body022,Body023,Body025,Body026,Body027]
  Origin = -> Origin028
FEATURE [Part::FeaturePython] Clone016  label="attache-colier-cable001"  # Draft clone (typed FeaturePython)
  AttacherType = Attacher::AttachEngine3D
  Fuse = false
  Objects = -> [Body018]
  Placement = pos=(0,0,-80) rot=(0,0,1;3.40339rad)
  Scale = (1,1,1)
FEATURE [Part::FeaturePython] Clone017  label="attache-colier-cable002"  # Draft clone (typed FeaturePython)
  AttacherType = Attacher::AttachEngine3D
  Fuse = false
  Objects = -> [Body018]
  Placement = pos=(0,0,-80) rot=(0,0,-1;1.13446rad)
  Scale = (1,1,1)
FEATURE [Part::FeaturePython] Clone018  label="attache-colier-cable003"  # Draft clone (typed FeaturePython)
  AttacherType = Attacher::AttachEngine3D
  Fuse = false
  Objects = -> [Body018]
  Placement = pos=(0,0,-89) rot=(0,0,1;2.79253rad)
  Scale = (1,1,1)
FEATURE [Part::MultiFuse] Fusion
  Refine = true
  Shapes = -> [Clone016,Clone017,Clone018,Body018]
FEATURE [Part::Mirroring] Part__Mirroring  label="Fusion (Mirror #1)"
  Base = (0,0,0)
  Normal = (1,0,0)
  Placement = pos=(0,0,0) rot=(0,0,-1;1.5708rad)
  Source = -> Fusion
FEATURE [Part::Fuse] Fusion001  label="passage-cable"
  Base = -> Fusion
  Refine = true
  Tool = -> Part__Mirroring
FEATURE [Sketcher::SketchObject] Sketch105
  AttachmentOffset = pos=(0,0,-14.625) rot=(0,0,1;0rad)
  FullyConstrained = false
  MapMode = 5
  Placement = pos=(0,0,-14.625) rot=(0,0,1;0rad)
  Support = -> [XY_Plane027]
  expr: .AttachmentOffset.Base.z = -<<payload>>.B8 / 2
  sketch-geometry (3):
    g0: ArcOfCircle CenterX=-9.16422 CenterY=54.8391 CenterZ=0 NormalX=0 NormalY=0 NormalZ=1 AngleXU=0 Radius=50.714 StartAngle=1.81892 EndAngle=2.6473
    g1: ArcOfCircle CenterX=0 CenterY=0 CenterZ=0 NormalX=0 NormalY=0 NormalZ=1 AngleXU=0 Radius=95.5 StartAngle=1.79915 EndAngle=2.16933
    g2: LineSegment StartX=-21.6188 StartY=104 StartZ=0 EndX=-21.6188 EndY=93.0208 EndZ=0
  constraints (5):
    c: Coincident(g1,g0)
    c: Coincident(g1,g-1)
    c: Coincident(g2,g0)
    c: Coincident(g2,g1)
    c: Vertical(g2)
FEATURE [PartDesign::Pad] Pad045
  BaseFeature = -> Pad034
  Direction = (1,1,1)
  Length = 21.6188
  Length2 = 100
  Midplane = true
  Profile = -> Sketch105
  Refine = true
  Reversed = true
  Type = 0
  expr: Length = <<payload>>.F6 / 2
FEATURE [PartDesign::Mirrored] Mirrored007
  BaseFeature = -> Pad045
  MirrorPlane = -> Sketch105 [V_Axis]
  Originals = -> [Pad045]
  Refine = true
FEATURE [PartDesign::Chamfer] Chamfer002
  Angle = 45
  Base = -> Mirrored007 [Edge21,Edge17,Edge47,Edge43]
  BaseFeature = -> Mirrored007
  ChamferType = 0
  FlipDirection = false
  Refine = true
  Size = 10.5
  Size2 = 1
  SupportTransform = false
FEATURE [PartDesign::Fillet] Fillet006
  Base = -> Chamfer002 [Edge26,Edge51,Edge47,Edge4]
  BaseFeature = -> Chamfer002
  Radius = 2.5
  Refine = true
  SupportTransform = false
FEATURE [PartDesign::Pocket] Pocket045
  BaseFeature = -> Fillet006
  Length = 4.1
  Length2 = 100
  Profile = -> Sketch085
  Refine = true
  Type = 0
  expr: Length = <<screw>>.B7
FEATURE [PartDesign::Pocket] Pocket046
  BaseFeature = -> Pocket045
  Length = 8
  Length2 = 100
  Profile = -> Sketch086
  Refine = true
  Type = 0
FEATURE [PartDesign::Mirrored] Mirrored008
  BaseFeature = -> Pocket046
  MirrorPlane = -> Sketch085 [V_Axis]
  Originals = -> [Pocket045]
  Refine = true
FEATURE [PartDesign::Mirrored] Mirrored009
  BaseFeature = -> Mirrored008
  MirrorPlane = -> Sketch086 [V_Axis]
  Originals = -> [Pocket046]
  Refine = true
FEATURE [PartDesign::Pocket] Pocket047
  BaseFeature = -> Mirrored009
  Length = 5
  Length2 = 100
  Midplane = true
  Profile = -> Sketch087
  Refine = true
  Type = 1
FEATURE [PartDesign::Body] Body020  label="mortaise_front"
  Group = -> [Sketch083,Pad033,Sketch084,Pad034,Sketch085,Sketch086,Sketch087,Sketch105,Pad045,Mirrored007,Chamfer002,Fillet006,Pocket045,Pocket046,Mirrored008,Mirrored009,Pocket047]
  Origin = -> Origin027
  Placement = pos=(0,0,-45) rot=(0,0,1;2.35619rad)
  Tip = -> Pocket047
FEATURE [Sketcher::SketchObject] Sketch106
  AttachmentOffset = pos=(0,0,96) rot=(0,0,1;0rad)
  FullyConstrained = true
  MapMode = 5
  Placement = pos=(0,-96,-2.13e-14) rot=(1,0,0;1.5708rad)
  Support = -> [XZ_Plane036]
  expr: Constraints[1] = <<screw>>.B6 + 2 * 1.64
  expr: .AttachmentOffset.Base.z = <<sho>>.B3 / 2 + <<sho>>.B4
  sketch-geometry (1):
    g0: Circle CenterX=0 CenterY=0 CenterZ=0 NormalX=0 NormalY=0 NormalZ=1 AngleXU=0 Radius=4.39
  constraints (2):
    c: Coincident(g0,g-1)
    c: Diameter(g0) = 8.78
FEATURE [PartDesign::Pad] Pad046
  Direction = (1,1,1)
  Length = 6
  Length2 = 1.5
  Placement = pos=(0,0,0) rot=(1,0,0;1.5708rad)
  Profile = -> Sketch106
  Refine = true
  Type = 4
FEATURE [PartDesign::Groove] Groove003
  Angle = 180
  Axis = (-2e-16,3e-16,1)
  Base = (0,0,0)
  BaseFeature = -> Mirrored002
  Midplane = true
  Profile = -> Sketch069
  ReferenceAxis = -> Sketch069 [V_Axis]
  Refine = true
  Reversed = true
FEATURE [PartDesign::Body] Body016  label="batt_bucket"
  Group = -> [Sketch069,Sketch070,Pad028,Sketch072,Sketch075,Mirrored001,Revolution002,PolarPattern004,Sketch076,Pocket033,Pocket034,Mirrored002,Groove003]
  Origin = -> Origin022
  Placement = pos=(1.5,-1.5,-161.5) rot=(0,0,1;0.785398rad)
  Tip = -> Groove003
FEATURE [Part::FeaturePython] Clone014  label="batt_bucket001"  # Draft clone (typed FeaturePython)
  AttacherType = Attacher::AttachEngine3D
  Fuse = false
  Objects = -> [Body016]
  Placement = pos=(-1.5,1.5,-161.5) rot=(0,0,1;3.92699rad)
  Scale = (1,1,1)
FEATURE [App::Part] Part005  label="BATT"
  Group = -> [Body014,Clone013,Body015,Body016,Clone014]
  Origin = -> Origin019
FEATURE [Sketcher::SketchObject] Sketch107
  AttachmentOffset = pos=(0,0,100.36) rot=(0,0,1;0rad)
  FullyConstrained = false
  MapMode = 5
  Placement = pos=(0,-100.36,-2.23e-14) rot=(1,0,0;1.5708rad)
  Support = -> [XZ_Plane036]
  expr: Constraints[14] = <<screw>>.B6
  expr: .AttachmentOffset.Base.z = <<sho>>.B3 / 2 + <<sho>>.B4 + 6 - 1.64
  sketch-geometry (10):
    g0: LineSegment StartX=-2.75 StartY=9.09522 StartZ=0 EndX=2.75 EndY=9.09522 EndZ=0
    g1: LineSegment StartX=0 StartY=-3.17543 StartZ=0 EndX=2.75 EndY=-1.58771 EndZ=0
    g2: LineSegment StartX=2.75 StartY=-1.58771 StartZ=0 EndX=2.75 EndY=1.58771 EndZ=0
    g3: LineSegment StartX=-2.75 StartY=1.58771 StartZ=0 EndX=-2.75 EndY=-1.58771 EndZ=0
    g4: LineSegment StartX=-2.75 StartY=-1.58771 StartZ=0 EndX=0 EndY=-3.17543 EndZ=0
    g5: Circle CenterX=0 CenterY=0 CenterZ=0 NormalX=0 NormalY=0 NormalZ=1 AngleXU=0 Radius=3.17543
    g6: LineSegment StartX=-2.75 StartY=1.58771 StartZ=0 EndX=0 EndY=3.17543 EndZ=0
    g7: LineSegment StartX=0 StartY=3.17543 StartZ=0 EndX=2.75 EndY=1.58771 EndZ=0
    g8: LineSegment StartX=-2.75 StartY=9.09522 StartZ=0 EndX=-2.75 EndY=1.58771 EndZ=0
    g9: LineSegment StartX=2.75 StartY=9.09522 StartZ=0 EndX=2.75 EndY=1.58771 EndZ=0
  constraints (25):
    c: Horizontal(g0)
    c: Coincident(g1,g2)
    c: Coincident(g3,g4)
    c: Coincident(g4,g1)
    c: Equal(g1,g2)
    c: Equal(g1,g3)
    c: Equal(g1,g4)
    c: PointOnObject(g1,g5)
    c: PointOnObject(g2,g5)
    c: PointOnObject(g6,g5)
    c: PointOnObject(g3,g5)
    c: PointOnObject(g3,g5)
    c: PointOnObject(g4,g5)
    c: PointOnObject(g4,g-2)
    c: DistanceX(g3,g1) = 5.5
    c: Coincident(g6,g3)
    c: Coincident(g7,g6)
    c: Coincident(g7,g2)
    c: Equal(g7,g2)
    c: Equal(g6,g3)
    c: Coincident(g8,g0)
    c: Coincident(g9,g0)
    c: Tangent(g9,g2) = 1.5708
    c: Tangent(g8,g3) = -1.5708
    c: Coincident(g5,g-1)
FEATURE [PartDesign::Pocket] Pocket048
  BaseFeature = -> Pad046
  Length = 4.1
  Length2 = 100
  Placement = pos=(0,0,0) rot=(1,0,0;1.5708rad)
  Profile = -> Sketch107
  Refine = true
  Type = 0
  expr: Length = <<screw>>.B7
FEATURE [Sketcher::SketchObject] Sketch108
  FullyConstrained = true
  MapMode = 5
  Placement = pos=(0,0,0) rot=(1,0,0;1.5708rad)
  Support = -> [XZ_Plane036]
  expr: Constraints[1] = <<screw>>.B4
  sketch-geometry (1):
    g0: Circle CenterX=0 CenterY=0 CenterZ=0 NormalX=0 NormalY=0 NormalZ=1 AngleXU=0 Radius=1.625
  constraints (2):
    c: Coincident(g0,g-1)
    c: Diameter(g0) = 3.25
FEATURE [PartDesign::Pocket] Pocket049
  BaseFeature = -> Pocket048
  Length = 5
  Length2 = 100
  Placement = pos=(0,0,0) rot=(1,0,0;1.5708rad)
  Profile = -> Sketch108
  Refine = true
  Reversed = true
  Type = 1
FEATURE [Sketcher::SketchObject] Sketch109
  FullyConstrained = true
  MapMode = 5
  Placement = pos=(0,0,0) rot=(0.57735,0.57735,0.57735;2.0944rad)
  Support = -> [YZ_Plane036]
  expr: Constraints[6] = -<<sho>>.B3 / 2 - <<sho>>.B4 - 6
  expr: Constraints[8] = -<<screw>>.B6 / 2 - 1.64
  sketch-geometry (3):
    g0: LineSegment StartX=-102 StartY=-4.39 StartZ=0 EndX=-94.5 EndY=-4.39 EndZ=0
    g1: LineSegment StartX=-102 StartY=-4.39 StartZ=0 EndX=-94.5 EndY=-13.3282 EndZ=0
    g2: LineSegment StartX=-94.5 StartY=-4.39 StartZ=0 EndX=-94.5 EndY=-13.3282 EndZ=0
  constraints (9):
    c: Horizontal(g0)
    c: Coincident(g1,g0)
    c: Coincident(g2,g0)
    c: Coincident(g2,g1)
    c: Perpendicular(g0,g2)
    c: DistanceX(g0,g0) = 7.5
    c: DistanceX(g0) = -102
    c: Angle(g2,g1) = 0.698132
    c: DistanceY(g0) = -4.39
FEATURE [PartDesign::Revolution] Revolution004
  Angle = 80
  Axis = (1e-16,1,-1e-16)
  Base = (0,0,0)
  BaseFeature = -> Pocket049
  Midplane = true
  Placement = pos=(0,0,0) rot=(1,0,0;1.5708rad)
  Profile = -> Sketch109
  ReferenceAxis = -> Y_Axis036
  Refine = true
FEATURE [Sketcher::SketchObject] Sketch110
  FullyConstrained = false
  MapMode = 5
  Placement = pos=(0,0,0) rot=(1,0,0;1.5708rad)
  Support = -> [XZ_Plane036]
  expr: Constraints[18] = <<screw>>.B6 + 2 * 1.64
  sketch-geometry (9):
    g0: LineSegment StartX=-2.82184 StartY=-3.36294 StartZ=0 EndX=-2.82184 EndY=-17.0913 EndZ=0
    g1: LineSegment StartX=-2.82184 StartY=-17.0913 StartZ=0 EndX=-16.9129 EndY=-13.166 EndZ=0
    g2: LineSegment StartX=-16.9129 StartY=-13.166 StartZ=0 EndX=-10.0577 EndY=-2.94128 EndZ=0
    g3: LineSegment StartX=-10.0577 StartY=-2.94128 StartZ=0 EndX=-2.82184 EndY=-3.36294 EndZ=0
    g4: LineSegment StartX=2.82184 StartY=-3.36294 StartZ=0 EndX=2.82184 EndY=-17.0913 EndZ=0
    g5: LineSegment StartX=2.82184 StartY=-17.0913 StartZ=0 EndX=13.1803 EndY=-17.0913 EndZ=0
    g6: LineSegment StartX=13.1803 StartY=-17.0913 StartZ=0 EndX=13.1803 EndY=-3.36294 EndZ=0
    g7: LineSegment StartX=2.82184 StartY=-3.36294 StartZ=0 EndX=13.1803 EndY=-3.36294 EndZ=0
    g8: ArcOfCircle CenterX=0 CenterY=0 CenterZ=0 NormalX=0 NormalY=0 NormalZ=1 AngleXU=0 Radius=4.39 StartAngle=4.01426 EndAngle=5.41052
  constraints (19):
    c: Coincident(g1,g0)
    c: Coincident(g2,g1)
    c: Coincident(g3,g2)
    c: Parallel(g0,g-2)
    c: Vertical(g4)
    c: Coincident(g5,g4)
    c: Horizontal(g5)
    c: Coincident(g6,g5)
    c: Vertical(g6)
    c: Coincident(g7,g6)
    c: Horizontal(g7)
    c: Symmetric(g4,g0,g-2)
    c: Coincident(g8,g-1)
    c: Coincident(g8,g0)
    c: Coincident(g8,g4)
    c: Angle(g8) = 1.39626
    c: Coincident(g0,g3)
    c: Coincident(g4,g7)
    c: Diameter(g8) = 8.78
FEATURE [PartDesign::Pocket] Pocket050
  BaseFeature = -> Revolution004
  Length = 5
  Length2 = 100
  Midplane = true
  Placement = pos=(0,0,0) rot=(1,0,0;1.5708rad)
  Profile = -> Sketch110
  Refine = true
  Type = 1
FEATURE [PartDesign::Body] Body028  label="attache_vis_universelle"
  Group = -> [Sketch106,Pad046,Sketch107,Pocket048,Sketch108,Pocket049,Sketch109,Revolution004,Sketch110,Pocket050]
  Origin = -> Origin036
  Placement = pos=(0,0,-56) rot=(0,0,1;0rad)
  Tip = -> Pocket050
FEATURE [Part::FeaturePython] Clone019  label="attache_vis_universelle001"  # Draft clone (typed FeaturePython)
  AttacherType = Attacher::AttachEngine3D
  Fuse = false
  Objects = -> [Body028]
  Placement = pos=(0,0,-68) rot=(0,0,1;1.39626rad)
  Scale = (1,1,1)
FEATURE [Part::FeaturePython] Clone020  label="attache_vis_universelle002"  # Draft clone (typed FeaturePython)
  AttacherType = Attacher::AttachEngine3D
  Fuse = false
  Objects = -> [Body028]
  Placement = pos=(0,0,-68) rot=(0,0,1;1.74533rad)
  Scale = (1,1,1)
FEATURE [Part::FeaturePython] Clone022  label="attache_vis_universelle004"  # Draft clone (typed FeaturePython)
  AttacherType = Attacher::AttachEngine3D
  Fuse = false
  Objects = -> [Body028]
  Placement = pos=(0,0,-28) rot=(0,0,1;2.0944rad)
  Scale = (1,1,1)
FEATURE [Part::FeaturePython] Clone023  label="attache_vis_universelle005"  # Draft clone (typed FeaturePython)
  AttacherType = Attacher::AttachEngine3D
  Fuse = false
  Objects = -> [Body028]
  Placement = pos=(0,0,-28) rot=(0,0,1;2.61799rad)
  Scale = (1,1,1)
FEATURE [Sketcher::SketchObject] Sketch111
  FullyConstrained = true
  MapMode = 5
  Placement = pos=(0,0,0) rot=(1,0,0;1.5708rad)
  Support = -> [XZ_Plane037]
  sketch-geometry (1):
    g0: Circle CenterX=0 CenterY=0 CenterZ=0 NormalX=0 NormalY=0 NormalZ=1 AngleXU=0 Radius=15.5
  constraints (2):
    c: Coincident(g0,g-1)
    c: Diameter(g0) = 31
FEATURE [PartDesign::Pad] Pad047
  Direction = (1,1,1)
  Length = 10
  Length2 = 100
  Placement = pos=(0,0,0) rot=(1,0,0;1.5708rad)
  Profile = -> Sketch111
  Refine = true
  Type = 0
FEATURE [Sketcher::SketchObject] Sketch112
  FullyConstrained = false
  MapMode = 5
  Placement = pos=(0,-10,2.2e-15) rot=(1,0,0;1.5708rad)
  Support = -> [Pad047]
  sketch-geometry (4):
    g0: LineSegment StartX=-12.1344 StartY=0 StartZ=0 EndX=11.7831 EndY=0 EndZ=0
    g1: LineSegment StartX=11.7831 StartY=0 StartZ=0 EndX=11.7831 EndY=-25 EndZ=0
    g2: LineSegment StartX=11.7831 StartY=-25 StartZ=0 EndX=-12.1344 EndY=-25 EndZ=0
    g3: LineSegment StartX=-12.1344 StartY=-25 StartZ=0 EndX=-12.1344 EndY=0 EndZ=0
  constraints (9):
    c: Coincident(g0,g1)
    c: Coincident(g1,g2)
    c: Coincident(g2,g3)
    c: Coincident(g3,g0)
    c: Horizontal(g2)
    c: Vertical(g1)
    c: Vertical(g3)
    c: DistanceY(g1) = -25
    c: Tangent(g0,g-1)
FEATURE [PartDesign::Pad] Pad048
  BaseFeature = -> Pad047
  Direction = (1,1,1)
  Length = 10
  Length2 = 100
  Placement = pos=(0,0,0) rot=(1,0,0;1.5708rad)
  Profile = -> Sketch112
  Refine = true
  Reversed = true
  Type = 0
FEATURE [PartDesign::Body] Body029  label="lumiere"
  Group = -> [Sketch111,Pad047,Sketch112,Pad048]
  Origin = -> Origin037
  Placement = pos=(-125.865,-67.8823,-106) rot=(0,0,-1;0.785398rad)
  Tip = -> Pad048
FEATURE [Part::FeaturePython] Clone024  label="attache_vis_universelle006"  # Draft clone (typed FeaturePython)
  AttacherType = Attacher::AttachEngine3D
  Fuse = false
  Objects = -> [Body028]
  Placement = pos=(0,0,-72) rot=(0,0,1;2.35619rad)
  Scale = (1,1,1)
FEATURE [Sketcher::SketchObject] Sketch113
  FullyConstrained = true
  MapMode = 5
  Support = -> [XY_Plane038]
  expr: Constraints[27] = <<payload>>.B11
  expr: Constraints[9] = <<payload>>.B4
  expr: Constraints[10] = <<payload>>.B6 - 2 * <<payload>>.B9
  expr: Constraints[7] = <<payload>>.B7 - <<payload>>.B9
  expr: Constraints[13] = <<payload>>.D6
  expr: Constraints[26] = <<payload>>.B10
  expr: Constraints[8] = <<payload>>.B4
  expr: Constraints[6] = <<sho>>.B3 / 2 + <<sho>>.B4
  sketch-geometry (10):
    g0: LineSegment StartX=-21.3822 StartY=103.85 StartZ=0 EndX=-9.85 EndY=103.85 EndZ=0
    g1: LineSegment StartX=-9.85 StartY=103.85 StartZ=0 EndX=-14.3822 EndY=96 EndZ=0
    g2: LineSegment StartX=-14.3822 StartY=96 StartZ=0 EndX=14.3822 EndY=96 EndZ=0
    g3: LineSegment StartX=14.3822 StartY=96 StartZ=0 EndX=9.85 EndY=103.85 EndZ=0
    g4: LineSegment StartX=9.85 StartY=103.85 StartZ=0 EndX=21.3822 EndY=103.85 EndZ=0
    g5: LineSegment StartX=-21.3822 StartY=103.85 StartZ=0 EndX=-30 EndY=103.85 EndZ=0
    g6: LineSegment StartX=21.3822 StartY=103.85 StartZ=0 EndX=30 EndY=103.85 EndZ=0
    g7: LineSegment StartX=-30 StartY=103.85 StartZ=0 EndX=-30 EndY=108.35 EndZ=0
    g8: LineSegment StartX=-30 StartY=108.35 StartZ=0 EndX=30 EndY=108.35 EndZ=0
    g9: LineSegment StartX=30 StartY=103.85 StartZ=0 EndX=30 EndY=108.35 EndZ=0
  constraints (28):
    c: Horizontal(g0)
    c: Coincident(g1,g0)
    c: Coincident(g2,g1)
    c: Horizontal(g2)
    c: Coincident(g3,g2)
    c: Coincident(g4,g3)
    c: DistanceY(g1) = 96
    c: DistanceY(g1,g0) = 7.85
    c: Angle(g0,g1) = 1.0472
    c: Angle(g3,g4) = 1.0472
    c: DistanceX(g0,g3) = 19.7
    c: Symmetric(g0,g3,g-2)
    c: Symmetric(g0,g4,g-2)
    c: DistanceX(g0,g1) = 7
    c: Coincident(g5,g0)
    c: Horizontal(g5)
    c: Coincident(g6,g4)
    c: Horizontal(g6)
    c: Coincident(g7,g5)
    c: Vertical(g7)
    c: Coincident(g8,g7)
    c: Horizontal(g8)
    c: Coincident(g9,g6)
    c: Coincident(g9,g8)
    c: Vertical(g9)
    c: Equal(g5,g6)
    c: DistanceY(g7,g7) = 4.5
    c: DistanceX(g8,g8) = 60
FEATURE [PartDesign::Pad] Pad049
  Direction = (1,1,1)
  Length = 29.25
  Length2 = 100
  Profile = -> Sketch113
  Refine = true
  Reversed = true
  Type = 0
  expr: Length = <<payload>>.B8
FEATURE [PartDesign::Fillet] Fillet007
  Base = -> Pad049 [Edge5,Edge2]
  BaseFeature = -> Pad049
  Radius = 1
  Refine = true
  SupportTransform = false
FEATURE [Sketcher::SketchObject] Sketch114
  AttachmentOffset = pos=(0,0,-109) rot=(0,0,1;0rad)
  FullyConstrained = true
  MapMode = 5
  Placement = pos=(0,109,2.42e-14) rot=(1,0,0;1.5708rad)
  Support = -> [XZ_Plane038]
  expr: Constraints[0] = <<screw>>.B4
  expr: Constraints[1] = -<<payload>>.B8 / 3 + <<screw>>.B6 / 2
  sketch-geometry (1):
    g0: Circle CenterX=-17.229 CenterY=-7 CenterZ=0 NormalX=0 NormalY=0 NormalZ=1 AngleXU=0 Radius=1.625
  constraints (3):
    c: Diameter(g0) = 3.25
    c: DistanceY(g0) = -7
    c: DistanceX(g0) = -17.229
FEATURE [Sketcher::SketchObject] Sketch115
  FullyConstrained = true
  MapMode = 5
  Support = -> [XY_Plane038]
  expr: Constraints[7] = <<payload>>.B10
  expr: Constraints[9] = <<payload>>.B11
  expr: Constraints[5] = <<sho>>.B3 / 2 + <<sho>>.B4 + <<payload>>.B7 - <<payload>>.B9
  sketch-geometry (4):
    g0: LineSegment StartX=-30 StartY=108.35 StartZ=0 EndX=30 EndY=108.35 EndZ=0
    g1: LineSegment StartX=30 StartY=108.35 StartZ=0 EndX=30 EndY=103.85 EndZ=0
    g2: LineSegment StartX=30 StartY=103.85 StartZ=0 EndX=-30 EndY=103.85 EndZ=0
    g3: LineSegment StartX=-30 StartY=103.85 StartZ=0 EndX=-30 EndY=108.35 EndZ=0
  constraints (11):
    c: Coincident(g0,g1)
    c: Coincident(g1,g2)
    c: Coincident(g2,g3)
    c: Coincident(g3,g0)
    c: Vertical(g1)
    c: DistanceY(g2) = 103.85
    c: Perpendicular(g0,g3)
    c: DistanceY(g3,g3) = 4.5
    c: Perpendicular(g1,g0)
    c: DistanceX(g2,g2) = 60
    c: Symmetric(g2,g1,g-2)
FEATURE [Sketcher::SketchObject] Sketch121
  FullyConstrained = true
  MapMode = 5
  Placement = pos=(0,0,0) rot=(0.57735,0.57735,0.57735;2.0944rad)
  Support = -> [YZ_Plane040]
  sketch-geometry (6):
    g0: LineSegment StartX=0 StartY=30 StartZ=0 EndX=-35 EndY=30 EndZ=0
    g1: LineSegment StartX=-35 StartY=30 StartZ=0 EndX=-35 EndY=0 EndZ=0
    g2: LineSegment StartX=-35 StartY=0 StartZ=0 EndX=-47 EndY=0 EndZ=0
    g3: LineSegment StartX=0 StartY=30 StartZ=0 EndX=0 EndY=40 EndZ=0
    g4: LineSegment StartX=0 StartY=40 StartZ=0 EndX=-47 EndY=40 EndZ=0
    g5: LineSegment StartX=-47 StartY=0 StartZ=0 EndX=-47 EndY=40 EndZ=0
  constraints (18):
    c: PointOnObject(g0,g-2)
    c: Horizontal(g0)
    c: Coincident(g1,g0)
    c: PointOnObject(g1,g-1)
    c: Vertical(g1)
    c: Coincident(g2,g1)
    c: PointOnObject(g2,g-1)
    c: Coincident(g3,g0)
    c: PointOnObject(g3,g-2)
    c: Coincident(g4,g3)
    c: Horizontal(g4)
    c: DistanceX(g0,g0) = 35
    c: DistanceY(g1,g1) = 30
    c: DistanceY(g3,g3) = 10
    c: DistanceX(g2,g2) = 12
    c: Coincident(g5,g2)
    c: Vertical(g5)
    c: Coincident(g5,g4)
FEATURE [PartDesign::Pad] Pad053
  Direction = (1,1,1)
  Length = 10
  Length2 = 100
  Placement = pos=(0,0,0) rot=(0.57735,0.57735,0.57735;2.0944rad)
  Profile = -> Sketch121
  Refine = true
  Type = 0
FEATURE [PartDesign::Mirrored] Mirrored012
  BaseFeature = -> Pad053
  MirrorPlane = -> Sketch121 [V_Axis]
  Originals = -> [Pad053]
  Placement = pos=(0,0,0) rot=(0.57735,0.57735,0.57735;2.0944rad)
  Refine = true
FEATURE [Sketcher::SketchObject] Sketch122
  AttachmentOffset = pos=(0,0,12) rot=(0,0,1;0rad)
  FullyConstrained = true
  MapMode = 5
  Placement = pos=(12,-2.7e-15,2.7e-15) rot=(0.57735,0.57735,0.57735;2.0944rad)
  Support = -> [YZ_Plane040]
  expr: Constraints[9] = -35 - (12 - 6.4) / 2
  sketch-geometry (4):
    g0: ArcOfCircle CenterX=-44.2 CenterY=6.925 CenterZ=0 NormalX=0 NormalY=0 NormalZ=1 AngleXU=0 Radius=0.925 StartAngle=1.5708 EndAngle=4.71239
    g1: ArcOfCircle CenterX=-37.8 CenterY=6.925 CenterZ=0 NormalX=0 NormalY=0 NormalZ=1 AngleXU=0 Radius=0.925 StartAngle=4.71239 EndAngle=7.85398
    g2: LineSegment StartX=-44.2 StartY=6 StartZ=0 EndX=-37.8 EndY=6 EndZ=0
    g3: LineSegment StartX=-44.2 StartY=7.85 StartZ=0 EndX=-37.8 EndY=7.85 EndZ=0
  constraints (10):
    c: Tangent(g0,g3) = 1.5708
    c: Tangent(g0,g2) = -1.5708
    c: Tangent(g2,g1) = -1.5708
    c: Tangent(g3,g1) = 1.5708
    c: Horizontal(g2)
    c: Equal(g0,g1)
    c: DistanceY(g1) = 6
    c: DistanceY(g0,g0) = 1.85
    c: DistanceX(g0,g1) = 6.4
    c: DistanceX(g1) = -37.8
FEATURE [PartDesign::Pocket] Pocket055
  BaseFeature = -> Mirrored012
  Length = 5
  Length2 = 100
  Placement = pos=(0,0,0) rot=(0.57735,0.57735,0.57735;2.0944rad)
  Profile = -> Sketch122
  Refine = true
  Type = 1
FEATURE [PartDesign::Mirrored] Mirrored013
  BaseFeature = -> Pocket055
  MirrorPlane = -> Sketch122 [V_Axis]
  Originals = -> [Pocket055]
  Placement = pos=(0,0,0) rot=(0.57735,0.57735,0.57735;2.0944rad)
  Refine = true
FEATURE [Sketcher::SketchObject] Sketch123
  FullyConstrained = true
  MapMode = 5
  Placement = pos=(0,0,0) rot=(1,0,0;1.5708rad)
  Support = -> [XZ_Plane040]
  sketch-geometry (1):
    g0: Circle CenterX=5 CenterY=0 CenterZ=0 NormalX=0 NormalY=0 NormalZ=1 AngleXU=0 Radius=5
  constraints (3):
    c: PointOnObject(g0,g-1)
    c: Diameter(g0) = 10
    c: DistanceX(g0) = 5
FEATURE [PartDesign::Pocket] Pocket056
  BaseFeature = -> Mirrored013
  Length = 5
  Length2 = 100
  Midplane = true
  Placement = pos=(0,0,0) rot=(0.57735,0.57735,0.57735;2.0944rad)
  Profile = -> Sketch123
  Refine = true
  Type = 1
FEATURE [Sketcher::SketchObject] Sketch124
  FullyConstrained = true
  MapMode = 5
  Placement = pos=(0,0,0) rot=(0.57735,0.57735,0.57735;2.0944rad)
  Support = -> [YZ_Plane040]
  expr: Constraints[4] = 15 + 10
  sketch-geometry (2):
    g0: Circle CenterX=0 CenterY=35 CenterZ=0 NormalX=0 NormalY=0 NormalZ=1 AngleXU=0 Radius=7.5
    g1: Circle CenterX=0 CenterY=35 CenterZ=0 NormalX=0 NormalY=0 NormalZ=1 AngleXU=0 Radius=12.5
  constraints (5):
    c: PointOnObject(g0,g-2)
    c: Diameter(g0) = 15
    c: DistanceY(g0) = 35
    c: Coincident(g1,g0)
    c: Diameter(g1) = 25
FEATURE [PartDesign::Pad] Pad054
  BaseFeature = -> Pocket056
  Direction = (1,1,1)
  Length = 10
  Length2 = 100
  Placement = pos=(0,0,0) rot=(0.57735,0.57735,0.57735;2.0944rad)
  Profile = -> Sketch124
  Refine = true
  Type = 0
FEATURE [Sketcher::SketchObject] Sketch125
  FullyConstrained = true
  MapMode = 5
  Placement = pos=(0,0,0) rot=(0.57735,0.57735,0.57735;2.0944rad)
  Support = -> [YZ_Plane040]
  sketch-geometry (1):
    g0: Circle CenterX=0 CenterY=35 CenterZ=0 NormalX=0 NormalY=0 NormalZ=1 AngleXU=0 Radius=7.5
  constraints (3):
    c: PointOnObject(g0,g-2)
    c: DistanceY(g0) = 35
    c: Diameter(g0) = 15
FEATURE [PartDesign::Pocket] Pocket057
  BaseFeature = -> Pad054
  Length = 5
  Length2 = 100
  Placement = pos=(0,0,0) rot=(0.57735,0.57735,0.57735;2.0944rad)
  Profile = -> Sketch125
  Refine = true
  Reversed = true
  Type = 1
FEATURE [PartDesign::Chamfer] Chamfer003
  Angle = 45
  Base = -> Pocket057 [Edge4,Edge55]
  BaseFeature = -> Pocket057
  ChamferType = 0
  FlipDirection = false
  Placement = pos=(0,0,0) rot=(0.57735,0.57735,0.57735;2.0944rad)
  Refine = true
  Size = 8
  Size2 = 1
  SupportTransform = false
FEATURE [PartDesign::Fillet] Fillet011
  Base = -> Chamfer003 [Edge68,Edge63]
  BaseFeature = -> Chamfer003
  Placement = pos=(0,0,0) rot=(0.57735,0.57735,0.57735;2.0944rad)
  Radius = 5
  Refine = true
  SupportTransform = false
FEATURE [PartDesign::Fillet] Fillet012
  Base = -> Fillet011 [Edge52,Edge47]
  BaseFeature = -> Fillet011
  Placement = pos=(0,0,0) rot=(0.57735,0.57735,0.57735;2.0944rad)
  Radius = 10
  Refine = true
  SupportTransform = false
FEATURE [PartDesign::Fillet] Fillet013
  Base = -> Fillet012 [Edge51,Edge37,Edge33,Edge47]
  BaseFeature = -> Fillet012
  Placement = pos=(0,0,0) rot=(0.57735,0.57735,0.57735;2.0944rad)
  Radius = 2
  Refine = true
  SupportTransform = false
FEATURE [Sketcher::SketchObject] Sketch126
  AttachmentOffset = pos=(0,0,12) rot=(0,0,1;0rad)
  FullyConstrained = false
  MapMode = 5
  Placement = pos=(12,-2.7e-15,2.7e-15) rot=(0.57735,0.57735,0.57735;2.0944rad)
  Support = -> [YZ_Plane040]
  expr: Constraints[6] = -35 - 6
  sketch-geometry (4):
    g0: ArcOfCircle CenterX=-41 CenterY=13.6064 CenterZ=0 NormalX=0 NormalY=0 NormalZ=1 AngleXU=0 Radius=1.25 StartAngle=3.14159 EndAngle=6.28319
    g1: ArcOfCircle CenterX=-41 CenterY=27.5596 CenterZ=0 NormalX=0 NormalY=0 NormalZ=1 AngleXU=0 Radius=1.25 StartAngle=0 EndAngle=3.14159
    g2: LineSegment StartX=-39.75 StartY=13.6064 StartZ=0 EndX=-39.75 EndY=27.5596 EndZ=0
    g3: LineSegment StartX=-42.25 StartY=13.6064 StartZ=0 EndX=-42.25 EndY=27.5596 EndZ=0
  constraints (8):
    c: Tangent(g0,g3) = 1.5708
    c: Tangent(g0,g2) = -1.5708
    c: Tangent(g2,g1) = -1.5708
    c: Tangent(g3,g1) = 1.5708
    c: Vertical(g2)
    c: Equal(g0,g1)
    c: DistanceX(g1) = -41
    c: DistanceX(g1,g1) = 2.5
FEATURE [PartDesign::Pocket] Pocket058
  BaseFeature = -> Fillet013
  Length = 5
  Length2 = 100
  Placement = pos=(0,0,0) rot=(0.57735,0.57735,0.57735;2.0944rad)
  Profile = -> Sketch126
  Refine = true
  Type = 1
FEATURE [PartDesign::Mirrored] Mirrored014
  BaseFeature = -> Pocket058
  MirrorPlane = -> Sketch126 [V_Axis]
  Originals = -> [Pocket058]
  Placement = pos=(0,0,0) rot=(0.57735,0.57735,0.57735;2.0944rad)
  Refine = true
FEATURE [PartDesign::Body] Body032  label="poignée"
  Group = -> [Sketch121,Pad053,Mirrored012,Sketch122,Pocket055,Mirrored013,Sketch123,Pocket056,Sketch124,Pad054,Sketch125,Pocket057,Chamfer003,Fillet011,Fillet012,Fillet013,Sketch126,Pocket058,Mirrored014]
  Origin = -> Origin040
  Tip = -> Mirrored014
FEATURE [Part::Feature] Gopro_support_camera_a_vis001001_solid  label="Gopro_support_camera_a_vis001001 (Solid)"
  Placement = pos=(-83.4386,-72.1249,-53) rot=(0,0,1;0rad)
  shape: bbox 33.77 x 33.77 x 30.27 mm, 295 faces (baked)
FEATURE [Sketcher::SketchObject] Sketch127
  FullyConstrained = false
  MapMode = 5
  Placement = pos=(0,0,0) rot=(0.57735,0.57735,0.57735;2.0944rad)
  Support = -> [YZ_Plane041]
  sketch-geometry (8):
    g0: LineSegment StartX=0 StartY=0 StartZ=0 EndX=9.5 EndY=0 EndZ=0
    g1: ArcOfCircle CenterX=9.5 CenterY=-7.5 CenterZ=0 NormalX=0 NormalY=0 NormalZ=1 AngleXU=0 Radius=7.5 StartAngle=5.35128 EndAngle=7.85398
    g2: GeomPoint X=17 Y=-7.5 Z=0
    g3: Circle CenterX=9.5 CenterY=-7.5 CenterZ=0 NormalX=0 NormalY=0 NormalZ=1 AngleXU=0 Radius=2.6
    g4: LineSegment StartX=0 StartY=0 StartZ=0 EndX=-4.5 EndY=0 EndZ=0
    g5: LineSegment StartX=-4.5 StartY=0 StartZ=0 EndX=-4.5 EndY=-35 EndZ=0
    g6: ArcOfCircle CenterX=18.9432 CenterY=-20.2126 CenterZ=0 NormalX=0 NormalY=0 NormalZ=1 AngleXU=0 Radius=8.33611 StartAngle=2.20969 EndAngle=2.43902
    g7: LineSegment StartX=12.5812 StartY=-14.8259 StartZ=0 EndX=-4.5 EndY=-35 EndZ=0
  constraints (18):
    c: Coincident(g0,g-1)
    c: PointOnObject(g0,g-1)
    c: Tangent(g1,g0) = 1.5708
    c: PointOnObject(g2,g1)
    c: DistanceY(g2,g1) = 0
    c: DistanceX(g2) = 17
    c: Coincident(g3,g1)
    c: Diameter(g3) = 5.2
    c: Coincident(g4,g0)
    c: PointOnObject(g4,g-1)
    c: Coincident(g5,g4)
    c: Vertical(g5)
    c: Diameter(g1) = 15
    c: Tangent(g6,g1) = 1.5708
    c: Tangent(g7,g6) = -1.5708
    c: DistanceX(g4,g4) = 4.5
    c: Coincident(g5,g7)
    c: DistanceY(g5,g5) = 35
FEATURE [PartDesign::Pad] Pad055
  Direction = (1,1,1)
  Length = 12.1
  Length2 = 7.6
  Placement = pos=(0,0,0) rot=(0.57735,0.57735,0.57735;2.0944rad)
  Profile = -> Sketch127
  Refine = true
  Type = 4
FEATURE [Sketcher::SketchObject] Sketch128
  FullyConstrained = false
  MapMode = 5
  Support = -> [XY_Plane041]
  sketch-geometry (4):
    g0: LineSegment StartX=-1.4 StartY=0 StartZ=0 EndX=-4.55 EndY=0 EndZ=0
    g1: LineSegment StartX=-4.55 StartY=0 StartZ=0 EndX=-4.55 EndY=18.9682 EndZ=0
    g2: LineSegment StartX=-4.55 StartY=18.9682 StartZ=0 EndX=-1.4 EndY=18.9682 EndZ=0
    g3: LineSegment StartX=-1.4 StartY=18.9682 StartZ=0 EndX=-1.4 EndY=0 EndZ=0
  constraints (11):
    c: Coincident(g0,g1)
    c: Coincident(g1,g2)
    c: Coincident(g2,g3)
    c: Coincident(g3,g0)
    c: Horizontal(g0)
    c: Horizontal(g2)
    c: Vertical(g1)
    c: Vertical(g3)
    c: PointOnObject(g0,g-1)
    c: DistanceX(g2,g2) = 3.15
    c: DistanceX(g2) = -1.4
FEATURE [Sketcher::SketchObject] Sketch130
  AttachmentOffset = pos=(0,-8,0) rot=(0,0,1;0rad)
  FullyConstrained = true
  MapMode = 5
  Placement = pos=(0,1.8e-15,-8) rot=(1,0,0;1.5708rad)
  Support = -> [XZ_Plane041]
  expr: Constraints[7] = <<screw>>.B4
  sketch-geometry (6):
    g0: ArcOfCircle CenterX=17.23 CenterY=-7 CenterZ=0 NormalX=0 NormalY=0 NormalZ=1 AngleXU=0 Radius=7 StartAngle=4.71239 EndAngle=7.85398
    g1: ArcOfCircle CenterX=-17.23 CenterY=-7 CenterZ=0 NormalX=0 NormalY=0 NormalZ=1 AngleXU=0 Radius=7 StartAngle=1.5708 EndAngle=4.71239
    g2: LineSegment StartX=17.23 StartY=-1.4024e-12 StartZ=0 EndX=-17.23 EndY=-1.1804e-12 EndZ=0
    g3: LineSegment StartX=17.23 StartY=-14 StartZ=0 EndX=-17.23 EndY=-14 EndZ=0
    g4: Circle CenterX=-17.23 CenterY=-7 CenterZ=0 NormalX=0 NormalY=0 NormalZ=1 AngleXU=0 Radius=1.625
    g5: Circle CenterX=17.23 CenterY=-7 CenterZ=0 NormalX=0 NormalY=0 NormalZ=1 AngleXU=0 Radius=1.625
  constraints (12):
    c: Tangent(g0,g3) = 1.5708
    c: Tangent(g0,g2) = -1.5708
    c: Tangent(g2,g1) = -1.5708
    c: Tangent(g3,g1) = 1.5708
    c: DistanceX(g1) = -17.23
    c: Symmetric(g0,g1,g-2)
    c: Coincident(g4,g1)
    c: Diameter(g4) = 3.25
    c: Coincident(g5,g0)
    c: Equal(g5,g4)
    c: DistanceY(g1,g-1) = 7
    c: Tangent(g2,g-1)
FEATURE [PartDesign::Pad] Pad057
  BaseFeature = -> Fillet007
  Direction = (1,1,1)
  Length = 12
  Length2 = 62
  Profile = -> Sketch115
  Refine = true
  Type = 4
FEATURE [PartDesign::Pocket] Pocket063
  BaseFeature = -> Pad057
  Length = 5
  Length2 = 100
  Midplane = true
  Profile = -> Sketch114
  Refine = true
  Type = 1
FEATURE [PartDesign::Mirrored] Mirrored017
  BaseFeature = -> Pocket063
  MirrorPlane = -> Sketch114 [V_Axis]
  Originals = -> [Pocket063]
  Refine = true
FEATURE [Sketcher::SketchObject] Sketch134
  FullyConstrained = true
  MapMode = 5
  Placement = pos=(0,0,0) rot=(1,0,0;1.5708rad)
  Support = -> [XZ_Plane038]
  expr: Constraints[1] = <<screw>>.B4
  sketch-geometry (6):
    g0: Circle CenterX=-21.5 CenterY=-44 CenterZ=0 NormalX=0 NormalY=0 NormalZ=1 AngleXU=0 Radius=1.625
    g1: Circle CenterX=21.5 CenterY=-44 CenterZ=0 NormalX=0 NormalY=0 NormalZ=1 AngleXU=0 Radius=1.625
    g2: Circle CenterX=-10 CenterY=-50 CenterZ=0 NormalX=0 NormalY=0 NormalZ=1 AngleXU=0 Radius=1.625
    g3: Circle CenterX=10 CenterY=-50 CenterZ=0 NormalX=0 NormalY=0 NormalZ=1 AngleXU=0 Radius=1.625
    g4: Circle CenterX=-17 CenterY=-56 CenterZ=0 NormalX=0 NormalY=0 NormalZ=1 AngleXU=0 Radius=1.625
    g5: Circle CenterX=17 CenterY=-56 CenterZ=0 NormalX=0 NormalY=0 NormalZ=1 AngleXU=0 Radius=1.625
  constraints (15):
    c: DistanceY(g0) = -44
    c: Diameter(g0) = 3.25
    c: DistanceX(g0) = -21.5
    c: Symmetric(g0,g1,g-2)
    c: Equal(g0,g1)
    c: Equal(g2,g3)
    c: Equal(g3,g0)
    c: Symmetric(g2,g3,g-2)
    c: Symmetric(g5,g4,g-2)
    c: Equal(g4,g5)
    c: Equal(g5,g0)
    c: DistanceX(g2) = -10
    c: DistanceX(g4) = -17
    c: DistanceY(g2,g0) = 6
    c: DistanceY(g4,g2) = 6
FEATURE [PartDesign::Pocket] Pocket064
  BaseFeature = -> Mirrored017
  Length = 5
  Length2 = 100
  Profile = -> Sketch134
  Refine = true
  Type = 1
FEATURE [PartDesign::Fillet] Fillet015
  Base = -> Pocket064 [Edge17,Edge32,Edge4,Edge2]
  BaseFeature = -> Pocket064
  Radius = 10
  Refine = true
  SupportTransform = false
FEATURE [PartDesign::Body] Body030  label="platine-tenon"
  Group = -> [Sketch113,Pad049,Fillet007,Sketch114,Sketch115,Pad057,Pocket063,Mirrored017,Sketch134,Pocket064,Fillet015]
  Origin = -> Origin038
  Placement = pos=(0,0,-45) rot=(0,0,1;2.35619rad)
  Tip = -> Fillet015
FEATURE [Sketcher::SketchObject] Sketch143
  FullyConstrained = true
  MapMode = 5
  Placement = pos=(0,0,0) rot=(1,0,0;1.5708rad)
  Support = -> [XZ_Plane044]
  sketch-geometry (4):
    g0: LineSegment StartX=-30 StartY=6 StartZ=0 EndX=-30 EndY=-32 EndZ=0
    g1: LineSegment StartX=-30 StartY=6 StartZ=0 EndX=30 EndY=6 EndZ=0
    g2: LineSegment StartX=30 StartY=6 StartZ=0 EndX=30 EndY=-32 EndZ=0
    g3: LineSegment StartX=-30 StartY=-32 StartZ=0 EndX=30 EndY=-32 EndZ=0
  constraints (11):
    c: Vertical(g0)
    c: Coincident(g1,g0)
    c: Coincident(g2,g1)
    c: Vertical(g2)
    c: Symmetric(g0,g1,g-2)
    c: DistanceX(g1,g1) = 60
    c: DistanceY(g-1,g0) = 6
    c: DistanceY(g0,g0) = 38
    c: Equal(g2,g0)
    c: Coincident(g3,g0)
    c: Coincident(g3,g2)
FEATURE [PartDesign::Pad] Pad062
  Direction = (1,1,1)
  Length = 17.5
  Length2 = 100
  Placement = pos=(0,0,0) rot=(1,0,0;1.5708rad)
  Profile = -> Sketch143
  Refine = true
  Type = 0
FEATURE [Sketcher::SketchObject] Sketch144
  AttachmentOffset = pos=(0,0,2) rot=(0,0,1;0rad)
  FullyConstrained = false
  MapMode = 5
  Placement = pos=(0,-2,-4e-16) rot=(1,0,0;1.5708rad)
  Support = -> [XZ_Plane044]
  sketch-geometry (6):
    g0: ArcOfCircle CenterX=-14.5 CenterY=-15 CenterZ=0 NormalX=0 NormalY=0 NormalZ=1 AngleXU=0 Radius=14.5 StartAngle=3.14159 EndAngle=6.28319
    g1: LineSegment StartX=-29 StartY=-15 StartZ=0 EndX=-29 EndY=0 EndZ=0
    g2: LineSegment StartX=0 StartY=0 StartZ=0 EndX=0 EndY=-15 EndZ=0
    g3: LineSegment StartX=-29 StartY=0 StartZ=0 EndX=-29 EndY=31.9348 EndZ=0
    g4: LineSegment StartX=-29 StartY=31.9348 StartZ=0 EndX=0 EndY=31.9348 EndZ=0
    g5: LineSegment StartX=0 StartY=31.9348 StartZ=0 EndX=0 EndY=0 EndZ=0
  constraints (17):
    c: PointOnObject(g0,g-2)
    c: Diameter(g0) = 29
    c: DistanceY(g0,g0) = 0
    c: DistanceY(g0,g0) = 0
    c: Coincident(g1,g0)
    c: PointOnObject(g1,g-1)
    c: Vertical(g1)
    c: Coincident(g2,g0)
    c: DistanceY(g1,g1) = 15
    c: Coincident(g3,g1)
    c: Vertical(g3)
    c: Coincident(g4,g3)
    c: PointOnObject(g4,g-2)
    c: Horizontal(g4)
    c: Coincident(g5,g4)
    c: Coincident(g5,g2)
    c: Vertical(g5)
FEATURE [PartDesign::Pocket] Pocket069
  BaseFeature = -> Pad062
  Length = 13.5
  Length2 = 100
  Placement = pos=(0,0,0) rot=(1,0,0;1.5708rad)
  Profile = -> Sketch144
  Refine = true
  Reversed = true
  Type = 0
FEATURE [PartDesign::Mirrored] Mirrored018
  BaseFeature = -> Pocket069
  MirrorPlane = -> Sketch144 [V_Axis]
  Originals = -> [Pocket069]
  Placement = pos=(0,0,0) rot=(1,0,0;1.5708rad)
  Refine = true
FEATURE [Sketcher::SketchObject] Sketch145
  FullyConstrained = false
  MapMode = 5
  Placement = pos=(0,0,0) rot=(1,0,0;1.5708rad)
  Support = -> [XZ_Plane044]
  expr: Constraints[1] = <<screw>>.B4
  sketch-geometry (2):
    g0: Circle CenterX=-21.5 CenterY=3 CenterZ=0 NormalX=0 NormalY=0 NormalZ=1 AngleXU=0 Radius=1.625
    g1: Circle CenterX=21.5 CenterY=3 CenterZ=0 NormalX=0 NormalY=0 NormalZ=1 AngleXU=0 Radius=1.38589
  constraints (4):
    c: DistanceX(g0) = -21.5
    c: Diameter(g0) = 3.25
    c: Symmetric(g0,g1,g-2)
    c: DistanceY(g0) = 3
FEATURE [PartDesign::Pocket] Pocket070
  BaseFeature = -> Mirrored018
  Length = 5
  Length2 = 100
  Placement = pos=(0,0,0) rot=(1,0,0;1.5708rad)
  Profile = -> Sketch145
  Refine = true
  Reversed = true
  Type = 1
FEATURE [Sketcher::SketchObject] Sketch146
  AttachmentOffset = pos=(0,0,2) rot=(0,0,1;0rad)
  FullyConstrained = false
  MapMode = 5
  Placement = pos=(0,-2,-4e-16) rot=(1,0,0;1.5708rad)
  Support = -> [XZ_Plane044]
  sketch-geometry (3):
    g0: ArcOfCircle CenterX=0 CenterY=287.976 CenterZ=0 NormalX=0 NormalY=0 NormalZ=1 AngleXU=0 Radius=287.976 StartAngle=4.57899 EndAngle=4.94872
    g1: LineSegment StartX=-38.3007 StartY=2.55835 StartZ=0 EndX=-15.9703 EndY=31.7959 EndZ=0
    g2: LineSegment StartX=-15.9703 StartY=31.7959 StartZ=0 EndX=67.4262 EndY=8.00476 EndZ=0
  constraints (5):
    c: PointOnObject(g0,g-2)
    c: PointOnObject(g-1,g0)
    c: Coincident(g1,g0)
    c: Coincident(g2,g1)
    c: Coincident(g2,g0)
FEATURE [PartDesign::Pocket] Pocket071
  BaseFeature = -> Pocket070
  Length = 5
  Length2 = 100
  Placement = pos=(0,0,0) rot=(1,0,0;1.5708rad)
  Profile = -> Sketch146
  Refine = true
  Reversed = true
  Type = 1
FEATURE [PartDesign::Fillet] Fillet016
  Base = -> Pocket071 [Edge2,Edge12]
  BaseFeature = -> Pocket071
  Placement = pos=(0,0,0) rot=(1,0,0;1.5708rad)
  Radius = 9
  Refine = true
  SupportTransform = false
FEATURE [PartDesign::Fillet] Fillet017
  Base = -> Fillet016 [Edge3,Edge16]
  BaseFeature = -> Fillet016
  Placement = pos=(0,0,0) rot=(1,0,0;1.5708rad)
  Radius = 4
  Refine = true
  SupportTransform = false
FEATURE [PartDesign::Body] Body036  label="contre-poids-gopro"
  Group = -> [Sketch143,Pad062,Sketch144,Pocket069,Mirrored018,Sketch145,Pocket070,Sketch146,Pocket071,Fillet016,Fillet017]
  Origin = -> Origin044
  Placement = pos=(0,0,0) rot=(0,0,-1;0.785398rad)
  Tip = -> Fillet017
FEATURE [PartDesign::Pocket] Pocket072
  BaseFeature = -> Pad055
  Length = 5
  Length2 = 100
  Placement = pos=(0,0,0) rot=(0.57735,0.57735,0.57735;2.0944rad)
  Profile = -> Sketch128
  Refine = true
  Type = 1
FEATURE [PartDesign::Mirrored] Mirrored019
  BaseFeature = -> Pocket072
  MirrorPlane = -> Sketch128 [V_Axis]
  Originals = -> [Pocket072]
  Placement = pos=(0,0,0) rot=(0.57735,0.57735,0.57735;2.0944rad)
  Refine = true
FEATURE [PartDesign::Pad] Pad063
  BaseFeature = -> Mirrored019
  Direction = (1,1,1)
  Length = 4.5
  Length2 = 100
  Placement = pos=(0,0,0) rot=(0.57735,0.57735,0.57735;2.0944rad)
  Profile = -> Sketch130
  Refine = true
  Type = 0
FEATURE [Sketcher::SketchObject] Sketch147
  FullyConstrained = true
  MapMode = 5
  Placement = pos=(12.1,-2.7e-15,2.7e-15) rot=(0.57735,0.57735,0.57735;2.0944rad)
  Support = -> [Pad063]
  sketch-geometry (7):
    g0: LineSegment StartX=7.1473 StartY=-3.425 StartZ=0 EndX=4.7946 EndY=-7.5 EndZ=0
    g1: LineSegment StartX=4.7946 StartY=-7.5 StartZ=0 EndX=7.1473 EndY=-11.575 EndZ=0
    g2: LineSegment StartX=7.1473 StartY=-11.575 StartZ=0 EndX=11.8527 EndY=-11.575 EndZ=0
    g3: LineSegment StartX=11.8527 StartY=-11.575 StartZ=0 EndX=14.2054 EndY=-7.5 EndZ=0
    g4: LineSegment StartX=14.2054 StartY=-7.5 StartZ=0 EndX=11.8527 EndY=-3.425 EndZ=0
    g5: LineSegment StartX=11.8527 StartY=-3.425 StartZ=0 EndX=7.1473 EndY=-3.425 EndZ=0
    g6: Circle CenterX=9.5 CenterY=-7.5 CenterZ=0 NormalX=0 NormalY=0 NormalZ=1 AngleXU=0 Radius=4.7054
  constraints (17):
    c: Coincident(g0,g1)
    c: Coincident(g1,g2)
    c: Coincident(g2,g3)
    c: Coincident(g3,g4)
    c: Coincident(g4,g5)
    c: Coincident(g5,g0)
    c: Equal(g0, g1-g5) x5
    c: PointOnObject(g0,g6)
    c: PointOnObject(g1,g6)
    c: PointOnObject(g2,g6)
    c: PointOnObject(g3,g6)
    c: PointOnObject(g4,g6)
    c: PointOnObject(g5,g6)
    c: DistanceY(g6) = -7.5
    c: DistanceX(g6) = 9.5
    c: Parallel(g5,g-1)
    c: DistanceY(g1,g0) = 8.15
FEATURE [PartDesign::Pocket] Pocket073
  BaseFeature = -> Pad063
  Length = 4
  Length2 = 100
  Placement = pos=(0,0,0) rot=(0.57735,0.57735,0.57735;2.0944rad)
  Profile = -> Sketch147
  Refine = true
  Type = 0
FEATURE [PartDesign::Chamfer] Chamfer004
  Angle = 45
  Base = -> Pocket073 [Edge19,Edge15]
  BaseFeature = -> Pocket073
  ChamferType = 0
  FlipDirection = false
  Placement = pos=(0,0,0) rot=(0.57735,0.57735,0.57735;2.0944rad)
  Refine = true
  Size = 4
  Size2 = 1
  SupportTransform = false
FEATURE [Sketcher::SketchObject] Sketch148
  AttachmentOffset = pos=(0,-15,0) rot=(0,0,1;0rad)
  FullyConstrained = true
  MapMode = 5
  Placement = pos=(0,3.3e-15,-15) rot=(1,0,0;1.5708rad)
  Support = -> [XZ_Plane041]
  expr: Constraints[2] = <<screw>>.B5
  sketch-geometry (2):
    g0: Circle CenterX=-17.23 CenterY=0 CenterZ=0 NormalX=0 NormalY=0 NormalZ=1 AngleXU=0 Radius=2.8
    g1: Circle CenterX=17.23 CenterY=0 CenterZ=0 NormalX=0 NormalY=0 NormalZ=1 AngleXU=0 Radius=2.8
  constraints (5):
    c: PointOnObject(g0,g-1)
    c: Equal(g1,g0)
    c: Diameter(g0) = 5.6
    c: DistanceX(g0) = -17.23
    c: Symmetric(g0,g1,g-2)
FEATURE [PartDesign::Pocket] Pocket074
  BaseFeature = -> Chamfer004
  Length = 2
  Length2 = 100
  Placement = pos=(0,0,0) rot=(0.57735,0.57735,0.57735;2.0944rad)
  Profile = -> Sketch148
  Refine = true
  Reversed = true
  Type = 0
FEATURE [PartDesign::Fillet] Fillet018
  Base = -> Pocket074 [Edge72,Edge70,Edge42,Edge45]
  BaseFeature = -> Pocket074
  Placement = pos=(0,0,0) rot=(0.57735,0.57735,0.57735;2.0944rad)
  Radius = 5
  Refine = true
  SupportTransform = false
FEATURE [PartDesign::Body] Body033  label="support_gopro"
  Group = -> [Sketch127,Pad055,Sketch128,Sketch130,Pocket072,Mirrored019,Pad063,Sketch147,Pocket073,Chamfer004,Sketch148,Pocket074,Fillet018]
  Origin = -> Origin041
  Placement = pos=(-79.903,-79.9031,-45) rot=(0,0,1;2.35619rad)
  Tip = -> Fillet018
FEATURE [Sketcher::SketchObject] Sketch156
  FullyConstrained = true
  MapMode = 5
  Support = -> [XY_Plane045]
  expr: Constraints[3] = <<sho>>.B3 + 2 * <<sho>>.B4
  expr: Constraints[2] = <<sho>>.B3
  sketch-geometry (2):
    g0: Circle CenterX=0 CenterY=0 CenterZ=0 NormalX=0 NormalY=0 NormalZ=1 AngleXU=0 Radius=91
    g1: Circle CenterX=0 CenterY=0 CenterZ=0 NormalX=0 NormalY=0 NormalZ=1 AngleXU=0 Radius=96
  constraints (4):
    c: Coincident(g0,g-1)
    c: Coincident(g1,g0)
    c: Diameter(g0) = 182
    c: Diameter(g1) = 192
FEATURE [PartDesign::Pad] Pad068
  Direction = (1,1,1)
  Length = 37
  Length2 = 162
  Profile = -> Sketch156
  Refine = true
  Type = 4
FEATURE [Sketcher::SketchObject] Sketch157
  FullyConstrained = false
  MapMode = 5
  Placement = pos=(0,0,0) rot=(1,0,0;1.5708rad)
  Support = -> [XZ_Plane045]
  sketch-geometry (3):
    g0: ArcOfCircle CenterX=-164.456 CenterY=-16.3647 CenterZ=0 NormalX=0 NormalY=0 NormalZ=1 AngleXU=0 Radius=69.4558 StartAngle=0.000681798 EndAngle=0.876222
    g1: LineSegment StartX=-120 StartY=37 StartZ=0 EndX=-95 EndY=37 EndZ=0
    g2: LineSegment StartX=-95 StartY=37 StartZ=0 EndX=-95 EndY=-16.3174 EndZ=0
  constraints (9):
    c: DistanceY(g0) = 37
    c: DistanceX(g0) = -120
    c: Coincident(g1,g0)
    c: Horizontal(g1)
    c: DistanceX(g1) = -95
    c: DistanceY(g0) = -16.3174
    c: Coincident(g2,g1)
    c: Vertical(g2)
    c: Coincident(g2,g0)
FEATURE [PartDesign::Revolution] Revolution005
  Angle = 360
  Axis = (0,2e-16,1)
  Base = (0,0,0)
  BaseFeature = -> Pad068
  Profile = -> Sketch157
  ReferenceAxis = -> Sketch157 [V_Axis]
  Refine = true
FEATURE [Sketcher::SketchObject] Sketch158
  AttachmentOffset = pos=(0,0,-162) rot=(0,0,1;0rad)
  FullyConstrained = true
  MapMode = 5
  Placement = pos=(0,0,-162) rot=(0,0,1;0rad)
  Support = -> [XY_Plane045]
  expr: Constraints[10] = <<sho>>.B3
  sketch-geometry (4):
    g0: LineSegment StartX=-160.5 StartY=30 StartZ=0 EndX=-160.5 EndY=-30 EndZ=0
    g1: LineSegment StartX=-160.5 StartY=30 StartZ=0 EndX=-85.9127 EndY=30 EndZ=0
    g2: LineSegment StartX=-160.5 StartY=-30 StartZ=0 EndX=-85.9127 EndY=-30 EndZ=0
    g3: ArcOfCircle CenterX=0 CenterY=0 CenterZ=0 NormalX=0 NormalY=0 NormalZ=1 AngleXU=0 Radius=91 StartAngle=2.80564 EndAngle=3.47755
  constraints (11):
    c: Symmetric(g0,g0,g-1)
    c: DistanceX(g0) = -160.5
    c: DistanceY(g0) = 30
    c: Coincident(g1,g0)
    c: Horizontal(g1)
    c: Coincident(g2,g0)
    c: Horizontal(g2)
    c: Coincident(g3,g-1)
    c: Coincident(g3,g1)
    c: Coincident(g3,g2)
    c: Diameter(g3) = 182
FEATURE [PartDesign::Pad] Pad069
  BaseFeature = -> Revolution005
  Direction = (1,1,1)
  Length = 10
  Length2 = 100
  Profile = -> Sketch158
  Refine = true
  Type = 0
FEATURE [PartDesign::Mirrored] Mirrored020
  BaseFeature = -> Pad069
  MirrorPlane = -> Sketch158 [V_Axis]
  Originals = -> [Pad069]
  Refine = true
FEATURE [PartDesign::Body] Body037  label="ultra-simple-sho"
  Group = -> [Sketch156,Pad068,Sketch157,Revolution005,Sketch158,Pad069,Mirrored020]
  Origin = -> Origin045
  Placement = pos=(0,0,0) rot=(0,0,-1;0.785398rad)
  Tip = -> Mirrored020
FEATURE [App::Part] Part001  label="SHO-ADV001"
  Group = -> [Body006,Body009,Body018,Clone017,Clone016,Clone018,Fusion,Part__Mirroring,Fusion001,Body028,Clone019,Clone020,Clone022,Clone023,Clone024,Body037]
  Origin = -> Origin003
FEATURE [Sketcher::SketchObject] Sketch159
  FullyConstrained = true
  MapMode = 5
  Support = -> [XY_Plane046]
  sketch-geometry (1):
    g0: Circle CenterX=0 CenterY=0 CenterZ=0 NormalX=0 NormalY=0 NormalZ=1 AngleXU=0 Radius=52.5
  constraints (2):
    c: Coincident(g0,g-1)
    c: Diameter(g0) = 105
FEATURE [PartDesign::Pad] Pad070
  Direction = (1,1,1)
  Length = 6.5
  Length2 = 100
  Profile = -> Sketch159
  Refine = true
  Type = 0
FEATURE [Sketcher::SketchObject] Sketch160
  FullyConstrained = true
  MapMode = 5
  Support = -> [XY_Plane046]
  sketch-geometry (1):
    g0: Circle CenterX=0 CenterY=0 CenterZ=0 NormalX=0 NormalY=0 NormalZ=1 AngleXU=0 Radius=13.9
  constraints (2):
    c: Coincident(g0,g-1)
    c: Diameter(g0) = 27.8
FEATURE [PartDesign::Pad] Pad071
  BaseFeature = -> Pad070
  Direction = (1,1,1)
  Length = 19.8
  Length2 = 100
  Profile = -> Sketch160
  Refine = true
  Reversed = true
  Type = 0
FEATURE [PartDesign::Body] Body038  label="aux-mot-4inch"
  Group = -> [Sketch159,Pad070,Sketch160,Pad071]
  Origin = -> Origin046
  Placement = pos=(9.1709,-163.32,-29.3473) rot=(0.085288,0.205904,-0.974848;0.803573rad)
  Tip = -> Pad071
FEATURE [Part::Feature] Part__Feature001  label="aux-mot-mount"
  Placement = pos=(-5.65685,-148.492,-57) rot=(0.865867,-0.273007,-0.419215;1.78566rad)
  shape: bbox 42.43 x 42.74 x 19.12 mm, 111 faces (baked)
FEATURE [App::Part] Part004  label="AUX-mot"
  Group = -> [Body010,Body011,Clone012,Body012,Part__Feature001,Body038]
  Origin = -> Origin014
FEATURE [Sketcher::SketchObject] Sketch161
  FullyConstrained = true
  MapMode = 5
  Support = -> [XY_Plane047]
  sketch-geometry (1):
    g0: Circle CenterX=0 CenterY=0 CenterZ=0 NormalX=0 NormalY=0 NormalZ=1 AngleXU=0 Radius=250
  constraints (2):
    c: Coincident(g0,g-1)
    c: Diameter(g0) = 500
FEATURE [PartDesign::Body] Body039  label="trou-homme-50cm"
  Group = -> [Sketch161]
  Origin = -> Origin047
FEATURE [Sketcher::SketchObject] Sketch163
  FullyConstrained = true
  MapMode = 5
  Placement = pos=(0,0,0) rot=(1,0,0;1.5708rad)
  Support = -> [XZ_Plane048]
  sketch-geometry (1):
    g0: Circle CenterX=0 CenterY=4.9 CenterZ=0 NormalX=0 NormalY=0 NormalZ=1 AngleXU=0 Radius=4.9
  constraints (3):
    c: PointOnObject(g0,g-2)
    c: DistanceY(g0) = 4.9
    c: Diameter(g0) = 9.8
FEATURE [Sketcher::SketchObject] Sketch164
  FullyConstrained = true
  MapMode = 5
  Support = -> [XY_Plane048]
  expr: Constraints[11] = 117 + 3.32
  sketch-geometry (5):
    g0: GeomPoint X=19 Y=13.5 Z=0
    g1: ArcOfCircle CenterX=19 CenterY=13.5 CenterZ=0 NormalX=0 NormalY=0 NormalZ=1 AngleXU=0 Radius=58.5 StartAngle=3.37446 EndAngle=6.86512
    g2: ArcOfCircle CenterX=19 CenterY=13.5 CenterZ=0 NormalX=0 NormalY=0 NormalZ=1 AngleXU=0 Radius=60.16 StartAngle=3.36792 EndAngle=6.86512
    g3: LineSegment StartX=-37.921 StartY=5.3e-15 StartZ=0 EndX=-39.6257 EndY=-1.07e-14 EndZ=0
    g4: LineSegment StartX=67.871 StartY=45.654 StartZ=0 EndX=69.2577 EndY=46.5664 EndZ=0
  constraints (14):
    c: DistanceX(g0) = 19
    c: DistanceY(g0) = 13.5
    c: Coincident(g1,g0)
    c: PointOnObject(g1,g-1)
    c: Coincident(g2,g1)
    c: Coincident(g3,g1)
    c: Coincident(g3,g2)
    c: Coincident(g4,g1)
    c: Coincident(g4,g2)
    c: Perpendicular(g1,g4)
    c: Diameter(g1) = 117
    c: Diameter(g2) = 120.32
    c: Angle(g1) = 3.49066
    c: PointOnObject(g2,g-1)
FEATURE [PartDesign::Pad] Pad072
  Direction = (1,1,1)
  Length = 50
  Length2 = 100
  Profile = -> Sketch164
  Refine = true
  Type = 0
FEATURE [Sketcher::SketchObject] Sketch165
  AttachmentOffset = pos=(0,0,0) rot=(0,1,0;0.10472rad)
  FullyConstrained = true
  MapMode = 5
  Placement = pos=(0,0,0) rot=(0,1,0;0.10472rad)
  Support = -> [XY_Plane048]
  sketch-geometry (1):
    g0: Circle CenterX=0 CenterY=7.6 CenterZ=0 NormalX=0 NormalY=0 NormalZ=1 AngleXU=0 Radius=1.6
  constraints (3):
    c: PointOnObject(g0,g-2)
    c: Diameter(g0) = 3.2
    c: DistanceY(g0) = 7.6
FEATURE [Sketcher::SketchObject] Sketch166
  FullyConstrained = true
  MapMode = 5
  Placement = pos=(0,0,0) rot=(0.57735,0.57735,0.57735;2.0944rad)
  Support = -> [YZ_Plane048]
  sketch-geometry (1):
    g0: Circle CenterX=-3.5 CenterY=3.5 CenterZ=0 NormalX=0 NormalY=0 NormalZ=1 AngleXU=0 Radius=3.5
  constraints (3):
    c: Tangent(g0,g-1)
    c: Tangent(g0,g-2)
    c: Diameter(g0) = 7
FEATURE [PartDesign::Pad] Pad074
  BaseFeature = -> Pad072
  Direction = (1,1,1)
  Length = 90
  Length2 = 56
  Profile = -> Sketch166
  Refine = true
  Type = 4
FEATURE [Sketcher::SketchObject] Sketch168
  AttachmentOffset = pos=(0,0.001,23) rot=(0,1,0;0.772308rad)
  FullyConstrained = true
  MapMode = 5
  Placement = pos=(23,-5.1e-15,0.001) rot=(0.285879,0.677596,0.677596;2.58469rad)
  Support = -> [YZ_Plane048]
  sketch-geometry (1):
    g0: Circle CenterX=-3.5 CenterY=3.5 CenterZ=0 NormalX=0 NormalY=0 NormalZ=1 AngleXU=0 Radius=3.5
  constraints (3):
    c: Tangent(g0,g-1)
    c: Tangent(g0,g-2)
    c: Diameter(g0) = 7
FEATURE [PartDesign::Pad] Pad075
  BaseFeature = -> Pad074
  Direction = (1,1,1)
  Length = 72
  Length2 = 1.5
  Profile = -> Sketch168
  Refine = true
  Type = 4
FEATURE [Sketcher::SketchObject] Sketch169
  FullyConstrained = false
  MapMode = 5
  Support = -> [XY_Plane048]
  sketch-geometry (7):
    g0: GeomPoint X=19 Y=13.5 Z=0
    g1: ArcOfCircle CenterX=19 CenterY=13.5 CenterZ=0 NormalX=0 NormalY=0 NormalZ=1 AngleXU=0 Radius=60.16 StartAngle=3.36792 EndAngle=7.03311
    g2: LineSegment StartX=-39.6257 StartY=0 StartZ=0 EndX=-92.4191 EndY=0 EndZ=0
    g3: LineSegment StartX=-92.4191 StartY=0 StartZ=0 EndX=27.3459 EndY=-123.452 EndZ=0
    g4: LineSegment StartX=27.3459 StartY=-123.452 StartZ=0 EndX=160.914 EndY=8.08637 EndZ=0
    g5: LineSegment StartX=63.0214 StartY=54.5042 StartZ=0 EndX=156.043 EndY=54.5042 EndZ=0
    g6: LineSegment StartX=156.043 StartY=54.5042 StartZ=0 EndX=160.914 EndY=8.08637 EndZ=0
  constraints (14):
    c: DistanceX(g0) = 19
    c: DistanceY(g0) = 13.5
    c: Diameter(g1) = 120.32
    c: Angle(g1) = 3.66519
    c: Coincident(g2,g1)
    c: PointOnObject(g2,g-1)
    c: Horizontal(g2)
    c: Coincident(g3,g2)
    c: Coincident(g4,g3)
    c: Coincident(g5,g1)
    c: Horizontal(g5)
    c: Coincident(g6,g5)
    c: Coincident(g6,g4)
    c: Coincident(g1,g0)
FEATURE [PartDesign::Pad] Pad076
  BaseFeature = -> Pad075
  Direction = (1,1,1)
  Length = 4.5
  Length2 = 13.8
  Profile = -> Sketch163
  Refine = true
  Type = 4
FEATURE [PartDesign::Pocket] Pocket078
  BaseFeature = -> Pad076
  Length = 5
  Length2 = 100
  Midplane = true
  Profile = -> Sketch165
  Refine = true
  Type = 1
FEATURE [Sketcher::SketchObject] Sketch170
  AttachmentOffset = pos=(-3.5,0.001,15) rot=(0,1,0;1.5708rad)
  FullyConstrained = true
  MapMode = 5
  Placement = pos=(15,-3.5,0.001) rot=(0,0.707107,0.707107;3.14159rad)
  Support = -> [YZ_Plane048]
  sketch-geometry (1):
    g0: Circle CenterX=-3.5 CenterY=3.5 CenterZ=0 NormalX=0 NormalY=0 NormalZ=1 AngleXU=0 Radius=3.5
  constraints (3):
    c: Tangent(g0,g-1)
    c: Tangent(g0,g-2)
    c: Diameter(g0) = 7
FEATURE [PartDesign::Pad] Pad077
  BaseFeature = -> Pocket078
  Direction = (1,1,1)
  Length = 51
  Length2 = 100
  Profile = -> Sketch170
  Refine = true
  Reversed = true
  Type = 0
FEATURE [PartDesign::Pocket] Pocket079
  BaseFeature = -> Pad077
  Length = 5
  Length2 = 100
  Midplane = true
  Profile = -> Sketch169
  Refine = true
  Type = 1
FEATURE [Sketcher::SketchObject] Sketch171
  FullyConstrained = false
  MapMode = 5
  Placement = pos=(0,0,0) rot=(0.57735,0.57735,0.57735;2.0944rad)
  Support = -> [YZ_Plane048]
  sketch-geometry (4):
    g0: LineSegment StartX=55.9583 StartY=0 StartZ=0 EndX=-86.2213 EndY=0 EndZ=0
    g1: LineSegment StartX=-86.2213 StartY=0 StartZ=0 EndX=-86.2213 EndY=1 EndZ=0
    g2: LineSegment StartX=-86.2213 StartY=1 StartZ=0 EndX=55.9583 EndY=1 EndZ=0
    g3: LineSegment StartX=55.9583 StartY=1 StartZ=0 EndX=55.9583 EndY=0 EndZ=0
  constraints (10):
    c: Coincident(g0,g1)
    c: Coincident(g1,g2)
    c: Coincident(g2,g3)
    c: Coincident(g3,g0)
    c: Horizontal(g0)
    c: Horizontal(g2)
    c: Vertical(g1)
    c: Vertical(g3)
    c: PointOnObject(g0,g-1)
    c: DistanceY(g1,g1) = 1
FEATURE [PartDesign::Pocket] Pocket080
  BaseFeature = -> Pocket079
  Length = 5
  Length2 = 100
  Midplane = true
  Profile = -> Sketch171
  Refine = true
  Type = 1
FEATURE [PartDesign::Fillet] Fillet019
  Base = -> Pocket080 [Edge60]
  BaseFeature = -> Pocket080
  Radius = 2
  Refine = true
  SupportTransform = false
FEATURE [PartDesign::Fillet] Fillet020
  Base = -> Fillet019 [Edge8]
  BaseFeature = -> Fillet019
  Radius = 2.8
  Refine = true
  SupportTransform = false
FEATURE [PartDesign::Fillet] Fillet021
  Base = -> Fillet020 [Edge15,Edge11,Edge14]
  BaseFeature = -> Fillet020
  Radius = 2
  Refine = true
  SupportTransform = false
FEATURE [PartDesign::Chamfer] Chamfer005
  Angle = 45
  Base = -> Fillet021 [Edge73,Edge70]
  BaseFeature = -> Fillet021
  ChamferType = 0
  FlipDirection = false
  Refine = true
  Size = 5
  Size2 = 1
  SupportTransform = false
FEATURE [PartDesign::Fillet] Fillet022
  Base = -> Chamfer005 [Edge20,Edge18,Edge43,Edge49]
  BaseFeature = -> Chamfer005
  Radius = 4
  Refine = true
  SupportTransform = false
FEATURE [PartDesign::Body] Body040  label="carenage001"
  Group = -> [Sketch163,Sketch164,Pad072,Sketch165,Sketch166,Pad074,Sketch168,Pad075,Sketch169,Pad076,Pocket078,Sketch170,Pad077,Pocket079,Sketch171,Pocket080,Fillet019,Fillet020,Fillet021,Chamfer005,Fillet022]
  Origin = -> Origin048
  Placement = pos=(-17.3713,-160.121,-61.5) rot=(0,0,-1;0.785398rad)
  Tip = -> Fillet022
FEATURE [Sketcher::SketchObject] Sketch172
  FullyConstrained = true
  MapMode = 5
  Placement = pos=(0,0,0) rot=(0.57735,0.57735,0.57735;2.0944rad)
  Support = -> [YZ_Plane049]
  sketch-geometry (12):
    g0: GeomPoint X=0 Y=50 Z=0
    g1: GeomPoint X=-60 Y=0 Z=0
    g2: LineSegment StartX=-60 StartY=0 StartZ=0 EndX=-60 EndY=30.7899 EndZ=0
    g3: LineSegment StartX=-32.5651 StartY=50 StartZ=0 EndX=0 EndY=50 EndZ=0
    g4: LineSegment StartX=0 StartY=50 StartZ=0 EndX=0 EndY=40 EndZ=0
    g5: LineSegment StartX=0 StartY=40 StartZ=0 EndX=-30 EndY=40 EndZ=0
    g6: LineSegment StartX=-50 StartY=25.9958 StartZ=0 EndX=-50 EndY=0 EndZ=0
    g7: LineSegment StartX=-60 StartY=0 StartZ=0 EndX=-50 EndY=0 EndZ=0
    g8: LineSegment StartX=-30 StartY=40 StartZ=0 EndX=-50 EndY=25.9958 EndZ=0
    g9: LineSegment StartX=-32.5651 StartY=50 StartZ=0 EndX=-60 EndY=30.7899 EndZ=0
    g10: LineSegment StartX=-32.5651 StartY=50 StartZ=0 EndX=-30 EndY=40 EndZ=0
    g11: LineSegment StartX=-60 StartY=30.7899 StartZ=0 EndX=-50 EndY=25.9958 EndZ=0
  constraints (30):
    c: PointOnObject(g0,g-2)
    c: DistanceY(g0) = 50
    c: PointOnObject(g1,g-1)
    c: DistanceX(g1) = -60
    c: Coincident(g2,g1)
    c: Vertical(g2)
    c: Coincident(g3,g0)
    c: Horizontal(g3)
    c: Coincident(g4,g3)
    c: PointOnObject(g4,g-2)
    c: Coincident(g5,g4)
    c: Horizontal(g5)
    c: PointOnObject(g6,g-1)
    c: Vertical(g6)
    c: Coincident(g7,g2)
    c: Coincident(g7,g6)
    c: DistanceX(g7,g7) = 10
    c: Equal(g7,g4)
    c: Coincident(g8,g5)
    c: Coincident(g8,g6)
    c: Angle(g6,g8) = 2.18166
    c: Coincident(g9,g3)
    c: Coincident(g9,g2)
    c: Parallel(g9,g8)
    c: Coincident(g10,g3)
    c: Coincident(g10,g5)
    c: Coincident(g11,g2)
    c: Coincident(g11,g6)
    c: Angle(g10,g11) = 0.872665
    c: DistanceX(g5,g5) = 30
FEATURE [PartDesign::Pad] Pad078
  Direction = (1,1,1)
  Length = 12
  Length2 = 100
  Midplane = true
  Placement = pos=(0,0,0) rot=(0.57735,0.57735,0.57735;2.0944rad)
  Profile = -> Sketch172
  Refine = true
  Type = 0
FEATURE [PartDesign::Mirrored] Mirrored021
  BaseFeature = -> Pad078
  MirrorPlane = -> Sketch172 [V_Axis]
  Originals = -> [Pad078]
  Placement = pos=(0,0,0) rot=(0.57735,0.57735,0.57735;2.0944rad)
  Refine = true
FEATURE [Sketcher::SketchObject] Sketch173
  FullyConstrained = true
  MapMode = 5
  Placement = pos=(0,0,0) rot=(0.57735,0.57735,0.57735;2.0944rad)
  Support = -> [YZ_Plane049]
  sketch-geometry (2):
    g0: Circle CenterX=0 CenterY=36 CenterZ=0 NormalX=0 NormalY=0 NormalZ=1 AngleXU=0 Radius=14
    g1: GeomPoint X=0 Y=50 Z=0
  constraints (5):
    c: PointOnObject(g0,g-2)
    c: PointOnObject(g1,g-2)
    c: DistanceY(g1) = 50
    c: PointOnObject(g1,g0)
    c: Diameter(g0) = 28
FEATURE [PartDesign::Pad] Pad079
  BaseFeature = -> Mirrored021
  Direction = (1,1,1)
  Length = 12
  Length2 = 100
  Midplane = true
  Placement = pos=(0,0,0) rot=(0.57735,0.57735,0.57735;2.0944rad)
  Profile = -> Sketch173
  Refine = true
  Type = 0
FEATURE [Sketcher::SketchObject] Sketch174
  FullyConstrained = true
  MapMode = 5
  Placement = pos=(0,0,0) rot=(0.57735,0.57735,0.57735;2.0944rad)
  Support = -> [YZ_Plane049]
  sketch-geometry (2):
    g0: Circle CenterX=0 CenterY=36 CenterZ=0 NormalX=0 NormalY=0 NormalZ=1 AngleXU=0 Radius=9
    g1: GeomPoint X=0 Y=45 Z=0
  constraints (5):
    c: PointOnObject(g0,g-2)
    c: DistanceY(g0) = 36
    c: PointOnObject(g1,g-2)
    c: DistanceY(g1) = 45
    c: PointOnObject(g1,g0)
FEATURE [PartDesign::Pocket] Pocket081
  BaseFeature = -> Pad079
  Length = 5
  Length2 = 100
  Midplane = true
  Placement = pos=(0,0,0) rot=(0.57735,0.57735,0.57735;2.0944rad)
  Profile = -> Sketch174
  Refine = true
  Type = 1
FEATURE [Sketcher::SketchObject] Sketch175
  FullyConstrained = true
  MapMode = 5
  Support = -> [XY_Plane049]
  expr: Constraints[2] = <<screw>>.B4
  sketch-geometry (1):
    g0: Circle CenterX=0 CenterY=55 CenterZ=0 NormalX=0 NormalY=0 NormalZ=1 AngleXU=0 Radius=1.625
  constraints (3):
    c: PointOnObject(g0,g-2)
    c: DistanceY(g0) = 55
    c: Diameter(g0) = 3.25
FEATURE [Sketcher::SketchObject] Sketch176
  AttachmentOffset = pos=(0,0,5) rot=(0,0,1;0rad)
  FullyConstrained = true
  MapMode = 5
  Placement = pos=(0,0,5) rot=(0,0,1;0rad)
  Support = -> [XY_Plane049]
  expr: Constraints[2] = <<screw>>.B5 + 0.1
  sketch-geometry (1):
    g0: Circle CenterX=0 CenterY=55 CenterZ=0 NormalX=0 NormalY=0 NormalZ=1 AngleXU=0 Radius=2.85
  constraints (3):
    c: PointOnObject(g0,g-2)
    c: DistanceY(g0) = 55
    c: Diameter(g0) = 5.7
FEATURE [PartDesign::Fillet] Fillet023
  Base = -> Pocket081 [Edge46,Edge45]
  BaseFeature = -> Pocket081
  Placement = pos=(0,0,0) rot=(0.57735,0.57735,0.57735;2.0944rad)
  Radius = 9
  Refine = true
  SupportTransform = false
FEATURE [Sketcher::SketchObject] Sketch177
  FullyConstrained = true
  MapMode = 5
  Placement = pos=(0,0,0) rot=(0.57735,0.57735,0.57735;2.0944rad)
  Support = -> [YZ_Plane049]
  sketch-geometry (1):
    g0: Circle CenterX=-25 CenterY=40 CenterZ=0 NormalX=0 NormalY=0 NormalZ=1 AngleXU=0 Radius=4
  constraints (3):
    c: DistanceY(g0) = 40
    c: DistanceX(g0) = -25
    c: Diameter(g0) = 8
FEATURE [Sketcher::SketchObject] Sketch178
  FullyConstrained = true
  MapMode = 5
  Placement = pos=(0,0,0) rot=(0.57735,0.57735,0.57735;2.0944rad)
  Support = -> [YZ_Plane049]
  sketch-geometry (1):
    g0: Circle CenterX=-25 CenterY=40 CenterZ=0 NormalX=0 NormalY=0 NormalZ=1 AngleXU=0 Radius=2.5
  constraints (3):
    c: DistanceY(g0) = 40
    c: DistanceX(g0) = -25
    c: Diameter(g0) = 5
FEATURE [Sketcher::SketchObject] Sketch179
  AttachmentOffset = pos=(0,0,50) rot=(0,0,1;0rad)
  FullyConstrained = true
  MapMode = 5
  Placement = pos=(0,-50,-1.11e-14) rot=(1,0,0;1.5708rad)
  Support = -> [XZ_Plane049]
  sketch-geometry (7):
    g0: LineSegment StartX=-6 StartY=0 StartZ=0 EndX=6 EndY=0 EndZ=0
    g1: LineSegment StartX=-6 StartY=0 StartZ=0 EndX=-6 EndY=-6.59501 EndZ=0
    g2: LineSegment StartX=6 StartY=0 StartZ=0 EndX=6 EndY=-6.59501 EndZ=0
    g3: ArcOfCircle CenterX=0 CenterY=-7.6 CenterZ=0 NormalX=0 NormalY=0 NormalZ=1 AngleXU=0 Radius=5.1 StartAngle=0.198355 EndAngle=2.94324
    g4: GeomPoint X=0 Y=-2.5 Z=0
    g5: LineSegment StartX=-6 StartY=-6.59501 StartZ=0 EndX=-5 EndY=-6.59501 EndZ=0
    g6: LineSegment StartX=5 StartY=-6.59501 StartZ=0 EndX=6 EndY=-6.59501 EndZ=0
  constraints (20):
    c: PointOnObject(g0,g-1)
    c: DistanceX(g0,g0) = 12
    c: Symmetric(g0,g0,g-2)
    c: Coincident(g1,g0)
    c: Vertical(g1)
    c: Coincident(g2,g0)
    c: Vertical(g2)
    c: PointOnObject(g3,g-2)
    c: Diameter(g3) = 10.2
    c: PointOnObject(g4,g-2)
    c: PointOnObject(g4,g3)
    c: DistanceY(g4) = -2.5
    c: Coincident(g5,g1)
    c: Coincident(g5,g3)
    c: Horizontal(g5)
    c: Coincident(g6,g3)
    c: Coincident(g6,g2)
    c: Perpendicular(g6,g2)
    c: DistanceX(g5,g5) = 1
    c: DistanceX(g6,g6) = 1
FEATURE [Sketcher::SketchObject] Sketch180
  FullyConstrained = true
  MapMode = 5
  Support = -> [XY_Plane049]
  expr: Constraints[2] = <<screw>>.B4
  sketch-geometry (1):
    g0: Circle CenterX=0 CenterY=55 CenterZ=0 NormalX=0 NormalY=0 NormalZ=1 AngleXU=0 Radius=1.625
  constraints (3):
    c: PointOnObject(g0,g-2)
    c: DistanceY(g0) = 55
    c: Diameter(g0) = 3.25
FEATURE [PartDesign::Fillet] Fillet024
  Base = -> Fillet023 [Edge37,Edge34,Edge20,Edge23,Edge43,Edge39,Edge47,Edge35]
  BaseFeature = -> Fillet023
  Placement = pos=(0,0,0) rot=(0.57735,0.57735,0.57735;2.0944rad)
  Radius = 10
  Refine = true
  SupportTransform = false
FEATURE [PartDesign::Pocket] Pocket082
  BaseFeature = -> Fillet024
  Length = 5
  Length2 = 100
  Midplane = true
  Placement = pos=(0,0,0) rot=(0.57735,0.57735,0.57735;2.0944rad)
  Profile = -> Sketch175
  Refine = true
  Type = 1
FEATURE [PartDesign::Mirrored] Mirrored022
  BaseFeature = -> Pocket082
  MirrorPlane = -> XZ_Plane049
  Originals = -> [Pocket082]
  Placement = pos=(0,0,0) rot=(0.57735,0.57735,0.57735;2.0944rad)
  Refine = true
FEATURE [PartDesign::Pocket] Pocket083
  BaseFeature = -> Mirrored022
  Length = 5
  Length2 = 100
  Placement = pos=(0,0,0) rot=(0.57735,0.57735,0.57735;2.0944rad)
  Profile = -> Sketch176
  Refine = true
  Reversed = true
  Type = 1
FEATURE [PartDesign::Mirrored] Mirrored023
  BaseFeature = -> Pocket083
  MirrorPlane = -> XZ_Plane049
  Originals = -> [Pocket083]
  Placement = pos=(0,0,0) rot=(0.57735,0.57735,0.57735;2.0944rad)
  Refine = true
FEATURE [PartDesign::Pad] Pad080
  BaseFeature = -> Mirrored023
  Direction = (1,1,1)
  Length = 12
  Length2 = 100
  Midplane = true
  Placement = pos=(0,0,0) rot=(0.57735,0.57735,0.57735;2.0944rad)
  Profile = -> Sketch177
  Refine = true
  Type = 0
FEATURE [PartDesign::Mirrored] Mirrored024
  BaseFeature = -> Pad080
  MirrorPlane = -> Sketch177 [V_Axis]
  Originals = -> [Pad080]
  Placement = pos=(0,0,0) rot=(0.57735,0.57735,0.57735;2.0944rad)
  Refine = true
FEATURE [PartDesign::Pocket] Pocket084
  BaseFeature = -> Mirrored024
  Length = 5
  Length2 = 100
  Midplane = true
  Placement = pos=(0,0,0) rot=(0.57735,0.57735,0.57735;2.0944rad)
  Profile = -> Sketch178
  Refine = true
  Type = 1
FEATURE [PartDesign::Mirrored] Mirrored025
  BaseFeature = -> Pocket084
  MirrorPlane = -> Sketch178 [V_Axis]
  Originals = -> [Pocket084]
  Placement = pos=(0,0,0) rot=(0.57735,0.57735,0.57735;2.0944rad)
  Refine = true
FEATURE [PartDesign::Fillet] Fillet025
  Base = -> Mirrored025 [Edge66,Edge63,Edge7,Edge1]
  BaseFeature = -> Mirrored025
  Placement = pos=(0,0,0) rot=(0.57735,0.57735,0.57735;2.0944rad)
  Radius = 3
  Refine = true
  SupportTransform = false
FEATURE [PartDesign::Chamfer] Chamfer006
  Angle = 45
  Base = -> Fillet025 [Edge66,Edge64,Edge32,Edge33]
  BaseFeature = -> Fillet025
  ChamferType = 0
  FlipDirection = false
  Placement = pos=(0,0,0) rot=(0.57735,0.57735,0.57735;2.0944rad)
  Refine = true
  Size = 1
  Size2 = 1
  SupportTransform = false
FEATURE [PartDesign::Chamfer] Chamfer007
  Angle = 45
  Base = -> Chamfer006 [Edge100,Edge30]
  BaseFeature = -> Chamfer006
  ChamferType = 0
  FlipDirection = false
  Placement = pos=(0,0,0) rot=(0.57735,0.57735,0.57735;2.0944rad)
  Refine = true
  Size = 2
  Size2 = 1
  SupportTransform = false
FEATURE [PartDesign::Fillet] Fillet026
  Base = -> Chamfer007 [Edge105,Edge33]
  BaseFeature = -> Chamfer007
  Placement = pos=(0,0,0) rot=(0.57735,0.57735,0.57735;2.0944rad)
  Radius = 2
  Refine = true
  SupportTransform = false
FEATURE [PartDesign::Pad] Pad081
  BaseFeature = -> Fillet026
  Direction = (1,1,1)
  Length = 10
  Length2 = 100
  Placement = pos=(0,0,0) rot=(0.57735,0.57735,0.57735;2.0944rad)
  Profile = -> Sketch179
  Refine = true
  Type = 0
FEATURE [PartDesign::Mirrored] Mirrored026
  BaseFeature = -> Pad081
  MirrorPlane = -> XZ_Plane049
  Originals = -> [Pad081]
  Placement = pos=(0,0,0) rot=(0.57735,0.57735,0.57735;2.0944rad)
  Refine = true
FEATURE [PartDesign::Pocket] Pocket085
  BaseFeature = -> Mirrored026
  Length = 5
  Length2 = 100
  Placement = pos=(0,0,0) rot=(0.57735,0.57735,0.57735;2.0944rad)
  Profile = -> Sketch180
  Refine = true
  Type = 1
FEATURE [PartDesign::Mirrored] Mirrored027
  BaseFeature = -> Pocket085
  MirrorPlane = -> XZ_Plane049
  Originals = -> [Pocket085]
  Placement = pos=(0,0,0) rot=(0.57735,0.57735,0.57735;2.0944rad)
  Refine = true
FEATURE [PartDesign::Body] Body041  label="poignée-V2"
  Group = -> [Sketch172,Pad078,Mirrored021,Sketch173,Pad079,Sketch174,Pocket081,Sketch175,Sketch176,Fillet023,Fillet024,Pocket082,Mirrored022,Pocket083,Mirrored023,Sketch177,Pad080,Sketch178,Mirrored024,Pocket084,Mirrored025,Fillet025,Chamfer006,Chamfer007,Fillet026,Sketch179,Pad081,Mirrored026,Sketch180,Pocket085,Mirrored027]
  Origin = -> Origin049
  Tip = -> Mirrored027
FEATURE [App::Part] Part006  label="PILGRIM_eqpt"
  Group = -> [Body033,Body029,Body020,Body032,Body030,Body036,Body039,Body040,Body041]
  Origin = -> Origin025
FEATURE [Spreadsheet::Sheet] Spreadsheet007  label="payload001"
  cells = A1=DONNEES SUR LES FIXATIONS DE LA PAYLOAD; A3=FIXATION PAR QUEUE D'ARRONDE; A4=angle; B4==60deg; A5=overangle; B5==40deg; A6=largeur L1; B6=20; C6=largeur L2; D6=7; E6=largeur totale; F6==B6 + 2 * D6 + 2 * B7 / tan(B4); A7=profondeur P1; B7=8; A8=hauteur; B8==<<sho>>.B5 / 2; A9=jeu; B9=0.15; A10=thickness_platine; B10=4.5; A11=largeur platine; B11=60; A12=espacement-screw-hole-x-axis; B12=24; C12=12; D12=0; A13=espacement-entre-trous-z-axis; B13=15
FEATURE [Sketcher::SketchObject] Sketch181
  FullyConstrained = true
  MapMode = 5
  Support = -> [XY_Plane050]
  expr: Constraints[6] = <<sho>>.B3 / 2 + <<sho>>.B4
  expr: Constraints[8] = <<payload001>>.B4
  expr: Constraints[26] = <<payload001>>.B10
  expr: Constraints[13] = <<payload001>>.D6
  expr: Constraints[7] = <<payload001>>.B7 - <<payload001>>.B9
  expr: Constraints[10] = <<payload001>>.B6 - 2 * <<payload001>>.B9
  expr: Constraints[9] = <<payload001>>.B4
  expr: Constraints[27] = <<payload001>>.B11
  sketch-geometry (10):
    g0: LineSegment StartX=-21.3822 StartY=103.85 StartZ=0 EndX=-9.85 EndY=103.85 EndZ=0
    g1: LineSegment StartX=-9.85 StartY=103.85 StartZ=0 EndX=-14.3822 EndY=96 EndZ=0
    g2: LineSegment StartX=-14.3822 StartY=96 StartZ=0 EndX=14.3822 EndY=96 EndZ=0
    g3: LineSegment StartX=14.3822 StartY=96 StartZ=0 EndX=9.85 EndY=103.85 EndZ=0
    g4: LineSegment StartX=9.85 StartY=103.85 StartZ=0 EndX=21.3822 EndY=103.85 EndZ=0
    g5: LineSegment StartX=-21.3822 StartY=103.85 StartZ=0 EndX=-30 EndY=103.85 EndZ=0
    g6: LineSegment StartX=21.3822 StartY=103.85 StartZ=0 EndX=30 EndY=103.85 EndZ=0
    g7: LineSegment StartX=-30 StartY=103.85 StartZ=0 EndX=-30 EndY=108.35 EndZ=0
    g8: LineSegment StartX=-30 StartY=108.35 StartZ=0 EndX=30 EndY=108.35 EndZ=0
    g9: LineSegment StartX=30 StartY=103.85 StartZ=0 EndX=30 EndY=108.35 EndZ=0
  constraints (28):
    c: Horizontal(g0)
    c: Coincident(g1,g0)
    c: Coincident(g2,g1)
    c: Horizontal(g2)
    c: Coincident(g3,g2)
    c: Coincident(g4,g3)
    c: DistanceY(g1) = 96
    c: DistanceY(g1,g0) = 7.85
    c: Angle(g0,g1) = 1.0472
    c: Angle(g3,g4) = 1.0472
    c: DistanceX(g0,g3) = 19.7
    c: Symmetric(g0,g3,g-2)
    c: Symmetric(g0,g4,g-2)
    c: DistanceX(g0,g1) = 7
    c: Coincident(g5,g0)
    c: Horizontal(g5)
    c: Coincident(g6,g4)
    c: Horizontal(g6)
    c: Coincident(g7,g5)
    c: Vertical(g7)
    c: Coincident(g8,g7)
    c: Horizontal(g8)
    c: Coincident(g9,g6)
    c: Coincident(g9,g8)
    c: Vertical(g9)
    c: Equal(g5,g6)
    c: DistanceY(g7,g7) = 4.5
    c: DistanceX(g8,g8) = 60
FEATURE [PartDesign::Pad] Pad082
  Direction = (1,1,1)
  Length = 29.25
  Length2 = 100
  Profile = -> Sketch181
  Refine = true
  Reversed = true
  Type = 0
  expr: Length = <<payload001>>.B8
FEATURE [PartDesign::Fillet] Fillet027
  Base = -> Pad082 [Edge5,Edge2]
  BaseFeature = -> Pad082
  Radius = 1
  Refine = true
  SupportTransform = false
FEATURE [Sketcher::SketchObject] Sketch182
  AttachmentOffset = pos=(0,0,-109) rot=(0,0,1;0rad)
  FullyConstrained = true
  MapMode = 5
  Placement = pos=(0,109,2.42e-14) rot=(1,0,0;1.5708rad)
  Support = -> [XZ_Plane050]
  expr: Constraints[1] = -<<payload001>>.B8 / 3 + <<screw>>.B6 / 2
  expr: Constraints[0] = <<screw>>.B4
  sketch-geometry (1):
    g0: Circle CenterX=-17.229 CenterY=-7 CenterZ=0 NormalX=0 NormalY=0 NormalZ=1 AngleXU=0 Radius=1.625
  constraints (3):
    c: Diameter(g0) = 3.25
    c: DistanceY(g0) = -7
    c: DistanceX(g0) = -17.229
FEATURE [Sketcher::SketchObject] Sketch183
  FullyConstrained = true
  MapMode = 5
  Support = -> [XY_Plane050]
  expr: Constraints[5] = <<sho>>.B3 / 2 + <<sho>>.B4 + <<payload001>>.B7 - <<payload001>>.B9
  expr: Constraints[9] = <<payload001>>.B11
  expr: Constraints[7] = <<payload001>>.B10
  sketch-geometry (4):
    g0: LineSegment StartX=-30 StartY=108.35 StartZ=0 EndX=30 EndY=108.35 EndZ=0
    g1: LineSegment StartX=30 StartY=108.35 StartZ=0 EndX=30 EndY=103.85 EndZ=0
    g2: LineSegment StartX=30 StartY=103.85 StartZ=0 EndX=-30 EndY=103.85 EndZ=0
    g3: LineSegment StartX=-30 StartY=103.85 StartZ=0 EndX=-30 EndY=108.35 EndZ=0
  constraints (11):
    c: Coincident(g0,g1)
    c: Coincident(g1,g2)
    c: Coincident(g2,g3)
    c: Coincident(g3,g0)
    c: Vertical(g1)
    c: DistanceY(g2) = 103.85
    c: Perpendicular(g0,g3)
    c: DistanceY(g3,g3) = 4.5
    c: Perpendicular(g1,g0)
    c: DistanceX(g2,g2) = 60
    c: Symmetric(g2,g1,g-2)
FEATURE [PartDesign::Pad] Pad083
  BaseFeature = -> Fillet027
  Direction = (1,1,1)
  Length = 12
  Length2 = 0
  Profile = -> Sketch183
  Refine = true
  Type = 4
FEATURE [PartDesign::Pocket] Pocket086
  BaseFeature = -> Pad083
  Length = 5
  Length2 = 100
  Midplane = true
  Profile = -> Sketch182
  Refine = true
  Type = 1
FEATURE [PartDesign::Mirrored] Mirrored028
  BaseFeature = -> Pocket086
  MirrorPlane = -> Sketch182 [V_Axis]
  Originals = -> [Pocket086]
  Refine = true
FEATURE [PartDesign::Body] Body042  label="platine-tenon001"
  Group = -> [Sketch181,Pad082,Fillet027,Sketch182,Sketch183,Pad083,Pocket086,Mirrored028]
  Origin = -> Origin050
  Placement = pos=(0,0,-45) rot=(0,0,1;2.35619rad)
  Tip = -> Mirrored028
